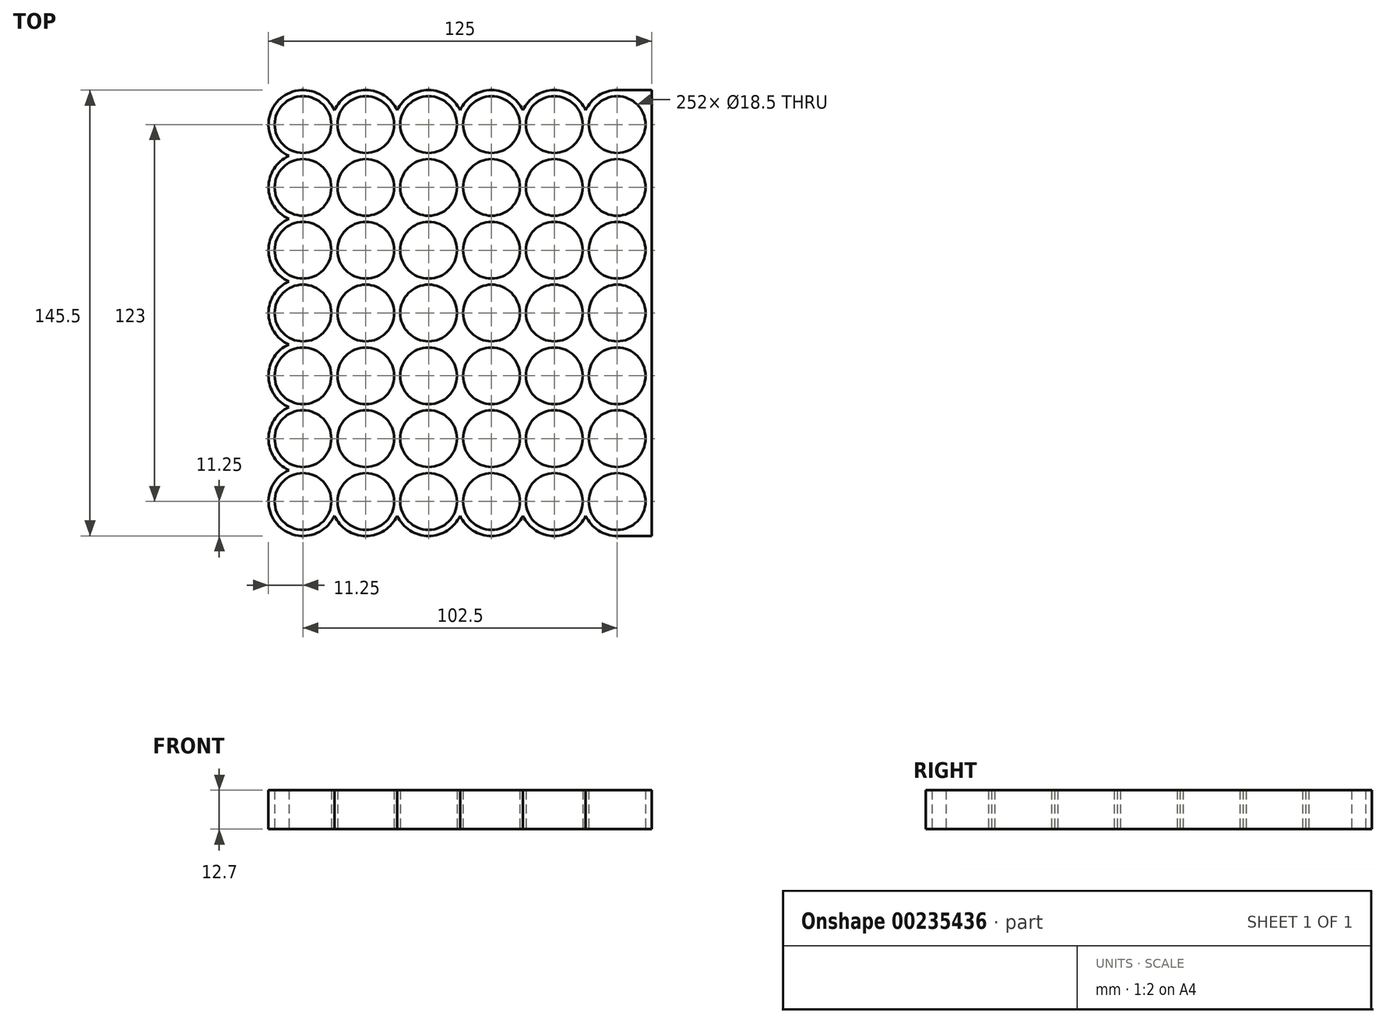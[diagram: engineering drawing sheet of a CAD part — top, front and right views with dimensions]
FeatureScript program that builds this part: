
annotation { "Feature Type Name" : "Feature", "Feature Type Description" : "" }
export const myFeature = defineFeature(function(context is Context, id is Id, definition is map)
    precondition{}
    {
        {
            var Q0;
            Q0=qCreatedBy(makeId("Top.planeOp"),FACE);
            var sketch = newSketch(context, id + "F0", { "sketchPlane" : qUnion([Q0])});
            skCircle(sketch, "E0", {"center": v(0, 0) * mm, "radius": 9.25 * mm});
            skCircle(sketch, "E1.0", {"center": v(0, 0) * mm, "radius": 11.25 * mm});
            skCircle(sketch, "E2.0.1.0", {"center": v(0, 20.5) * mm, "radius": 11.25 * mm});
            skCircle(sketch, "E2.0.1.1", {"center": v(0, 20.5) * mm, "radius": 9.25 * mm});
            skCircle(sketch, "E2.0.2.0", {"center": v(0, 41) * mm, "radius": 11.25 * mm});
            skCircle(sketch, "E2.0.2.1", {"center": v(0, 41) * mm, "radius": 9.25 * mm});
            skCircle(sketch, "E2.0.3.0", {"center": v(0, 61.5) * mm, "radius": 11.25 * mm});
            skCircle(sketch, "E2.0.3.1", {"center": v(0, 61.5) * mm, "radius": 9.25 * mm});
            skCircle(sketch, "E2.0.4.0", {"center": v(0, 82) * mm, "radius": 11.25 * mm});
            skCircle(sketch, "E2.0.4.1", {"center": v(0, 82) * mm, "radius": 9.25 * mm});
            skCircle(sketch, "E2.0.5.0", {"center": v(0, 102.5) * mm, "radius": 11.25 * mm});
            skCircle(sketch, "E2.0.5.1", {"center": v(0, 102.5) * mm, "radius": 9.25 * mm});
            skCircle(sketch, "E2.0.6.0", {"center": v(0, 123) * mm, "radius": 11.25 * mm});
            skCircle(sketch, "E2.0.6.1", {"center": v(0, 123) * mm, "radius": 9.25 * mm});
            skCircle(sketch, "E2.1.0.0", {"center": v(20.5, 0) * mm, "radius": 11.25 * mm});
            skCircle(sketch, "E2.1.0.1", {"center": v(20.5, 0) * mm, "radius": 9.25 * mm});
            skCircle(sketch, "E2.1.1.0", {"center": v(20.5, 20.5) * mm, "radius": 11.25 * mm});
            skCircle(sketch, "E2.1.1.1", {"center": v(20.5, 20.5) * mm, "radius": 9.25 * mm});
            skCircle(sketch, "E2.1.2.0", {"center": v(20.5, 41) * mm, "radius": 11.25 * mm});
            skCircle(sketch, "E2.1.2.1", {"center": v(20.5, 41) * mm, "radius": 9.25 * mm});
            skCircle(sketch, "E2.1.3.0", {"center": v(20.5, 61.5) * mm, "radius": 11.25 * mm});
            skCircle(sketch, "E2.1.3.1", {"center": v(20.5, 61.5) * mm, "radius": 9.25 * mm});
            skCircle(sketch, "E2.1.4.0", {"center": v(20.5, 82) * mm, "radius": 11.25 * mm});
            skCircle(sketch, "E2.1.4.1", {"center": v(20.5, 82) * mm, "radius": 9.25 * mm});
            skCircle(sketch, "E2.1.5.0", {"center": v(20.5, 102.5) * mm, "radius": 11.25 * mm});
            skCircle(sketch, "E2.1.5.1", {"center": v(20.5, 102.5) * mm, "radius": 9.25 * mm});
            skCircle(sketch, "E2.1.6.0", {"center": v(20.5, 123) * mm, "radius": 11.25 * mm});
            skCircle(sketch, "E2.1.6.1", {"center": v(20.5, 123) * mm, "radius": 9.25 * mm});
            skCircle(sketch, "E2.2.0.0", {"center": v(41, 0) * mm, "radius": 11.25 * mm});
            skCircle(sketch, "E2.2.0.1", {"center": v(41, 0) * mm, "radius": 9.25 * mm});
            skCircle(sketch, "E2.2.1.0", {"center": v(41, 20.5) * mm, "radius": 11.25 * mm});
            skCircle(sketch, "E2.2.1.1", {"center": v(41, 20.5) * mm, "radius": 9.25 * mm});
            skCircle(sketch, "E2.2.2.0", {"center": v(41, 41) * mm, "radius": 11.25 * mm});
            skCircle(sketch, "E2.2.2.1", {"center": v(41, 41) * mm, "radius": 9.25 * mm});
            skCircle(sketch, "E2.2.3.0", {"center": v(41, 61.5) * mm, "radius": 11.25 * mm});
            skCircle(sketch, "E2.2.3.1", {"center": v(41, 61.5) * mm, "radius": 9.25 * mm});
            skCircle(sketch, "E2.2.4.0", {"center": v(41, 82) * mm, "radius": 11.25 * mm});
            skCircle(sketch, "E2.2.4.1", {"center": v(41, 82) * mm, "radius": 9.25 * mm});
            skCircle(sketch, "E2.2.5.0", {"center": v(41, 102.5) * mm, "radius": 11.25 * mm});
            skCircle(sketch, "E2.2.5.1", {"center": v(41, 102.5) * mm, "radius": 9.25 * mm});
            skCircle(sketch, "E2.2.6.0", {"center": v(41, 123) * mm, "radius": 11.25 * mm});
            skCircle(sketch, "E2.2.6.1", {"center": v(41, 123) * mm, "radius": 9.25 * mm});
            skCircle(sketch, "E2.3.0.0", {"center": v(61.5, 0) * mm, "radius": 11.25 * mm});
            skCircle(sketch, "E2.3.0.1", {"center": v(61.5, 0) * mm, "radius": 9.25 * mm});
            skCircle(sketch, "E2.3.1.0", {"center": v(61.5, 20.5) * mm, "radius": 11.25 * mm});
            skCircle(sketch, "E2.3.1.1", {"center": v(61.5, 20.5) * mm, "radius": 9.25 * mm});
            skCircle(sketch, "E2.3.2.0", {"center": v(61.5, 41) * mm, "radius": 11.25 * mm});
            skCircle(sketch, "E2.3.2.1", {"center": v(61.5, 41) * mm, "radius": 9.25 * mm});
            skCircle(sketch, "E2.3.3.0", {"center": v(61.5, 61.5) * mm, "radius": 11.25 * mm});
            skCircle(sketch, "E2.3.3.1", {"center": v(61.5, 61.5) * mm, "radius": 9.25 * mm});
            skCircle(sketch, "E2.3.4.0", {"center": v(61.5, 82) * mm, "radius": 11.25 * mm});
            skCircle(sketch, "E2.3.4.1", {"center": v(61.5, 82) * mm, "radius": 9.25 * mm});
            skCircle(sketch, "E2.3.5.0", {"center": v(61.5, 102.5) * mm, "radius": 11.25 * mm});
            skCircle(sketch, "E2.3.5.1", {"center": v(61.5, 102.5) * mm, "radius": 9.25 * mm});
            skCircle(sketch, "E2.3.6.0", {"center": v(61.5, 123) * mm, "radius": 11.25 * mm});
            skCircle(sketch, "E2.3.6.1", {"center": v(61.5, 123) * mm, "radius": 9.25 * mm});
            skCircle(sketch, "E2.4.0.0", {"center": v(82, 0) * mm, "radius": 11.25 * mm});
            skCircle(sketch, "E2.4.0.1", {"center": v(82, 0) * mm, "radius": 9.25 * mm});
            skCircle(sketch, "E2.4.1.0", {"center": v(82, 20.5) * mm, "radius": 11.25 * mm});
            skCircle(sketch, "E2.4.1.1", {"center": v(82, 20.5) * mm, "radius": 9.25 * mm});
            skCircle(sketch, "E2.4.2.0", {"center": v(82, 41) * mm, "radius": 11.25 * mm});
            skCircle(sketch, "E2.4.2.1", {"center": v(82, 41) * mm, "radius": 9.25 * mm});
            skCircle(sketch, "E2.4.3.0", {"center": v(82, 61.5) * mm, "radius": 11.25 * mm});
            skCircle(sketch, "E2.4.3.1", {"center": v(82, 61.5) * mm, "radius": 9.25 * mm});
            skCircle(sketch, "E2.4.4.0", {"center": v(82, 82) * mm, "radius": 11.25 * mm});
            skCircle(sketch, "E2.4.4.1", {"center": v(82, 82) * mm, "radius": 9.25 * mm});
            skCircle(sketch, "E2.4.5.0", {"center": v(82, 102.5) * mm, "radius": 11.25 * mm});
            skCircle(sketch, "E2.4.5.1", {"center": v(82, 102.5) * mm, "radius": 9.25 * mm});
            skCircle(sketch, "E2.4.6.0", {"center": v(82, 123) * mm, "radius": 11.25 * mm});
            skCircle(sketch, "E2.4.6.1", {"center": v(82, 123) * mm, "radius": 9.25 * mm});
            skCircle(sketch, "E2.5.0.0", {"center": v(102.5, 0) * mm, "radius": 11.25 * mm});
            skCircle(sketch, "E2.5.0.1", {"center": v(102.5, 0) * mm, "radius": 9.25 * mm});
            skCircle(sketch, "E2.5.1.0", {"center": v(102.5, 20.5) * mm, "radius": 11.25 * mm});
            skCircle(sketch, "E2.5.1.1", {"center": v(102.5, 20.5) * mm, "radius": 9.25 * mm});
            skCircle(sketch, "E2.5.2.0", {"center": v(102.5, 41) * mm, "radius": 11.25 * mm});
            skCircle(sketch, "E2.5.2.1", {"center": v(102.5, 41) * mm, "radius": 9.25 * mm});
            skCircle(sketch, "E2.5.3.0", {"center": v(102.5, 61.5) * mm, "radius": 11.25 * mm});
            skCircle(sketch, "E2.5.3.1", {"center": v(102.5, 61.5) * mm, "radius": 9.25 * mm});
            skCircle(sketch, "E2.5.4.0", {"center": v(102.5, 82) * mm, "radius": 11.25 * mm});
            skCircle(sketch, "E2.5.4.1", {"center": v(102.5, 82) * mm, "radius": 9.25 * mm});
            skCircle(sketch, "E2.5.5.0", {"center": v(102.5, 102.5) * mm, "radius": 11.25 * mm});
            skCircle(sketch, "E2.5.5.1", {"center": v(102.5, 102.5) * mm, "radius": 9.25 * mm});
            skCircle(sketch, "E2.5.6.0", {"center": v(102.5, 123) * mm, "radius": 11.25 * mm});
            skCircle(sketch, "E2.5.6.1", {"center": v(102.5, 123) * mm, "radius": 9.25 * mm});
            skLineSegment(sketch, "E2.direction1", {"start": v(0, 0) * mm, "end": v(20.5, 0) * mm, "construction": true});
            skLineSegment(sketch, "E2.direction2", {"start": v(0, 0) * mm, "end": v(0, 20.5) * mm, "construction": true});
            skLineSegment(sketch, "E3", {"start": v(102.5, 0) * mm, "end": v(102.5, -11.25) * mm, "construction": true});
            skLineSegment(sketch, "E4", {"start": v(102.5, -11.25) * mm, "end": v(113.75, -11.25) * mm});
            skLineSegment(sketch, "E5", {"start": v(102.5, 123) * mm, "end": v(102.5, 134.25) * mm, "construction": true});
            skLineSegment(sketch, "E6", {"start": v(102.5, 134.25) * mm, "end": v(113.75, 134.25) * mm});
            skLineSegment(sketch, "E7", {"start": v(113.75, 134.25) * mm, "end": v(113.75, -11.25) * mm});
            skSolve(sketch);
        }
        {
            var Q0;
            {var subQ0=sQuery(id+"F0.wireOp",EDGE,"E2.10.4.0");var subQ1=sQuery(id+"F0.wireOp",EDGE,"E2.10.3.0");var subQ2=makeQuery(id+"F0.imprint","INTERSECT",VERTEX,{"disambiguationData":[OD(0.0)],"derivedFrom":[subQ1,subQ0]});Q0=makeQuery(id+"F0.imprint","IMPRINT",FACE,{"disambiguationData":[TD([[makeQuery(id+"F0.imprint","IMPRINT",EDGE,{"disambiguationData":[TD([[subQ2,-1.0]])],"derivedFrom":subQ1}),1.0]])]});}
            var Q1;
            {var subQ0=sQuery(id+"F0.wireOp",EDGE,"E2.1.5.0");var subQ1=sQuery(id+"F0.wireOp",EDGE,"E2.0.5.0");var subQ2=makeQuery(id+"F0.imprint","INTERSECT",VERTEX,{"disambiguationData":[OD(0.0)],"derivedFrom":[subQ1,subQ0]});Q1=makeQuery(id+"F0.imprint","IMPRINT",FACE,{"disambiguationData":[TD([[makeQuery(id+"F0.imprint","IMPRINT",EDGE,{"disambiguationData":[TD([[subQ2,-1.0]])],"derivedFrom":subQ1}),-1.0]])]});}
            var Q2;
            {var subQ0=sQuery(id+"F0.wireOp",EDGE,"E2.0.1.0");var subQ1=sQuery(id+"F0.wireOp",EDGE,"E1.0");var subQ2=makeQuery(id+"F0.imprint","INTERSECT",VERTEX,{"disambiguationData":[OD(1.0)],"derivedFrom":[subQ1,subQ0]});Q2=makeQuery(id+"F0.imprint","IMPRINT",FACE,{"disambiguationData":[TD([[makeQuery(id+"F0.imprint","IMPRINT",EDGE,{"disambiguationData":[TD([[subQ2,-1.0]])],"derivedFrom":subQ1}),-1.0]])]});}
            var Q3;
            {var subQ0=sQuery(id+"F0.wireOp",EDGE,"E2.2.3.0");var subQ1=sQuery(id+"F0.wireOp",EDGE,"E2.1.3.0");var subQ2=makeQuery(id+"F0.imprint","INTERSECT",VERTEX,{"disambiguationData":[OD(0.0)],"derivedFrom":[subQ1,subQ0]});Q3=makeQuery(id+"F0.imprint","IMPRINT",FACE,{"disambiguationData":[TD([[makeQuery(id+"F0.imprint","IMPRINT",EDGE,{"disambiguationData":[TD([[subQ2,-1.0]])],"derivedFrom":subQ1}),-1.0]])]});}
            var Q4;
            {var subQ0=sQuery(id+"F0.wireOp",EDGE,"E2.2.5.0");var subQ1=sQuery(id+"F0.wireOp",EDGE,"E2.1.5.0");var subQ2=makeQuery(id+"F0.imprint","INTERSECT",VERTEX,{"disambiguationData":[OD(0.0)],"derivedFrom":[subQ1,subQ0]});Q4=makeQuery(id+"F0.imprint","IMPRINT",FACE,{"disambiguationData":[TD([[makeQuery(id+"F0.imprint","IMPRINT",EDGE,{"disambiguationData":[TD([[subQ2,-1.0]])],"derivedFrom":subQ1}),-1.0]])]});}
            var Q5;
            {var subQ0=sQuery(id+"F0.wireOp",EDGE,"E2.3.1.0");var subQ1=sQuery(id+"F0.wireOp",EDGE,"E2.2.1.0");var subQ2=makeQuery(id+"F0.imprint","INTERSECT",VERTEX,{"disambiguationData":[OD(0.0)],"derivedFrom":[subQ1,subQ0]});Q5=makeQuery(id+"F0.imprint","IMPRINT",FACE,{"disambiguationData":[TD([[makeQuery(id+"F0.imprint","IMPRINT",EDGE,{"disambiguationData":[TD([[subQ2,-1.0]])],"derivedFrom":subQ1}),-1.0]])]});}
            var Q6;
            {var subQ0=sQuery(id+"F0.wireOp",EDGE,"E2.3.3.0");var subQ1=sQuery(id+"F0.wireOp",EDGE,"E2.2.3.0");var subQ2=makeQuery(id+"F0.imprint","INTERSECT",VERTEX,{"disambiguationData":[OD(0.0)],"derivedFrom":[subQ1,subQ0]});Q6=makeQuery(id+"F0.imprint","IMPRINT",FACE,{"disambiguationData":[TD([[makeQuery(id+"F0.imprint","IMPRINT",EDGE,{"disambiguationData":[TD([[subQ2,-1.0]])],"derivedFrom":subQ1}),-1.0]])]});}
            var Q7;
            {var subQ0=sQuery(id+"F0.wireOp",EDGE,"E2.1.3.0");var subQ1=sQuery(id+"F0.wireOp",EDGE,"E2.0.3.0");var subQ2=makeQuery(id+"F0.imprint","INTERSECT",VERTEX,{"disambiguationData":[OD(0.0)],"derivedFrom":[subQ1,subQ0]});Q7=makeQuery(id+"F0.imprint","IMPRINT",FACE,{"disambiguationData":[TD([[makeQuery(id+"F0.imprint","IMPRINT",EDGE,{"disambiguationData":[TD([[subQ2,1.0]])],"derivedFrom":subQ1}),1.0]])]});}
            var Q8;
            {var subQ0=sQuery(id+"F0.wireOp",EDGE,"E2.2.1.0");var subQ1=sQuery(id+"F0.wireOp",EDGE,"E2.1.1.0");var subQ2=makeQuery(id+"F0.imprint","INTERSECT",VERTEX,{"disambiguationData":[OD(0.0)],"derivedFrom":[subQ1,subQ0]});Q8=makeQuery(id+"F0.imprint","IMPRINT",FACE,{"disambiguationData":[TD([[makeQuery(id+"F0.imprint","IMPRINT",EDGE,{"disambiguationData":[TD([[subQ2,-1.0]])],"derivedFrom":subQ1}),-1.0]])]});}
            var Q9;
            {var subQ0=sQuery(id+"F0.wireOp",EDGE,"E2.7.6.0");var subQ1=sQuery(id+"F0.wireOp",EDGE,"E2.6.6.0");var subQ2=makeQuery(id+"F0.imprint","INTERSECT",VERTEX,{"disambiguationData":[OD(0.0)],"derivedFrom":[subQ1,subQ0]});Q9=makeQuery(id+"F0.imprint","IMPRINT",FACE,{"disambiguationData":[TD([[makeQuery(id+"F0.imprint","IMPRINT",EDGE,{"disambiguationData":[TD([[subQ2,1.0]])],"derivedFrom":subQ1}),-1.0]])]});}
            var Q10;
            {var subQ0=sQuery(id+"F0.wireOp",EDGE,"E2.11.6.0");var subQ1=sQuery(id+"F0.wireOp",EDGE,"E2.10.6.0");var subQ2=makeQuery(id+"F0.imprint","INTERSECT",VERTEX,{"disambiguationData":[OD(0.0)],"derivedFrom":[subQ1,subQ0]});Q10=makeQuery(id+"F0.imprint","IMPRINT",FACE,{"disambiguationData":[TD([[makeQuery(id+"F0.imprint","IMPRINT",EDGE,{"disambiguationData":[TD([[subQ2,1.0]])],"derivedFrom":subQ1}),-1.0]])]});}
            var Q11;
            {var subQ0=sQuery(id+"F0.wireOp",EDGE,"E2.11.3.0");var subQ1=sQuery(id+"F0.wireOp",EDGE,"E2.10.3.0");var subQ2=makeQuery(id+"F0.imprint","INTERSECT",VERTEX,{"disambiguationData":[OD(0.0)],"derivedFrom":[subQ1,subQ0]});Q11=makeQuery(id+"F0.imprint","IMPRINT",FACE,{"disambiguationData":[TD([[makeQuery(id+"F0.imprint","IMPRINT",EDGE,{"disambiguationData":[TD([[subQ2,-1.0]])],"derivedFrom":subQ1}),-1.0]])]});}
            var Q12;
            {var subQ0=sQuery(id+"F0.wireOp",EDGE,"E2.11.5.0");var subQ1=sQuery(id+"F0.wireOp",EDGE,"E2.10.5.0");var subQ2=makeQuery(id+"F0.imprint","INTERSECT",VERTEX,{"disambiguationData":[OD(0.0)],"derivedFrom":[subQ1,subQ0]});Q12=makeQuery(id+"F0.imprint","IMPRINT",FACE,{"disambiguationData":[TD([[makeQuery(id+"F0.imprint","IMPRINT",EDGE,{"disambiguationData":[TD([[subQ2,-1.0]])],"derivedFrom":subQ1}),-1.0]])]});}
            var Q13;
            {var subQ0=sQuery(id+"F0.wireOp",EDGE,"E2.9.5.0");var subQ1=sQuery(id+"F0.wireOp",EDGE,"E2.8.5.0");var subQ2=makeQuery(id+"F0.imprint","INTERSECT",VERTEX,{"disambiguationData":[OD(0.0)],"derivedFrom":[subQ1,subQ0]});Q13=makeQuery(id+"F0.imprint","IMPRINT",FACE,{"disambiguationData":[TD([[makeQuery(id+"F0.imprint","IMPRINT",EDGE,{"disambiguationData":[TD([[subQ2,-1.0]])],"derivedFrom":subQ1}),-1.0]])]});}
            var Q14;
            {var subQ0=sQuery(id+"F0.wireOp",EDGE,"E2.10.1.0");var subQ1=sQuery(id+"F0.wireOp",EDGE,"E2.9.1.0");var subQ2=makeQuery(id+"F0.imprint","INTERSECT",VERTEX,{"disambiguationData":[OD(0.0)],"derivedFrom":[subQ1,subQ0]});Q14=makeQuery(id+"F0.imprint","IMPRINT",FACE,{"disambiguationData":[TD([[makeQuery(id+"F0.imprint","IMPRINT",EDGE,{"disambiguationData":[TD([[subQ2,-1.0]])],"derivedFrom":subQ1}),-1.0]])]});}
            var Q15;
            {var subQ0=sQuery(id+"F0.wireOp",EDGE,"E2.10.3.0");var subQ1=sQuery(id+"F0.wireOp",EDGE,"E2.9.3.0");var subQ2=makeQuery(id+"F0.imprint","INTERSECT",VERTEX,{"disambiguationData":[OD(0.0)],"derivedFrom":[subQ1,subQ0]});Q15=makeQuery(id+"F0.imprint","IMPRINT",FACE,{"disambiguationData":[TD([[makeQuery(id+"F0.imprint","IMPRINT",EDGE,{"disambiguationData":[TD([[subQ2,-1.0]])],"derivedFrom":subQ1}),-1.0]])]});}
            var Q16;
            {var subQ0=sQuery(id+"F0.wireOp",EDGE,"E2.10.5.0");var subQ1=sQuery(id+"F0.wireOp",EDGE,"E2.9.5.0");var subQ2=makeQuery(id+"F0.imprint","INTERSECT",VERTEX,{"disambiguationData":[OD(0.0)],"derivedFrom":[subQ1,subQ0]});Q16=makeQuery(id+"F0.imprint","IMPRINT",FACE,{"disambiguationData":[TD([[makeQuery(id+"F0.imprint","IMPRINT",EDGE,{"disambiguationData":[TD([[subQ2,-1.0]])],"derivedFrom":subQ1}),-1.0]])]});}
            var Q17;
            {var subQ0=sQuery(id+"F0.wireOp",EDGE,"E2.8.3.0");var subQ1=sQuery(id+"F0.wireOp",EDGE,"E2.7.3.0");var subQ2=makeQuery(id+"F0.imprint","INTERSECT",VERTEX,{"disambiguationData":[OD(0.0)],"derivedFrom":[subQ1,subQ0]});Q17=makeQuery(id+"F0.imprint","IMPRINT",FACE,{"disambiguationData":[TD([[makeQuery(id+"F0.imprint","IMPRINT",EDGE,{"disambiguationData":[TD([[subQ2,-1.0]])],"derivedFrom":subQ1}),-1.0]])]});}
            var Q18;
            {var subQ0=sQuery(id+"F0.wireOp",EDGE,"E2.8.5.0");var subQ1=sQuery(id+"F0.wireOp",EDGE,"E2.7.5.0");var subQ2=makeQuery(id+"F0.imprint","INTERSECT",VERTEX,{"disambiguationData":[OD(0.0)],"derivedFrom":[subQ1,subQ0]});Q18=makeQuery(id+"F0.imprint","IMPRINT",FACE,{"disambiguationData":[TD([[makeQuery(id+"F0.imprint","IMPRINT",EDGE,{"disambiguationData":[TD([[subQ2,-1.0]])],"derivedFrom":subQ1}),-1.0]])]});}
            var Q19;
            {var subQ0=sQuery(id+"F0.wireOp",EDGE,"E2.9.1.0");var subQ1=sQuery(id+"F0.wireOp",EDGE,"E2.8.1.0");var subQ2=makeQuery(id+"F0.imprint","INTERSECT",VERTEX,{"disambiguationData":[OD(0.0)],"derivedFrom":[subQ1,subQ0]});Q19=makeQuery(id+"F0.imprint","IMPRINT",FACE,{"disambiguationData":[TD([[makeQuery(id+"F0.imprint","IMPRINT",EDGE,{"disambiguationData":[TD([[subQ2,-1.0]])],"derivedFrom":subQ1}),-1.0]])]});}
            var Q20;
            {var subQ0=sQuery(id+"F0.wireOp",EDGE,"E2.9.3.0");var subQ1=sQuery(id+"F0.wireOp",EDGE,"E2.8.3.0");var subQ2=makeQuery(id+"F0.imprint","INTERSECT",VERTEX,{"disambiguationData":[OD(0.0)],"derivedFrom":[subQ1,subQ0]});Q20=makeQuery(id+"F0.imprint","IMPRINT",FACE,{"disambiguationData":[TD([[makeQuery(id+"F0.imprint","IMPRINT",EDGE,{"disambiguationData":[TD([[subQ2,-1.0]])],"derivedFrom":subQ1}),-1.0]])]});}
            var Q21;
            {var subQ0=sQuery(id+"F0.wireOp",EDGE,"E2.7.5.0");var subQ1=sQuery(id+"F0.wireOp",EDGE,"E2.6.5.0");var subQ2=makeQuery(id+"F0.imprint","INTERSECT",VERTEX,{"disambiguationData":[OD(0.0)],"derivedFrom":[subQ1,subQ0]});Q21=makeQuery(id+"F0.imprint","IMPRINT",FACE,{"disambiguationData":[TD([[makeQuery(id+"F0.imprint","IMPRINT",EDGE,{"disambiguationData":[TD([[subQ2,-1.0]])],"derivedFrom":subQ1}),-1.0]])]});}
            var Q22;
            {var subQ0=sQuery(id+"F0.wireOp",EDGE,"E2.8.1.0");var subQ1=sQuery(id+"F0.wireOp",EDGE,"E2.7.1.0");var subQ2=makeQuery(id+"F0.imprint","INTERSECT",VERTEX,{"disambiguationData":[OD(0.0)],"derivedFrom":[subQ1,subQ0]});Q22=makeQuery(id+"F0.imprint","IMPRINT",FACE,{"disambiguationData":[TD([[makeQuery(id+"F0.imprint","IMPRINT",EDGE,{"disambiguationData":[TD([[subQ2,-1.0]])],"derivedFrom":subQ1}),-1.0]])]});}
            var Q23;
            {var subQ0=sQuery(id+"F0.wireOp",EDGE,"E2.6.3.0");var subQ1=sQuery(id+"F0.wireOp",EDGE,"E2.5.3.0");var subQ2=makeQuery(id+"F0.imprint","INTERSECT",VERTEX,{"disambiguationData":[OD(0.0)],"derivedFrom":[subQ1,subQ0]});Q23=makeQuery(id+"F0.imprint","IMPRINT",FACE,{"disambiguationData":[TD([[makeQuery(id+"F0.imprint","IMPRINT",EDGE,{"disambiguationData":[TD([[subQ2,-1.0]])],"derivedFrom":subQ1}),-1.0]])]});}
            var Q24;
            {var subQ0=sQuery(id+"F0.wireOp",EDGE,"E2.6.5.0");var subQ1=sQuery(id+"F0.wireOp",EDGE,"E2.5.5.0");var subQ2=makeQuery(id+"F0.imprint","INTERSECT",VERTEX,{"disambiguationData":[OD(0.0)],"derivedFrom":[subQ1,subQ0]});Q24=makeQuery(id+"F0.imprint","IMPRINT",FACE,{"disambiguationData":[TD([[makeQuery(id+"F0.imprint","IMPRINT",EDGE,{"disambiguationData":[TD([[subQ2,-1.0]])],"derivedFrom":subQ1}),-1.0]])]});}
            var Q25;
            {var subQ0=sQuery(id+"F0.wireOp",EDGE,"E2.7.1.0");var subQ1=sQuery(id+"F0.wireOp",EDGE,"E2.6.1.0");var subQ2=makeQuery(id+"F0.imprint","INTERSECT",VERTEX,{"disambiguationData":[OD(0.0)],"derivedFrom":[subQ1,subQ0]});Q25=makeQuery(id+"F0.imprint","IMPRINT",FACE,{"disambiguationData":[TD([[makeQuery(id+"F0.imprint","IMPRINT",EDGE,{"disambiguationData":[TD([[subQ2,-1.0]])],"derivedFrom":subQ1}),-1.0]])]});}
            var Q26;
            {var subQ0=sQuery(id+"F0.wireOp",EDGE,"E2.7.3.0");var subQ1=sQuery(id+"F0.wireOp",EDGE,"E2.6.3.0");var subQ2=makeQuery(id+"F0.imprint","INTERSECT",VERTEX,{"disambiguationData":[OD(0.0)],"derivedFrom":[subQ1,subQ0]});Q26=makeQuery(id+"F0.imprint","IMPRINT",FACE,{"disambiguationData":[TD([[makeQuery(id+"F0.imprint","IMPRINT",EDGE,{"disambiguationData":[TD([[subQ2,-1.0]])],"derivedFrom":subQ1}),-1.0]])]});}
            var Q27;
            {var subQ0=sQuery(id+"F0.wireOp",EDGE,"E2.5.1.0");var subQ1=sQuery(id+"F0.wireOp",EDGE,"E2.4.1.0");var subQ2=makeQuery(id+"F0.imprint","INTERSECT",VERTEX,{"disambiguationData":[OD(0.0)],"derivedFrom":[subQ1,subQ0]});Q27=makeQuery(id+"F0.imprint","IMPRINT",FACE,{"disambiguationData":[TD([[makeQuery(id+"F0.imprint","IMPRINT",EDGE,{"disambiguationData":[TD([[subQ2,-1.0]])],"derivedFrom":subQ1}),-1.0]])]});}
            var Q28;
            {var subQ0=sQuery(id+"F0.wireOp",EDGE,"E2.5.3.0");var subQ1=sQuery(id+"F0.wireOp",EDGE,"E2.4.3.0");var subQ2=makeQuery(id+"F0.imprint","INTERSECT",VERTEX,{"disambiguationData":[OD(0.0)],"derivedFrom":[subQ1,subQ0]});Q28=makeQuery(id+"F0.imprint","IMPRINT",FACE,{"disambiguationData":[TD([[makeQuery(id+"F0.imprint","IMPRINT",EDGE,{"disambiguationData":[TD([[subQ2,-1.0]])],"derivedFrom":subQ1}),-1.0]])]});}
            var Q29;
            {var subQ0=sQuery(id+"F0.wireOp",EDGE,"E2.5.5.0");var subQ1=sQuery(id+"F0.wireOp",EDGE,"E2.4.5.0");var subQ2=makeQuery(id+"F0.imprint","INTERSECT",VERTEX,{"disambiguationData":[OD(0.0)],"derivedFrom":[subQ1,subQ0]});Q29=makeQuery(id+"F0.imprint","IMPRINT",FACE,{"disambiguationData":[TD([[makeQuery(id+"F0.imprint","IMPRINT",EDGE,{"disambiguationData":[TD([[subQ2,-1.0]])],"derivedFrom":subQ1}),-1.0]])]});}
            var Q30;
            {var subQ0=sQuery(id+"F0.wireOp",EDGE,"E2.6.1.0");var subQ1=sQuery(id+"F0.wireOp",EDGE,"E2.5.1.0");var subQ2=makeQuery(id+"F0.imprint","INTERSECT",VERTEX,{"disambiguationData":[OD(0.0)],"derivedFrom":[subQ1,subQ0]});Q30=makeQuery(id+"F0.imprint","IMPRINT",FACE,{"disambiguationData":[TD([[makeQuery(id+"F0.imprint","IMPRINT",EDGE,{"disambiguationData":[TD([[subQ2,-1.0]])],"derivedFrom":subQ1}),-1.0]])]});}
            var Q31;
            {var subQ0=sQuery(id+"F0.wireOp",EDGE,"E2.3.5.0");var subQ1=sQuery(id+"F0.wireOp",EDGE,"E2.2.5.0");var subQ2=makeQuery(id+"F0.imprint","INTERSECT",VERTEX,{"disambiguationData":[OD(0.0)],"derivedFrom":[subQ1,subQ0]});Q31=makeQuery(id+"F0.imprint","IMPRINT",FACE,{"disambiguationData":[TD([[makeQuery(id+"F0.imprint","IMPRINT",EDGE,{"disambiguationData":[TD([[subQ2,-1.0]])],"derivedFrom":subQ1}),-1.0]])]});}
            var Q32;
            {var subQ0=sQuery(id+"F0.wireOp",EDGE,"E2.4.1.0");var subQ1=sQuery(id+"F0.wireOp",EDGE,"E2.3.1.0");var subQ2=makeQuery(id+"F0.imprint","INTERSECT",VERTEX,{"disambiguationData":[OD(0.0)],"derivedFrom":[subQ1,subQ0]});Q32=makeQuery(id+"F0.imprint","IMPRINT",FACE,{"disambiguationData":[TD([[makeQuery(id+"F0.imprint","IMPRINT",EDGE,{"disambiguationData":[TD([[subQ2,-1.0]])],"derivedFrom":subQ1}),-1.0]])]});}
            var Q33;
            {var subQ0=sQuery(id+"F0.wireOp",EDGE,"E2.4.3.0");var subQ1=sQuery(id+"F0.wireOp",EDGE,"E2.3.3.0");var subQ2=makeQuery(id+"F0.imprint","INTERSECT",VERTEX,{"disambiguationData":[OD(0.0)],"derivedFrom":[subQ1,subQ0]});Q33=makeQuery(id+"F0.imprint","IMPRINT",FACE,{"disambiguationData":[TD([[makeQuery(id+"F0.imprint","IMPRINT",EDGE,{"disambiguationData":[TD([[subQ2,-1.0]])],"derivedFrom":subQ1}),-1.0]])]});}
            var Q34;
            {var subQ0=sQuery(id+"F0.wireOp",EDGE,"E2.4.5.0");var subQ1=sQuery(id+"F0.wireOp",EDGE,"E2.3.5.0");var subQ2=makeQuery(id+"F0.imprint","INTERSECT",VERTEX,{"disambiguationData":[OD(0.0)],"derivedFrom":[subQ1,subQ0]});Q34=makeQuery(id+"F0.imprint","IMPRINT",FACE,{"disambiguationData":[TD([[makeQuery(id+"F0.imprint","IMPRINT",EDGE,{"disambiguationData":[TD([[subQ2,-1.0]])],"derivedFrom":subQ1}),-1.0]])]});}
            var Q35;
            {var subQ0=sQuery(id+"F0.wireOp",EDGE,"E2.11.1.0");var subQ1=sQuery(id+"F0.wireOp",EDGE,"E2.10.1.0");var subQ2=makeQuery(id+"F0.imprint","INTERSECT",VERTEX,{"disambiguationData":[OD(0.0)],"derivedFrom":[subQ1,subQ0]});Q35=makeQuery(id+"F0.imprint","IMPRINT",FACE,{"disambiguationData":[TD([[makeQuery(id+"F0.imprint","IMPRINT",EDGE,{"disambiguationData":[TD([[subQ2,-1.0]])],"derivedFrom":subQ1}),1.0]])]});}
            var Q36;
            {var subQ0=sQuery(id+"F0.wireOp",EDGE,"E2.1.0.0");var subQ1=sQuery(id+"F0.wireOp",EDGE,"E1.0");var subQ2=makeQuery(id+"F0.imprint","INTERSECT",VERTEX,{"disambiguationData":[OD(1.0)],"derivedFrom":[subQ1,subQ0]});Q36=makeQuery(id+"F0.imprint","IMPRINT",FACE,{"disambiguationData":[TD([[makeQuery(id+"F0.imprint","IMPRINT",EDGE,{"disambiguationData":[TD([[subQ2,-1.0]])],"derivedFrom":subQ1}),-1.0]])]});}
            var Q37;
            {var subQ0=sQuery(id+"F0.wireOp",EDGE,"E2.10.3.0");var subQ1=sQuery(id+"F0.wireOp",EDGE,"E2.9.3.0");var subQ2=makeQuery(id+"F0.imprint","INTERSECT",VERTEX,{"disambiguationData":[OD(0.0)],"derivedFrom":[subQ1,subQ0]});Q37=makeQuery(id+"F0.imprint","IMPRINT",FACE,{"disambiguationData":[TD([[makeQuery(id+"F0.imprint","IMPRINT",EDGE,{"disambiguationData":[TD([[subQ2,-1.0]])],"derivedFrom":subQ1}),1.0]])]});}
            var Q38;
            {var subQ0=sQuery(id+"F0.wireOp",EDGE,"E2.8.5.0");var subQ1=sQuery(id+"F0.wireOp",EDGE,"E2.7.5.0");var subQ2=makeQuery(id+"F0.imprint","INTERSECT",VERTEX,{"disambiguationData":[OD(0.0)],"derivedFrom":[subQ1,subQ0]});Q38=makeQuery(id+"F0.imprint","IMPRINT",FACE,{"disambiguationData":[TD([[makeQuery(id+"F0.imprint","IMPRINT",EDGE,{"disambiguationData":[TD([[subQ2,-1.0]])],"derivedFrom":subQ1}),1.0]])]});}
            var Q39;
            {var subQ0=sQuery(id+"F0.wireOp",EDGE,"E2.9.3.0");var subQ1=sQuery(id+"F0.wireOp",EDGE,"E2.8.3.0");var subQ2=makeQuery(id+"F0.imprint","INTERSECT",VERTEX,{"disambiguationData":[OD(0.0)],"derivedFrom":[subQ1,subQ0]});Q39=makeQuery(id+"F0.imprint","IMPRINT",FACE,{"disambiguationData":[TD([[makeQuery(id+"F0.imprint","IMPRINT",EDGE,{"disambiguationData":[TD([[subQ2,-1.0]])],"derivedFrom":subQ1}),1.0]])]});}
            var Q40;
            {var subQ0=sQuery(id+"F0.wireOp",EDGE,"E2.5.3.0");var subQ1=sQuery(id+"F0.wireOp",EDGE,"E2.4.3.0");var subQ2=makeQuery(id+"F0.imprint","INTERSECT",VERTEX,{"disambiguationData":[OD(0.0)],"derivedFrom":[subQ1,subQ0]});Q40=makeQuery(id+"F0.imprint","IMPRINT",FACE,{"disambiguationData":[TD([[makeQuery(id+"F0.imprint","IMPRINT",EDGE,{"disambiguationData":[TD([[subQ2,-1.0]])],"derivedFrom":subQ1}),1.0]])]});}
            var Q41;
            {var subQ0=sQuery(id+"F0.wireOp",EDGE,"E2.0.2.0");var subQ1=sQuery(id+"F0.wireOp",EDGE,"E2.0.1.0");var subQ2=makeQuery(id+"F0.imprint","INTERSECT",VERTEX,{"disambiguationData":[OD(0.0)],"derivedFrom":[subQ1,subQ0]});Q41=makeQuery(id+"F0.imprint","IMPRINT",FACE,{"disambiguationData":[TD([[makeQuery(id+"F0.imprint","IMPRINT",EDGE,{"disambiguationData":[TD([[subQ2,1.0]])],"derivedFrom":subQ1}),-1.0]])]});}
            var Q42;
            {var subQ0=sQuery(id+"F0.wireOp",EDGE,"E2.6.1.0");var subQ1=sQuery(id+"F0.wireOp",EDGE,"E2.5.1.0");var subQ2=makeQuery(id+"F0.imprint","INTERSECT",VERTEX,{"disambiguationData":[OD(0.0)],"derivedFrom":[subQ1,subQ0]});Q42=makeQuery(id+"F0.imprint","IMPRINT",FACE,{"disambiguationData":[TD([[makeQuery(id+"F0.imprint","IMPRINT",EDGE,{"disambiguationData":[TD([[subQ2,-1.0]])],"derivedFrom":subQ1}),1.0]])]});}
            var Q43;
            {var subQ0=sQuery(id+"F0.wireOp",EDGE,"E2.3.5.0");var subQ1=sQuery(id+"F0.wireOp",EDGE,"E2.2.5.0");var subQ2=makeQuery(id+"F0.imprint","INTERSECT",VERTEX,{"disambiguationData":[OD(0.0)],"derivedFrom":[subQ1,subQ0]});Q43=makeQuery(id+"F0.imprint","IMPRINT",FACE,{"disambiguationData":[TD([[makeQuery(id+"F0.imprint","IMPRINT",EDGE,{"disambiguationData":[TD([[subQ2,-1.0]])],"derivedFrom":subQ1}),1.0]])]});}
            var Q44;
            {var subQ0=sQuery(id+"F0.wireOp",EDGE,"E2.1.0.0");var subQ1=sQuery(id+"F0.wireOp",EDGE,"E1.0");var subQ2=makeQuery(id+"F0.imprint","INTERSECT",VERTEX,{"disambiguationData":[OD(0.0)],"derivedFrom":[subQ1,subQ0]});Q44=makeQuery(id+"F0.imprint","IMPRINT",FACE,{"disambiguationData":[TD([[makeQuery(id+"F0.imprint","IMPRINT",EDGE,{"disambiguationData":[TD([[subQ2,-1.0]])],"derivedFrom":subQ1}),-1.0]])]});}
            var Q45;
            {var subQ0=sQuery(id+"F0.wireOp",EDGE,"E2.4.3.0");var subQ1=sQuery(id+"F0.wireOp",EDGE,"E2.3.3.0");var subQ2=makeQuery(id+"F0.imprint","INTERSECT",VERTEX,{"disambiguationData":[OD(0.0)],"derivedFrom":[subQ1,subQ0]});Q45=makeQuery(id+"F0.imprint","IMPRINT",FACE,{"disambiguationData":[TD([[makeQuery(id+"F0.imprint","IMPRINT",EDGE,{"disambiguationData":[TD([[subQ2,-1.0]])],"derivedFrom":subQ1}),1.0]])]});}
            var Q46;
            {var subQ0=sQuery(id+"F0.wireOp",EDGE,"E2.0.1.0");var subQ1=sQuery(id+"F0.wireOp",EDGE,"E1.0");var subQ2=makeQuery(id+"F0.imprint","INTERSECT",VERTEX,{"disambiguationData":[OD(0.0)],"derivedFrom":[subQ1,subQ0]});Q46=makeQuery(id+"F0.imprint","IMPRINT",FACE,{"disambiguationData":[TD([[makeQuery(id+"F0.imprint","IMPRINT",EDGE,{"disambiguationData":[TD([[subQ2,1.0]])],"derivedFrom":subQ1}),-1.0]])]});}
            var Q47;
            {var subQ0=sQuery(id+"F0.wireOp",EDGE,"E2.0.1.0");var subQ1=sQuery(id+"F0.wireOp",EDGE,"E0");var subQ2=makeQuery(id+"F0.imprint","INTERSECT",VERTEX,{"derivedFrom":[subQ1,subQ0]});Q47=makeQuery(id+"F0.imprint","IMPRINT",FACE,{"disambiguationData":[TD([[makeQuery(id+"F0.imprint","IMPRINT",EDGE,{"disambiguationData":[TD([[subQ2,-1.0]])],"derivedFrom":subQ1}),-1.0]])]});}
            var Q48;
            {var subQ0=sQuery(id+"F0.wireOp",EDGE,"E2.11.1.0");var subQ1=sQuery(id+"F0.wireOp",EDGE,"E2.10.1.0");var subQ2=makeQuery(id+"F0.imprint","INTERSECT",VERTEX,{"disambiguationData":[OD(0.0)],"derivedFrom":[subQ1,subQ0]});Q48=makeQuery(id+"F0.imprint","IMPRINT",FACE,{"disambiguationData":[TD([[makeQuery(id+"F0.imprint","IMPRINT",EDGE,{"disambiguationData":[TD([[subQ2,1.0]])],"derivedFrom":subQ1}),-1.0]])]});}
            var Q49;
            {var subQ0=sQuery(id+"F0.wireOp",EDGE,"E2.9.5.0");var subQ1=sQuery(id+"F0.wireOp",EDGE,"E2.8.5.0");var subQ2=makeQuery(id+"F0.imprint","INTERSECT",VERTEX,{"disambiguationData":[OD(0.0)],"derivedFrom":[subQ1,subQ0]});Q49=makeQuery(id+"F0.imprint","IMPRINT",FACE,{"disambiguationData":[TD([[makeQuery(id+"F0.imprint","IMPRINT",EDGE,{"disambiguationData":[TD([[subQ2,1.0]])],"derivedFrom":subQ1}),-1.0]])]});}
            var Q50;
            {var subQ0=sQuery(id+"F0.wireOp",EDGE,"E2.0.5.0");var subQ1=sQuery(id+"F0.wireOp",EDGE,"E2.0.4.0");var subQ2=makeQuery(id+"F0.imprint","INTERSECT",VERTEX,{"disambiguationData":[OD(0.0)],"derivedFrom":[subQ1,subQ0]});Q50=makeQuery(id+"F0.imprint","IMPRINT",FACE,{"disambiguationData":[TD([[makeQuery(id+"F0.imprint","IMPRINT",EDGE,{"disambiguationData":[TD([[subQ2,1.0]])],"derivedFrom":subQ1}),-1.0]])]});}
            var Q51;
            {var subQ0=sQuery(id+"F0.wireOp",EDGE,"E2.0.6.0");var subQ1=sQuery(id+"F0.wireOp",EDGE,"E2.0.5.0");var subQ2=makeQuery(id+"F0.imprint","INTERSECT",VERTEX,{"disambiguationData":[OD(0.0)],"derivedFrom":[subQ1,subQ0]});Q51=makeQuery(id+"F0.imprint","IMPRINT",FACE,{"disambiguationData":[TD([[makeQuery(id+"F0.imprint","IMPRINT",EDGE,{"disambiguationData":[TD([[subQ2,1.0]])],"derivedFrom":subQ1}),-1.0]])]});}
            var Q52;
            {var subQ0=sQuery(id+"F0.wireOp",EDGE,"E2.11.0.0");var subQ1=sQuery(id+"F0.wireOp",EDGE,"E2.10.0.0");var subQ2=makeQuery(id+"F0.imprint","INTERSECT",VERTEX,{"disambiguationData":[OD(0.0)],"derivedFrom":[subQ1,subQ0]});Q52=makeQuery(id+"F0.imprint","IMPRINT",FACE,{"disambiguationData":[TD([[makeQuery(id+"F0.imprint","IMPRINT",EDGE,{"disambiguationData":[TD([[subQ2,-1.0]])],"derivedFrom":subQ1}),-1.0]])]});}
            var Q53;
            {var subQ0=sQuery(id+"F0.wireOp",EDGE,"E2.8.3.0");var subQ1=sQuery(id+"F0.wireOp",EDGE,"E2.7.3.0");var subQ2=makeQuery(id+"F0.imprint","INTERSECT",VERTEX,{"disambiguationData":[OD(0.0)],"derivedFrom":[subQ1,subQ0]});Q53=makeQuery(id+"F0.imprint","IMPRINT",FACE,{"disambiguationData":[TD([[makeQuery(id+"F0.imprint","IMPRINT",EDGE,{"disambiguationData":[TD([[subQ2,1.0]])],"derivedFrom":subQ1}),-1.0]])]});}
            var Q54;
            {var subQ0=sQuery(id+"F0.wireOp",EDGE,"E2.8.5.0");var subQ1=sQuery(id+"F0.wireOp",EDGE,"E2.7.5.0");var subQ2=makeQuery(id+"F0.imprint","INTERSECT",VERTEX,{"disambiguationData":[OD(0.0)],"derivedFrom":[subQ1,subQ0]});Q54=makeQuery(id+"F0.imprint","IMPRINT",FACE,{"disambiguationData":[TD([[makeQuery(id+"F0.imprint","IMPRINT",EDGE,{"disambiguationData":[TD([[subQ2,1.0]])],"derivedFrom":subQ1}),-1.0]])]});}
            var Q55;
            {var subQ0=sQuery(id+"F0.wireOp",EDGE,"E2.7.3.0");var subQ1=sQuery(id+"F0.wireOp",EDGE,"E2.6.3.0");var subQ2=makeQuery(id+"F0.imprint","INTERSECT",VERTEX,{"disambiguationData":[OD(0.0)],"derivedFrom":[subQ1,subQ0]});Q55=makeQuery(id+"F0.imprint","IMPRINT",FACE,{"disambiguationData":[TD([[makeQuery(id+"F0.imprint","IMPRINT",EDGE,{"disambiguationData":[TD([[subQ2,1.0]])],"derivedFrom":subQ1}),-1.0]])]});}
            var Q56;
            {var subQ0=sQuery(id+"F0.wireOp",EDGE,"E2.5.5.0");var subQ1=sQuery(id+"F0.wireOp",EDGE,"E2.4.5.0");var subQ2=makeQuery(id+"F0.imprint","INTERSECT",VERTEX,{"disambiguationData":[OD(0.0)],"derivedFrom":[subQ1,subQ0]});Q56=makeQuery(id+"F0.imprint","IMPRINT",FACE,{"disambiguationData":[TD([[makeQuery(id+"F0.imprint","IMPRINT",EDGE,{"disambiguationData":[TD([[subQ2,1.0]])],"derivedFrom":subQ1}),-1.0]])]});}
            var Q57;
            {var subQ0=sQuery(id+"F0.wireOp",EDGE,"E2.6.1.0");var subQ1=sQuery(id+"F0.wireOp",EDGE,"E2.5.1.0");var subQ2=makeQuery(id+"F0.imprint","INTERSECT",VERTEX,{"disambiguationData":[OD(0.0)],"derivedFrom":[subQ1,subQ0]});Q57=makeQuery(id+"F0.imprint","IMPRINT",FACE,{"disambiguationData":[TD([[makeQuery(id+"F0.imprint","IMPRINT",EDGE,{"disambiguationData":[TD([[subQ2,1.0]])],"derivedFrom":subQ1}),-1.0]])]});}
            var Q58;
            {var subQ0=sQuery(id+"F0.wireOp",EDGE,"E2.4.5.0");var subQ1=sQuery(id+"F0.wireOp",EDGE,"E2.3.5.0");var subQ2=makeQuery(id+"F0.imprint","INTERSECT",VERTEX,{"disambiguationData":[OD(0.0)],"derivedFrom":[subQ1,subQ0]});Q58=makeQuery(id+"F0.imprint","IMPRINT",FACE,{"disambiguationData":[TD([[makeQuery(id+"F0.imprint","IMPRINT",EDGE,{"disambiguationData":[TD([[subQ2,1.0]])],"derivedFrom":subQ1}),-1.0]])]});}
            var Q59;
            {var subQ0=sQuery(id+"F0.wireOp",EDGE,"E2.3.3.0");var subQ1=sQuery(id+"F0.wireOp",EDGE,"E2.2.3.0");var subQ2=makeQuery(id+"F0.imprint","INTERSECT",VERTEX,{"disambiguationData":[OD(0.0)],"derivedFrom":[subQ1,subQ0]});Q59=makeQuery(id+"F0.imprint","IMPRINT",FACE,{"disambiguationData":[TD([[makeQuery(id+"F0.imprint","IMPRINT",EDGE,{"disambiguationData":[TD([[subQ2,1.0]])],"derivedFrom":subQ1}),-1.0]])]});}
            var Q60;
            {var subQ0=sQuery(id+"F0.wireOp",EDGE,"E2.1.5.0");var subQ1=sQuery(id+"F0.wireOp",EDGE,"E2.0.5.0");var subQ2=makeQuery(id+"F0.imprint","INTERSECT",VERTEX,{"disambiguationData":[OD(0.0)],"derivedFrom":[subQ1,subQ0]});Q60=makeQuery(id+"F0.imprint","IMPRINT",FACE,{"disambiguationData":[TD([[makeQuery(id+"F0.imprint","IMPRINT",EDGE,{"disambiguationData":[TD([[subQ2,1.0]])],"derivedFrom":subQ1}),1.0]])]});}
            var Q61;
            {var subQ0=sQuery(id+"F0.wireOp",EDGE,"E2.11.5.0");var subQ1=sQuery(id+"F0.wireOp",EDGE,"E2.10.5.0");var subQ2=makeQuery(id+"F0.imprint","INTERSECT",VERTEX,{"disambiguationData":[OD(0.0)],"derivedFrom":[subQ1,subQ0]});Q61=makeQuery(id+"F0.imprint","IMPRINT",FACE,{"disambiguationData":[TD([[makeQuery(id+"F0.imprint","IMPRINT",EDGE,{"disambiguationData":[TD([[subQ2,1.0]])],"derivedFrom":subQ1}),1.0]])]});}
            var Q62;
            {var subQ0=sQuery(id+"F0.wireOp",EDGE,"E2.11.1.0");var subQ1=sQuery(id+"F0.wireOp",EDGE,"E2.10.1.0");var subQ2=makeQuery(id+"F0.imprint","INTERSECT",VERTEX,{"disambiguationData":[OD(0.0)],"derivedFrom":[subQ1,subQ0]});Q62=makeQuery(id+"F0.imprint","IMPRINT",FACE,{"disambiguationData":[TD([[makeQuery(id+"F0.imprint","IMPRINT",EDGE,{"disambiguationData":[TD([[subQ2,1.0]])],"derivedFrom":subQ1}),1.0]])]});}
            var Q63;
            {var subQ0=sQuery(id+"F0.wireOp",EDGE,"E2.11.3.0");var subQ1=sQuery(id+"F0.wireOp",EDGE,"E2.10.3.0");var subQ2=makeQuery(id+"F0.imprint","INTERSECT",VERTEX,{"disambiguationData":[OD(0.0)],"derivedFrom":[subQ1,subQ0]});Q63=makeQuery(id+"F0.imprint","IMPRINT",FACE,{"disambiguationData":[TD([[makeQuery(id+"F0.imprint","IMPRINT",EDGE,{"disambiguationData":[TD([[subQ2,1.0]])],"derivedFrom":subQ1}),1.0]])]});}
            var Q64;
            {var subQ0=sQuery(id+"F0.wireOp",EDGE,"E2.6.1.0");var subQ1=sQuery(id+"F0.wireOp",EDGE,"E2.5.1.0");var subQ2=makeQuery(id+"F0.imprint","INTERSECT",VERTEX,{"disambiguationData":[OD(0.0)],"derivedFrom":[subQ1,subQ0]});Q64=makeQuery(id+"F0.imprint","IMPRINT",FACE,{"disambiguationData":[TD([[makeQuery(id+"F0.imprint","IMPRINT",EDGE,{"disambiguationData":[TD([[subQ2,1.0]])],"derivedFrom":subQ1}),1.0]])]});}
            var Q65;
            {var subQ0=sQuery(id+"F0.wireOp",EDGE,"E2.6.3.0");var subQ1=sQuery(id+"F0.wireOp",EDGE,"E2.5.3.0");var subQ2=makeQuery(id+"F0.imprint","INTERSECT",VERTEX,{"disambiguationData":[OD(0.0)],"derivedFrom":[subQ1,subQ0]});Q65=makeQuery(id+"F0.imprint","IMPRINT",FACE,{"disambiguationData":[TD([[makeQuery(id+"F0.imprint","IMPRINT",EDGE,{"disambiguationData":[TD([[subQ2,1.0]])],"derivedFrom":subQ1}),1.0]])]});}
            var Q66;
            {var subQ0=sQuery(id+"F0.wireOp",EDGE,"E2.6.5.0");var subQ1=sQuery(id+"F0.wireOp",EDGE,"E2.5.5.0");var subQ2=makeQuery(id+"F0.imprint","INTERSECT",VERTEX,{"disambiguationData":[OD(0.0)],"derivedFrom":[subQ1,subQ0]});Q66=makeQuery(id+"F0.imprint","IMPRINT",FACE,{"disambiguationData":[TD([[makeQuery(id+"F0.imprint","IMPRINT",EDGE,{"disambiguationData":[TD([[subQ2,1.0]])],"derivedFrom":subQ1}),1.0]])]});}
            var Q67;
            {var subQ0=sQuery(id+"F0.wireOp",EDGE,"E2.10.1.0");var subQ1=sQuery(id+"F0.wireOp",EDGE,"E2.10.0.0");var subQ2=makeQuery(id+"F0.imprint","INTERSECT",VERTEX,{"disambiguationData":[OD(0.0)],"derivedFrom":[subQ1,subQ0]});Q67=makeQuery(id+"F0.imprint","IMPRINT",FACE,{"disambiguationData":[TD([[makeQuery(id+"F0.imprint","IMPRINT",EDGE,{"disambiguationData":[TD([[subQ2,-1.0]])],"derivedFrom":subQ1}),-1.0]])]});}
            var Q68;
            {var subQ0=sQuery(id+"F0.wireOp",EDGE,"E2.5.1.0");var subQ1=sQuery(id+"F0.wireOp",EDGE,"E2.5.0.0");var subQ2=makeQuery(id+"F0.imprint","INTERSECT",VERTEX,{"disambiguationData":[OD(0.0)],"derivedFrom":[subQ1,subQ0]});Q68=makeQuery(id+"F0.imprint","IMPRINT",FACE,{"disambiguationData":[TD([[makeQuery(id+"F0.imprint","IMPRINT",EDGE,{"disambiguationData":[TD([[subQ2,-1.0]])],"derivedFrom":subQ1}),-1.0]])]});}
            var Q69;
            {var subQ0=sQuery(id+"F0.wireOp",EDGE,"E2.6.6.0");var subQ1=sQuery(id+"F0.wireOp",EDGE,"E2.5.6.0");var subQ2=makeQuery(id+"F0.imprint","INTERSECT",VERTEX,{"disambiguationData":[OD(0.0)],"derivedFrom":[subQ1,subQ0]});Q69=makeQuery(id+"F0.imprint","IMPRINT",FACE,{"disambiguationData":[TD([[makeQuery(id+"F0.imprint","IMPRINT",EDGE,{"disambiguationData":[TD([[subQ2,1.0]])],"derivedFrom":subQ1}),-1.0]])]});}
            var Q70;
            {var subQ0=sQuery(id+"F0.wireOp",EDGE,"E2.10.6.0");var subQ1=sQuery(id+"F0.wireOp",EDGE,"E2.9.6.0");var subQ2=makeQuery(id+"F0.imprint","INTERSECT",VERTEX,{"disambiguationData":[OD(0.0)],"derivedFrom":[subQ1,subQ0]});Q70=makeQuery(id+"F0.imprint","IMPRINT",FACE,{"disambiguationData":[TD([[makeQuery(id+"F0.imprint","IMPRINT",EDGE,{"disambiguationData":[TD([[subQ2,1.0]])],"derivedFrom":subQ1}),-1.0]])]});}
            var Q71;
            {var subQ0=sQuery(id+"F0.wireOp",EDGE,"E2.1.2.0");var subQ1=sQuery(id+"F0.wireOp",EDGE,"E2.0.2.0");var subQ2=makeQuery(id+"F0.imprint","INTERSECT",VERTEX,{"disambiguationData":[OD(0.0)],"derivedFrom":[subQ1,subQ0]});Q71=makeQuery(id+"F0.imprint","IMPRINT",FACE,{"disambiguationData":[TD([[makeQuery(id+"F0.imprint","IMPRINT",EDGE,{"disambiguationData":[TD([[subQ2,-1.0]])],"derivedFrom":subQ1}),-1.0]])]});}
            var Q72;
            {var subQ0=sQuery(id+"F0.wireOp",EDGE,"E2.7.4.1");var subQ1=sQuery(id+"F0.wireOp",EDGE,"E2.6.4.0");var subQ2=makeQuery(id+"F0.imprint","INTERSECT",VERTEX,{"derivedFrom":[subQ1,subQ0]});Q72=makeQuery(id+"F0.imprint","IMPRINT",FACE,{"disambiguationData":[TD([[makeQuery(id+"F0.imprint","IMPRINT",EDGE,{"disambiguationData":[TD([[subQ2,1.0]])],"derivedFrom":subQ1}),-1.0]])]});}
            var Q73;
            {var subQ0=sQuery(id+"F0.wireOp",EDGE,"E2.9.5.0");var subQ1=sQuery(id+"F0.wireOp",EDGE,"E2.9.4.0");var subQ2=makeQuery(id+"F0.imprint","INTERSECT",VERTEX,{"disambiguationData":[OD(0.0)],"derivedFrom":[subQ1,subQ0]});Q73=makeQuery(id+"F0.imprint","IMPRINT",FACE,{"disambiguationData":[TD([[makeQuery(id+"F0.imprint","IMPRINT",EDGE,{"disambiguationData":[TD([[subQ2,-1.0]])],"derivedFrom":subQ1}),-1.0]])]});}
            var Q74;
            {var subQ0=sQuery(id+"F0.wireOp",EDGE,"E2.9.0.0");var subQ1=sQuery(id+"F0.wireOp",EDGE,"E2.8.0.0");var subQ2=makeQuery(id+"F0.imprint","INTERSECT",VERTEX,{"disambiguationData":[OD(1.0)],"derivedFrom":[subQ1,subQ0]});Q74=makeQuery(id+"F0.imprint","IMPRINT",FACE,{"disambiguationData":[TD([[makeQuery(id+"F0.imprint","IMPRINT",EDGE,{"disambiguationData":[TD([[subQ2,-1.0]])],"derivedFrom":subQ1}),-1.0]])]});}
            var Q75;
            {var subQ0=sQuery(id+"F0.wireOp",EDGE,"E2.8.3.0");var subQ1=sQuery(id+"F0.wireOp",EDGE,"E2.8.2.0");var subQ2=makeQuery(id+"F0.imprint","INTERSECT",VERTEX,{"disambiguationData":[OD(0.0)],"derivedFrom":[subQ1,subQ0]});Q75=makeQuery(id+"F0.imprint","IMPRINT",FACE,{"disambiguationData":[TD([[makeQuery(id+"F0.imprint","IMPRINT",EDGE,{"disambiguationData":[TD([[subQ2,-1.0]])],"derivedFrom":subQ1}),-1.0]])]});}
            var Q76;
            {var subQ0=sQuery(id+"F0.wireOp",EDGE,"E2.8.5.0");var subQ1=sQuery(id+"F0.wireOp",EDGE,"E2.8.4.0");var subQ2=makeQuery(id+"F0.imprint","INTERSECT",VERTEX,{"disambiguationData":[OD(0.0)],"derivedFrom":[subQ1,subQ0]});Q76=makeQuery(id+"F0.imprint","IMPRINT",FACE,{"disambiguationData":[TD([[makeQuery(id+"F0.imprint","IMPRINT",EDGE,{"disambiguationData":[TD([[subQ2,-1.0]])],"derivedFrom":subQ1}),-1.0]])]});}
            var Q77;
            {var subQ0=sQuery(id+"F0.wireOp",EDGE,"E2.10.0.0");var subQ1=sQuery(id+"F0.wireOp",EDGE,"E2.9.0.0");var subQ2=makeQuery(id+"F0.imprint","INTERSECT",VERTEX,{"disambiguationData":[OD(1.0)],"derivedFrom":[subQ1,subQ0]});Q77=makeQuery(id+"F0.imprint","IMPRINT",FACE,{"disambiguationData":[TD([[makeQuery(id+"F0.imprint","IMPRINT",EDGE,{"disambiguationData":[TD([[subQ2,-1.0]])],"derivedFrom":subQ1}),-1.0]])]});}
            var Q78;
            {var subQ0=sQuery(id+"F0.wireOp",EDGE,"E2.7.3.0");var subQ1=sQuery(id+"F0.wireOp",EDGE,"E2.7.2.0");var subQ2=makeQuery(id+"F0.imprint","INTERSECT",VERTEX,{"disambiguationData":[OD(0.0)],"derivedFrom":[subQ1,subQ0]});Q78=makeQuery(id+"F0.imprint","IMPRINT",FACE,{"disambiguationData":[TD([[makeQuery(id+"F0.imprint","IMPRINT",EDGE,{"disambiguationData":[TD([[subQ2,-1.0]])],"derivedFrom":subQ1}),-1.0]])]});}
            var Q79;
            {var subQ0=sQuery(id+"F0.wireOp",EDGE,"E2.7.0.0");var subQ1=sQuery(id+"F0.wireOp",EDGE,"E2.6.0.0");var subQ2=makeQuery(id+"F0.imprint","INTERSECT",VERTEX,{"disambiguationData":[OD(1.0)],"derivedFrom":[subQ1,subQ0]});Q79=makeQuery(id+"F0.imprint","IMPRINT",FACE,{"disambiguationData":[TD([[makeQuery(id+"F0.imprint","IMPRINT",EDGE,{"disambiguationData":[TD([[subQ2,-1.0]])],"derivedFrom":subQ1}),-1.0]])]});}
            var Q80;
            {var subQ0=sQuery(id+"F0.wireOp",EDGE,"E2.8.0.0");var subQ1=sQuery(id+"F0.wireOp",EDGE,"E2.7.0.0");var subQ2=makeQuery(id+"F0.imprint","INTERSECT",VERTEX,{"disambiguationData":[OD(1.0)],"derivedFrom":[subQ1,subQ0]});Q80=makeQuery(id+"F0.imprint","IMPRINT",FACE,{"disambiguationData":[TD([[makeQuery(id+"F0.imprint","IMPRINT",EDGE,{"disambiguationData":[TD([[subQ2,-1.0]])],"derivedFrom":subQ1}),-1.0]])]});}
            var Q81;
            {var subQ0=sQuery(id+"F0.wireOp",EDGE,"E2.4.5.0");var subQ1=sQuery(id+"F0.wireOp",EDGE,"E2.4.4.0");var subQ2=makeQuery(id+"F0.imprint","INTERSECT",VERTEX,{"disambiguationData":[OD(0.0)],"derivedFrom":[subQ1,subQ0]});Q81=makeQuery(id+"F0.imprint","IMPRINT",FACE,{"disambiguationData":[TD([[makeQuery(id+"F0.imprint","IMPRINT",EDGE,{"disambiguationData":[TD([[subQ2,-1.0]])],"derivedFrom":subQ1}),-1.0]])]});}
            var Q82;
            {var subQ0=sQuery(id+"F0.wireOp",EDGE,"E2.6.0.0");var subQ1=sQuery(id+"F0.wireOp",EDGE,"E2.5.0.0");var subQ2=makeQuery(id+"F0.imprint","INTERSECT",VERTEX,{"disambiguationData":[OD(1.0)],"derivedFrom":[subQ1,subQ0]});Q82=makeQuery(id+"F0.imprint","IMPRINT",FACE,{"disambiguationData":[TD([[makeQuery(id+"F0.imprint","IMPRINT",EDGE,{"disambiguationData":[TD([[subQ2,-1.0]])],"derivedFrom":subQ1}),-1.0]])]});}
            var Q83;
            {var subQ0=sQuery(id+"F0.wireOp",EDGE,"E2.5.0.0");var subQ1=sQuery(id+"F0.wireOp",EDGE,"E2.4.0.0");var subQ2=makeQuery(id+"F0.imprint","INTERSECT",VERTEX,{"disambiguationData":[OD(1.0)],"derivedFrom":[subQ1,subQ0]});Q83=makeQuery(id+"F0.imprint","IMPRINT",FACE,{"disambiguationData":[TD([[makeQuery(id+"F0.imprint","IMPRINT",EDGE,{"disambiguationData":[TD([[subQ2,-1.0]])],"derivedFrom":subQ1}),-1.0]])]});}
            var Q84;
            {var subQ0=sQuery(id+"F0.wireOp",EDGE,"E2.4.3.0");var subQ1=sQuery(id+"F0.wireOp",EDGE,"E2.4.2.0");var subQ2=makeQuery(id+"F0.imprint","INTERSECT",VERTEX,{"disambiguationData":[OD(0.0)],"derivedFrom":[subQ1,subQ0]});Q84=makeQuery(id+"F0.imprint","IMPRINT",FACE,{"disambiguationData":[TD([[makeQuery(id+"F0.imprint","IMPRINT",EDGE,{"disambiguationData":[TD([[subQ2,-1.0]])],"derivedFrom":subQ1}),-1.0]])]});}
            var Q85;
            {var subQ0=sQuery(id+"F0.wireOp",EDGE,"E2.3.0.0");var subQ1=sQuery(id+"F0.wireOp",EDGE,"E2.2.0.0");var subQ2=makeQuery(id+"F0.imprint","INTERSECT",VERTEX,{"disambiguationData":[OD(1.0)],"derivedFrom":[subQ1,subQ0]});Q85=makeQuery(id+"F0.imprint","IMPRINT",FACE,{"disambiguationData":[TD([[makeQuery(id+"F0.imprint","IMPRINT",EDGE,{"disambiguationData":[TD([[subQ2,-1.0]])],"derivedFrom":subQ1}),-1.0]])]});}
            var Q86;
            {var subQ0=sQuery(id+"F0.wireOp",EDGE,"E2.2.3.0");var subQ1=sQuery(id+"F0.wireOp",EDGE,"E2.2.2.0");var subQ2=makeQuery(id+"F0.imprint","INTERSECT",VERTEX,{"disambiguationData":[OD(0.0)],"derivedFrom":[subQ1,subQ0]});Q86=makeQuery(id+"F0.imprint","IMPRINT",FACE,{"disambiguationData":[TD([[makeQuery(id+"F0.imprint","IMPRINT",EDGE,{"disambiguationData":[TD([[subQ2,-1.0]])],"derivedFrom":subQ1}),-1.0]])]});}
            var Q87;
            {var subQ0=sQuery(id+"F0.wireOp",EDGE,"E2.4.0.0");var subQ1=sQuery(id+"F0.wireOp",EDGE,"E2.3.0.0");var subQ2=makeQuery(id+"F0.imprint","INTERSECT",VERTEX,{"disambiguationData":[OD(1.0)],"derivedFrom":[subQ1,subQ0]});Q87=makeQuery(id+"F0.imprint","IMPRINT",FACE,{"disambiguationData":[TD([[makeQuery(id+"F0.imprint","IMPRINT",EDGE,{"disambiguationData":[TD([[subQ2,-1.0]])],"derivedFrom":subQ1}),-1.0]])]});}
            var Q88;
            {var subQ0=sQuery(id+"F0.wireOp",EDGE,"E2.1.4.0");var subQ1=sQuery(id+"F0.wireOp",EDGE,"E2.0.4.0");var subQ2=makeQuery(id+"F0.imprint","INTERSECT",VERTEX,{"disambiguationData":[OD(0.0)],"derivedFrom":[subQ1,subQ0]});Q88=makeQuery(id+"F0.imprint","IMPRINT",FACE,{"disambiguationData":[TD([[makeQuery(id+"F0.imprint","IMPRINT",EDGE,{"disambiguationData":[TD([[subQ2,-1.0]])],"derivedFrom":subQ1}),-1.0]])]});}
            var Q89;
            {var subQ0=sQuery(id+"F0.wireOp",EDGE,"E2.2.0.0");var subQ1=sQuery(id+"F0.wireOp",EDGE,"E2.1.0.0");var subQ2=makeQuery(id+"F0.imprint","INTERSECT",VERTEX,{"disambiguationData":[OD(1.0)],"derivedFrom":[subQ1,subQ0]});Q89=makeQuery(id+"F0.imprint","IMPRINT",FACE,{"disambiguationData":[TD([[makeQuery(id+"F0.imprint","IMPRINT",EDGE,{"disambiguationData":[TD([[subQ2,-1.0]])],"derivedFrom":subQ1}),-1.0]])]});}
            var Q90;
            {var subQ0=sQuery(id+"F0.wireOp",EDGE,"E2.6.0.0");var subQ1=sQuery(id+"F0.wireOp",EDGE,"E2.5.0.0");var subQ2=makeQuery(id+"F0.imprint","INTERSECT",VERTEX,{"disambiguationData":[OD(0.0)],"derivedFrom":[subQ1,subQ0]});Q90=makeQuery(id+"F0.imprint","IMPRINT",FACE,{"disambiguationData":[TD([[makeQuery(id+"F0.imprint","IMPRINT",EDGE,{"disambiguationData":[TD([[subQ2,-1.0]])],"derivedFrom":subQ1}),-1.0]])]});}
            var Q91;
            {var subQ0=sQuery(id+"F0.wireOp",EDGE,"E2.10.0.0");var subQ1=sQuery(id+"F0.wireOp",EDGE,"E2.9.0.0");var subQ2=makeQuery(id+"F0.imprint","INTERSECT",VERTEX,{"disambiguationData":[OD(0.0)],"derivedFrom":[subQ1,subQ0]});Q91=makeQuery(id+"F0.imprint","IMPRINT",FACE,{"disambiguationData":[TD([[makeQuery(id+"F0.imprint","IMPRINT",EDGE,{"disambiguationData":[TD([[subQ2,-1.0]])],"derivedFrom":subQ1}),-1.0]])]});}
            var Q92;
            {var subQ0=sQuery(id+"F0.wireOp",EDGE,"E2.7.0.0");var subQ1=sQuery(id+"F0.wireOp",EDGE,"E2.6.0.0");var subQ2=makeQuery(id+"F0.imprint","INTERSECT",VERTEX,{"disambiguationData":[OD(1.0)],"derivedFrom":[subQ1,subQ0]});Q92=makeQuery(id+"F0.imprint","IMPRINT",FACE,{"disambiguationData":[TD([[makeQuery(id+"F0.imprint","IMPRINT",EDGE,{"disambiguationData":[TD([[subQ2,-1.0]])],"derivedFrom":subQ1}),1.0]])]});}
            var Q93;
            {var subQ0=sQuery(id+"F0.wireOp",EDGE,"E2.3.0.0");var subQ1=sQuery(id+"F0.wireOp",EDGE,"E2.2.0.0");var subQ2=makeQuery(id+"F0.imprint","INTERSECT",VERTEX,{"disambiguationData":[OD(1.0)],"derivedFrom":[subQ1,subQ0]});Q93=makeQuery(id+"F0.imprint","IMPRINT",FACE,{"disambiguationData":[TD([[makeQuery(id+"F0.imprint","IMPRINT",EDGE,{"disambiguationData":[TD([[subQ2,-1.0]])],"derivedFrom":subQ1}),1.0]])]});}
            var Q94;
            {var subQ0=sQuery(id+"F0.wireOp",EDGE,"E2.11.5.0");var subQ1=sQuery(id+"F0.wireOp",EDGE,"E2.11.4.0");var subQ2=makeQuery(id+"F0.imprint","INTERSECT",VERTEX,{"disambiguationData":[OD(0.0)],"derivedFrom":[subQ1,subQ0]});Q94=makeQuery(id+"F0.imprint","IMPRINT",FACE,{"disambiguationData":[TD([[makeQuery(id+"F0.imprint","IMPRINT",EDGE,{"disambiguationData":[TD([[subQ2,-1.0]])],"derivedFrom":subQ1}),-1.0]])]});}
            var Q95;
            {var subQ0=sQuery(id+"F0.wireOp",EDGE,"E2.1.2.0");var subQ1=sQuery(id+"F0.wireOp",EDGE,"E2.0.2.0");var subQ2=makeQuery(id+"F0.imprint","INTERSECT",VERTEX,{"disambiguationData":[OD(0.0)],"derivedFrom":[subQ1,subQ0]});Q95=makeQuery(id+"F0.imprint","IMPRINT",FACE,{"disambiguationData":[TD([[makeQuery(id+"F0.imprint","IMPRINT",EDGE,{"disambiguationData":[TD([[subQ2,1.0]])],"derivedFrom":subQ1}),1.0]])]});}
            var Q96;
            {var subQ0=sQuery(id+"F0.wireOp",EDGE,"E2.1.6.0");var subQ1=sQuery(id+"F0.wireOp",EDGE,"E2.0.6.0");var subQ2=makeQuery(id+"F0.imprint","INTERSECT",VERTEX,{"disambiguationData":[OD(0.0)],"derivedFrom":[subQ1,subQ0]});Q96=makeQuery(id+"F0.imprint","IMPRINT",FACE,{"disambiguationData":[TD([[makeQuery(id+"F0.imprint","IMPRINT",EDGE,{"disambiguationData":[TD([[subQ2,1.0]])],"derivedFrom":subQ1}),-1.0]])]});}
            var Q97;
            {var subQ0=sQuery(id+"F0.wireOp",EDGE,"E2.9.0.0");var subQ1=sQuery(id+"F0.wireOp",EDGE,"E2.8.0.0");var subQ2=makeQuery(id+"F0.imprint","INTERSECT",VERTEX,{"disambiguationData":[OD(1.0)],"derivedFrom":[subQ1,subQ0]});Q97=makeQuery(id+"F0.imprint","IMPRINT",FACE,{"disambiguationData":[TD([[makeQuery(id+"F0.imprint","IMPRINT",EDGE,{"disambiguationData":[TD([[subQ2,1.0]])],"derivedFrom":subQ1}),-1.0]])]});}
            var Q98;
            {var subQ0=sQuery(id+"F0.wireOp",EDGE,"E2.9.2.0");var subQ1=sQuery(id+"F0.wireOp",EDGE,"E2.8.2.0");var subQ2=makeQuery(id+"F0.imprint","INTERSECT",VERTEX,{"disambiguationData":[OD(0.0)],"derivedFrom":[subQ1,subQ0]});Q98=makeQuery(id+"F0.imprint","IMPRINT",FACE,{"disambiguationData":[TD([[makeQuery(id+"F0.imprint","IMPRINT",EDGE,{"disambiguationData":[TD([[subQ2,-1.0]])],"derivedFrom":subQ1}),-1.0]])]});}
            var Q99;
            {var subQ0=sQuery(id+"F0.wireOp",EDGE,"E2.9.4.0");var subQ1=sQuery(id+"F0.wireOp",EDGE,"E2.8.4.0");var subQ2=makeQuery(id+"F0.imprint","INTERSECT",VERTEX,{"disambiguationData":[OD(0.0)],"derivedFrom":[subQ1,subQ0]});Q99=makeQuery(id+"F0.imprint","IMPRINT",FACE,{"disambiguationData":[TD([[makeQuery(id+"F0.imprint","IMPRINT",EDGE,{"disambiguationData":[TD([[subQ2,-1.0]])],"derivedFrom":subQ1}),-1.0]])]});}
            var Q100;
            {var subQ0=sQuery(id+"F0.wireOp",EDGE,"E2.10.0.0");var subQ1=sQuery(id+"F0.wireOp",EDGE,"E2.9.0.0");var subQ2=makeQuery(id+"F0.imprint","INTERSECT",VERTEX,{"disambiguationData":[OD(1.0)],"derivedFrom":[subQ1,subQ0]});Q100=makeQuery(id+"F0.imprint","IMPRINT",FACE,{"disambiguationData":[TD([[makeQuery(id+"F0.imprint","IMPRINT",EDGE,{"disambiguationData":[TD([[subQ2,1.0]])],"derivedFrom":subQ1}),-1.0]])]});}
            var Q101;
            {var subQ0=sQuery(id+"F0.wireOp",EDGE,"E2.8.2.0");var subQ1=sQuery(id+"F0.wireOp",EDGE,"E2.7.2.0");var subQ2=makeQuery(id+"F0.imprint","INTERSECT",VERTEX,{"disambiguationData":[OD(0.0)],"derivedFrom":[subQ1,subQ0]});Q101=makeQuery(id+"F0.imprint","IMPRINT",FACE,{"disambiguationData":[TD([[makeQuery(id+"F0.imprint","IMPRINT",EDGE,{"disambiguationData":[TD([[subQ2,-1.0]])],"derivedFrom":subQ1}),-1.0]])]});}
            var Q102;
            {var subQ0=sQuery(id+"F0.wireOp",EDGE,"E2.8.4.0");var subQ1=sQuery(id+"F0.wireOp",EDGE,"E2.7.4.0");var subQ2=makeQuery(id+"F0.imprint","INTERSECT",VERTEX,{"disambiguationData":[OD(0.0)],"derivedFrom":[subQ1,subQ0]});Q102=makeQuery(id+"F0.imprint","IMPRINT",FACE,{"disambiguationData":[TD([[makeQuery(id+"F0.imprint","IMPRINT",EDGE,{"disambiguationData":[TD([[subQ2,-1.0]])],"derivedFrom":subQ1}),-1.0]])]});}
            var Q103;
            {var subQ0=sQuery(id+"F0.wireOp",EDGE,"E2.7.2.0");var subQ1=sQuery(id+"F0.wireOp",EDGE,"E2.6.2.0");var subQ2=makeQuery(id+"F0.imprint","INTERSECT",VERTEX,{"disambiguationData":[OD(0.0)],"derivedFrom":[subQ1,subQ0]});Q103=makeQuery(id+"F0.imprint","IMPRINT",FACE,{"disambiguationData":[TD([[makeQuery(id+"F0.imprint","IMPRINT",EDGE,{"disambiguationData":[TD([[subQ2,-1.0]])],"derivedFrom":subQ1}),-1.0]])]});}
            var Q104;
            {var subQ0=sQuery(id+"F0.wireOp",EDGE,"E2.7.4.0");var subQ1=sQuery(id+"F0.wireOp",EDGE,"E2.6.4.0");var subQ2=makeQuery(id+"F0.imprint","INTERSECT",VERTEX,{"disambiguationData":[OD(0.0)],"derivedFrom":[subQ1,subQ0]});Q104=makeQuery(id+"F0.imprint","IMPRINT",FACE,{"disambiguationData":[TD([[makeQuery(id+"F0.imprint","IMPRINT",EDGE,{"disambiguationData":[TD([[subQ2,-1.0]])],"derivedFrom":subQ1}),-1.0]])]});}
            var Q105;
            {var subQ0=sQuery(id+"F0.wireOp",EDGE,"E2.5.4.0");var subQ1=sQuery(id+"F0.wireOp",EDGE,"E2.4.4.0");var subQ2=makeQuery(id+"F0.imprint","INTERSECT",VERTEX,{"disambiguationData":[OD(0.0)],"derivedFrom":[subQ1,subQ0]});Q105=makeQuery(id+"F0.imprint","IMPRINT",FACE,{"disambiguationData":[TD([[makeQuery(id+"F0.imprint","IMPRINT",EDGE,{"disambiguationData":[TD([[subQ2,-1.0]])],"derivedFrom":subQ1}),-1.0]])]});}
            var Q106;
            {var subQ0=sQuery(id+"F0.wireOp",EDGE,"E2.6.2.0");var subQ1=sQuery(id+"F0.wireOp",EDGE,"E2.5.2.0");var subQ2=makeQuery(id+"F0.imprint","INTERSECT",VERTEX,{"disambiguationData":[OD(0.0)],"derivedFrom":[subQ1,subQ0]});Q106=makeQuery(id+"F0.imprint","IMPRINT",FACE,{"disambiguationData":[TD([[makeQuery(id+"F0.imprint","IMPRINT",EDGE,{"disambiguationData":[TD([[subQ2,-1.0]])],"derivedFrom":subQ1}),-1.0]])]});}
            var Q107;
            {var subQ0=sQuery(id+"F0.wireOp",EDGE,"E2.6.4.0");var subQ1=sQuery(id+"F0.wireOp",EDGE,"E2.5.4.0");var subQ2=makeQuery(id+"F0.imprint","INTERSECT",VERTEX,{"disambiguationData":[OD(0.0)],"derivedFrom":[subQ1,subQ0]});Q107=makeQuery(id+"F0.imprint","IMPRINT",FACE,{"disambiguationData":[TD([[makeQuery(id+"F0.imprint","IMPRINT",EDGE,{"disambiguationData":[TD([[subQ2,-1.0]])],"derivedFrom":subQ1}),-1.0]])]});}
            var Q108;
            {var subQ0=sQuery(id+"F0.wireOp",EDGE,"E2.4.2.0");var subQ1=sQuery(id+"F0.wireOp",EDGE,"E2.3.2.0");var subQ2=makeQuery(id+"F0.imprint","INTERSECT",VERTEX,{"disambiguationData":[OD(0.0)],"derivedFrom":[subQ1,subQ0]});Q108=makeQuery(id+"F0.imprint","IMPRINT",FACE,{"disambiguationData":[TD([[makeQuery(id+"F0.imprint","IMPRINT",EDGE,{"disambiguationData":[TD([[subQ2,-1.0]])],"derivedFrom":subQ1}),-1.0]])]});}
            var Q109;
            {var subQ0=sQuery(id+"F0.wireOp",EDGE,"E2.4.4.0");var subQ1=sQuery(id+"F0.wireOp",EDGE,"E2.3.4.0");var subQ2=makeQuery(id+"F0.imprint","INTERSECT",VERTEX,{"disambiguationData":[OD(0.0)],"derivedFrom":[subQ1,subQ0]});Q109=makeQuery(id+"F0.imprint","IMPRINT",FACE,{"disambiguationData":[TD([[makeQuery(id+"F0.imprint","IMPRINT",EDGE,{"disambiguationData":[TD([[subQ2,-1.0]])],"derivedFrom":subQ1}),-1.0]])]});}
            var Q110;
            {var subQ0=sQuery(id+"F0.wireOp",EDGE,"E2.5.0.0");var subQ1=sQuery(id+"F0.wireOp",EDGE,"E2.4.0.0");var subQ2=makeQuery(id+"F0.imprint","INTERSECT",VERTEX,{"disambiguationData":[OD(1.0)],"derivedFrom":[subQ1,subQ0]});Q110=makeQuery(id+"F0.imprint","IMPRINT",FACE,{"disambiguationData":[TD([[makeQuery(id+"F0.imprint","IMPRINT",EDGE,{"disambiguationData":[TD([[subQ2,1.0]])],"derivedFrom":subQ1}),-1.0]])]});}
            var Q111;
            {var subQ0=sQuery(id+"F0.wireOp",EDGE,"E2.5.2.0");var subQ1=sQuery(id+"F0.wireOp",EDGE,"E2.4.2.0");var subQ2=makeQuery(id+"F0.imprint","INTERSECT",VERTEX,{"disambiguationData":[OD(0.0)],"derivedFrom":[subQ1,subQ0]});Q111=makeQuery(id+"F0.imprint","IMPRINT",FACE,{"disambiguationData":[TD([[makeQuery(id+"F0.imprint","IMPRINT",EDGE,{"disambiguationData":[TD([[subQ2,-1.0]])],"derivedFrom":subQ1}),-1.0]])]});}
            var Q112;
            {var subQ0=sQuery(id+"F0.wireOp",EDGE,"E2.3.2.0");var subQ1=sQuery(id+"F0.wireOp",EDGE,"E2.2.2.0");var subQ2=makeQuery(id+"F0.imprint","INTERSECT",VERTEX,{"disambiguationData":[OD(0.0)],"derivedFrom":[subQ1,subQ0]});Q112=makeQuery(id+"F0.imprint","IMPRINT",FACE,{"disambiguationData":[TD([[makeQuery(id+"F0.imprint","IMPRINT",EDGE,{"disambiguationData":[TD([[subQ2,-1.0]])],"derivedFrom":subQ1}),-1.0]])]});}
            var Q113;
            {var subQ0=sQuery(id+"F0.wireOp",EDGE,"E2.3.4.0");var subQ1=sQuery(id+"F0.wireOp",EDGE,"E2.2.4.0");var subQ2=makeQuery(id+"F0.imprint","INTERSECT",VERTEX,{"disambiguationData":[OD(0.0)],"derivedFrom":[subQ1,subQ0]});Q113=makeQuery(id+"F0.imprint","IMPRINT",FACE,{"disambiguationData":[TD([[makeQuery(id+"F0.imprint","IMPRINT",EDGE,{"disambiguationData":[TD([[subQ2,-1.0]])],"derivedFrom":subQ1}),-1.0]])]});}
            var Q114;
            {var subQ0=sQuery(id+"F0.wireOp",EDGE,"E2.2.2.0");var subQ1=sQuery(id+"F0.wireOp",EDGE,"E2.1.2.0");var subQ2=makeQuery(id+"F0.imprint","INTERSECT",VERTEX,{"disambiguationData":[OD(0.0)],"derivedFrom":[subQ1,subQ0]});Q114=makeQuery(id+"F0.imprint","IMPRINT",FACE,{"disambiguationData":[TD([[makeQuery(id+"F0.imprint","IMPRINT",EDGE,{"disambiguationData":[TD([[subQ2,-1.0]])],"derivedFrom":subQ1}),-1.0]])]});}
            var Q115;
            {var subQ0=sQuery(id+"F0.wireOp",EDGE,"E2.2.4.0");var subQ1=sQuery(id+"F0.wireOp",EDGE,"E2.1.4.0");var subQ2=makeQuery(id+"F0.imprint","INTERSECT",VERTEX,{"disambiguationData":[OD(0.0)],"derivedFrom":[subQ1,subQ0]});Q115=makeQuery(id+"F0.imprint","IMPRINT",FACE,{"disambiguationData":[TD([[makeQuery(id+"F0.imprint","IMPRINT",EDGE,{"disambiguationData":[TD([[subQ2,-1.0]])],"derivedFrom":subQ1}),-1.0]])]});}
            var Q116;
            {var subQ0=sQuery(id+"F0.wireOp",EDGE,"E2.11.4.0");var subQ1=sQuery(id+"F0.wireOp",EDGE,"E2.10.4.0");var subQ2=makeQuery(id+"F0.imprint","INTERSECT",VERTEX,{"disambiguationData":[OD(0.0)],"derivedFrom":[subQ1,subQ0]});Q116=makeQuery(id+"F0.imprint","IMPRINT",FACE,{"disambiguationData":[TD([[makeQuery(id+"F0.imprint","IMPRINT",EDGE,{"disambiguationData":[TD([[subQ2,-1.0]])],"derivedFrom":subQ1}),-1.0]])]});}
            var Q117;
            {var subQ0=sQuery(id+"F0.wireOp",EDGE,"E2.10.2.0");var subQ1=sQuery(id+"F0.wireOp",EDGE,"E2.9.2.0");var subQ2=makeQuery(id+"F0.imprint","INTERSECT",VERTEX,{"disambiguationData":[OD(0.0)],"derivedFrom":[subQ1,subQ0]});Q117=makeQuery(id+"F0.imprint","IMPRINT",FACE,{"disambiguationData":[TD([[makeQuery(id+"F0.imprint","IMPRINT",EDGE,{"disambiguationData":[TD([[subQ2,-1.0]])],"derivedFrom":subQ1}),-1.0]])]});}
            var Q118;
            {var subQ0=sQuery(id+"F0.wireOp",EDGE,"E2.10.4.0");var subQ1=sQuery(id+"F0.wireOp",EDGE,"E2.9.4.0");var subQ2=makeQuery(id+"F0.imprint","INTERSECT",VERTEX,{"disambiguationData":[OD(0.0)],"derivedFrom":[subQ1,subQ0]});Q118=makeQuery(id+"F0.imprint","IMPRINT",FACE,{"disambiguationData":[TD([[makeQuery(id+"F0.imprint","IMPRINT",EDGE,{"disambiguationData":[TD([[subQ2,-1.0]])],"derivedFrom":subQ1}),-1.0]])]});}
            var Q119;
            {var subQ0=sQuery(id+"F0.wireOp",EDGE,"E2.11.2.0");var subQ1=sQuery(id+"F0.wireOp",EDGE,"E2.10.2.0");var subQ2=makeQuery(id+"F0.imprint","INTERSECT",VERTEX,{"disambiguationData":[OD(0.0)],"derivedFrom":[subQ1,subQ0]});Q119=makeQuery(id+"F0.imprint","IMPRINT",FACE,{"disambiguationData":[TD([[makeQuery(id+"F0.imprint","IMPRINT",EDGE,{"disambiguationData":[TD([[subQ2,-1.0]])],"derivedFrom":subQ1}),-1.0]])]});}
            var Q120;
            {var subQ0=sQuery(id+"F0.wireOp",EDGE,"E2.5.6.0");var subQ1=sQuery(id+"F0.wireOp",EDGE,"E2.4.6.0");var subQ2=makeQuery(id+"F0.imprint","INTERSECT",VERTEX,{"disambiguationData":[OD(0.0)],"derivedFrom":[subQ1,subQ0]});Q120=makeQuery(id+"F0.imprint","IMPRINT",FACE,{"disambiguationData":[TD([[makeQuery(id+"F0.imprint","IMPRINT",EDGE,{"disambiguationData":[TD([[subQ2,1.0]])],"derivedFrom":subQ1}),-1.0]])]});}
            var Q121;
            {var subQ0=sQuery(id+"F0.wireOp",EDGE,"E2.7.4.0");var subQ1=sQuery(id+"F0.wireOp",EDGE,"E2.6.4.0");var subQ2=makeQuery(id+"F0.imprint","INTERSECT",VERTEX,{"disambiguationData":[OD(0.0)],"derivedFrom":[subQ1,subQ0]});Q121=makeQuery(id+"F0.imprint","IMPRINT",FACE,{"disambiguationData":[TD([[makeQuery(id+"F0.imprint","IMPRINT",EDGE,{"disambiguationData":[TD([[subQ2,1.0]])],"derivedFrom":subQ1}),-1.0]])]});}
            var Q122;
            {var subQ0=sQuery(id+"F0.wireOp",EDGE,"E2.5.0.0");var subQ1=sQuery(id+"F0.wireOp",EDGE,"E2.4.0.0");var subQ2=makeQuery(id+"F0.imprint","INTERSECT",VERTEX,{"disambiguationData":[OD(0.0)],"derivedFrom":[subQ1,subQ0]});Q122=makeQuery(id+"F0.imprint","IMPRINT",FACE,{"disambiguationData":[TD([[makeQuery(id+"F0.imprint","IMPRINT",EDGE,{"disambiguationData":[TD([[subQ2,-1.0]])],"derivedFrom":subQ1}),-1.0]])]});}
            var Q123;
            {var subQ0=sQuery(id+"F0.wireOp",EDGE,"E2.11.4.0");var subQ1=sQuery(id+"F0.wireOp",EDGE,"E2.10.4.0");var subQ2=makeQuery(id+"F0.imprint","INTERSECT",VERTEX,{"disambiguationData":[OD(0.0)],"derivedFrom":[subQ1,subQ0]});Q123=makeQuery(id+"F0.imprint","IMPRINT",FACE,{"disambiguationData":[TD([[makeQuery(id+"F0.imprint","IMPRINT",EDGE,{"disambiguationData":[TD([[subQ2,1.0]])],"derivedFrom":subQ1}),1.0]])]});}
            var Q124;
            {var subQ0=sQuery(id+"F0.wireOp",EDGE,"E2.11.6.0");var subQ1=sQuery(id+"F0.wireOp",EDGE,"E2.10.6.0");var subQ2=makeQuery(id+"F0.imprint","INTERSECT",VERTEX,{"disambiguationData":[OD(0.0)],"derivedFrom":[subQ1,subQ0]});Q124=makeQuery(id+"F0.imprint","IMPRINT",FACE,{"disambiguationData":[TD([[makeQuery(id+"F0.imprint","IMPRINT",EDGE,{"disambiguationData":[TD([[subQ2,1.0]])],"derivedFrom":subQ1}),1.0]])]});}
            var Q125;
            {var subQ0=sQuery(id+"F0.wireOp",EDGE,"E2.11.2.0");var subQ1=sQuery(id+"F0.wireOp",EDGE,"E2.10.2.0");var subQ2=makeQuery(id+"F0.imprint","INTERSECT",VERTEX,{"disambiguationData":[OD(0.0)],"derivedFrom":[subQ1,subQ0]});Q125=makeQuery(id+"F0.imprint","IMPRINT",FACE,{"disambiguationData":[TD([[makeQuery(id+"F0.imprint","IMPRINT",EDGE,{"disambiguationData":[TD([[subQ2,1.0]])],"derivedFrom":subQ1}),1.0]])]});}
            var Q126;
            {var subQ0=sQuery(id+"F0.wireOp",EDGE,"E2.6.6.0");var subQ1=sQuery(id+"F0.wireOp",EDGE,"E2.5.6.0");var subQ2=makeQuery(id+"F0.imprint","INTERSECT",VERTEX,{"disambiguationData":[OD(0.0)],"derivedFrom":[subQ1,subQ0]});Q126=makeQuery(id+"F0.imprint","IMPRINT",FACE,{"disambiguationData":[TD([[makeQuery(id+"F0.imprint","IMPRINT",EDGE,{"disambiguationData":[TD([[subQ2,1.0]])],"derivedFrom":subQ1}),1.0]])]});}
            var Q127;
            {var subQ0=sQuery(id+"F0.wireOp",EDGE,"E2.6.2.0");var subQ1=sQuery(id+"F0.wireOp",EDGE,"E2.5.2.0");var subQ2=makeQuery(id+"F0.imprint","INTERSECT",VERTEX,{"disambiguationData":[OD(0.0)],"derivedFrom":[subQ1,subQ0]});Q127=makeQuery(id+"F0.imprint","IMPRINT",FACE,{"disambiguationData":[TD([[makeQuery(id+"F0.imprint","IMPRINT",EDGE,{"disambiguationData":[TD([[subQ2,1.0]])],"derivedFrom":subQ1}),1.0]])]});}
            var Q128;
            {var subQ0=sQuery(id+"F0.wireOp",EDGE,"E2.6.4.0");var subQ1=sQuery(id+"F0.wireOp",EDGE,"E2.5.4.0");var subQ2=makeQuery(id+"F0.imprint","INTERSECT",VERTEX,{"disambiguationData":[OD(0.0)],"derivedFrom":[subQ1,subQ0]});Q128=makeQuery(id+"F0.imprint","IMPRINT",FACE,{"disambiguationData":[TD([[makeQuery(id+"F0.imprint","IMPRINT",EDGE,{"disambiguationData":[TD([[subQ2,1.0]])],"derivedFrom":subQ1}),1.0]])]});}
            var Q129;
            {var subQ0=sQuery(id+"F0.wireOp",EDGE,"E2.1.6.0");var subQ1=sQuery(id+"F0.wireOp",EDGE,"E2.0.6.0");var subQ2=makeQuery(id+"F0.imprint","INTERSECT",VERTEX,{"disambiguationData":[OD(0.0)],"derivedFrom":[subQ1,subQ0]});Q129=makeQuery(id+"F0.imprint","IMPRINT",FACE,{"disambiguationData":[TD([[makeQuery(id+"F0.imprint","IMPRINT",EDGE,{"disambiguationData":[TD([[subQ2,1.0]])],"derivedFrom":subQ1}),1.0]])]});}
            var Q130;
            {var subQ0=sQuery(id+"F0.wireOp",EDGE,"E2.1.1.0");var subQ1=sQuery(id+"F0.wireOp",EDGE,"E2.0.1.0");var subQ2=makeQuery(id+"F0.imprint","INTERSECT",VERTEX,{"disambiguationData":[OD(0.0)],"derivedFrom":[subQ1,subQ0]});Q130=makeQuery(id+"F0.imprint","IMPRINT",FACE,{"disambiguationData":[TD([[makeQuery(id+"F0.imprint","IMPRINT",EDGE,{"disambiguationData":[TD([[subQ2,-1.0]])],"derivedFrom":subQ1}),-1.0]])]});}
            var Q131;
            {var subQ0=sQuery(id+"F0.wireOp",EDGE,"E2.1.4.0");var subQ1=sQuery(id+"F0.wireOp",EDGE,"E2.0.4.0");var subQ2=makeQuery(id+"F0.imprint","INTERSECT",VERTEX,{"disambiguationData":[OD(0.0)],"derivedFrom":[subQ1,subQ0]});Q131=makeQuery(id+"F0.imprint","IMPRINT",FACE,{"disambiguationData":[TD([[makeQuery(id+"F0.imprint","IMPRINT",EDGE,{"disambiguationData":[TD([[subQ2,1.0]])],"derivedFrom":subQ1}),1.0]])]});}
            var Q132;
            {var subQ0=sQuery(id+"F0.wireOp",EDGE,"E2.10.4.0");var subQ1=sQuery(id+"F0.wireOp",EDGE,"E2.9.4.0");var subQ2=makeQuery(id+"F0.imprint","INTERSECT",VERTEX,{"disambiguationData":[OD(0.0)],"derivedFrom":[subQ1,subQ0]});Q132=makeQuery(id+"F0.imprint","IMPRINT",FACE,{"disambiguationData":[TD([[makeQuery(id+"F0.imprint","IMPRINT",EDGE,{"disambiguationData":[TD([[subQ2,-1.0]])],"derivedFrom":subQ1}),1.0]])]});}
            var Q133;
            {var subQ0=sQuery(id+"F0.wireOp",EDGE,"E2.11.0.0");var subQ1=sQuery(id+"F0.wireOp",EDGE,"E2.10.0.0");var subQ2=makeQuery(id+"F0.imprint","INTERSECT",VERTEX,{"disambiguationData":[OD(1.0)],"derivedFrom":[subQ1,subQ0]});Q133=makeQuery(id+"F0.imprint","IMPRINT",FACE,{"disambiguationData":[TD([[makeQuery(id+"F0.imprint","IMPRINT",EDGE,{"disambiguationData":[TD([[subQ2,1.0]])],"derivedFrom":subQ1}),1.0]])]});}
            var Q134;
            {var subQ0=sQuery(id+"F0.wireOp",EDGE,"E2.6.0.0");var subQ1=sQuery(id+"F0.wireOp",EDGE,"E2.5.0.0");var subQ2=makeQuery(id+"F0.imprint","INTERSECT",VERTEX,{"disambiguationData":[OD(1.0)],"derivedFrom":[subQ1,subQ0]});Q134=makeQuery(id+"F0.imprint","IMPRINT",FACE,{"disambiguationData":[TD([[makeQuery(id+"F0.imprint","IMPRINT",EDGE,{"disambiguationData":[TD([[subQ2,1.0]])],"derivedFrom":subQ1}),1.0]])]});}
            var Q135;
            {var subQ0=sQuery(id+"F0.wireOp",EDGE,"E2.1.4.0");var subQ1=sQuery(id+"F0.wireOp",EDGE,"E2.1.3.0");var subQ2=makeQuery(id+"F0.imprint","INTERSECT",VERTEX,{"disambiguationData":[OD(0.0)],"derivedFrom":[subQ1,subQ0]});Q135=makeQuery(id+"F0.imprint","IMPRINT",FACE,{"disambiguationData":[TD([[makeQuery(id+"F0.imprint","IMPRINT",EDGE,{"disambiguationData":[TD([[subQ2,-1.0]])],"derivedFrom":subQ1}),1.0]])]});}
            var Q136;
            {var subQ0=sQuery(id+"F0.wireOp",EDGE,"E2.1.1.0");var subQ1=sQuery(id+"F0.wireOp",EDGE,"E2.0.1.0");var subQ2=makeQuery(id+"F0.imprint","INTERSECT",VERTEX,{"disambiguationData":[OD(0.0)],"derivedFrom":[subQ1,subQ0]});Q136=makeQuery(id+"F0.imprint","IMPRINT",FACE,{"disambiguationData":[TD([[makeQuery(id+"F0.imprint","IMPRINT",EDGE,{"disambiguationData":[TD([[subQ2,-1.0]])],"derivedFrom":subQ1}),1.0]])]});}
            var Q137;
            {var subQ0=sQuery(id+"F0.wireOp",EDGE,"E2.4.6.0");var subQ1=sQuery(id+"F0.wireOp",EDGE,"E2.3.6.0");var subQ2=makeQuery(id+"F0.imprint","INTERSECT",VERTEX,{"disambiguationData":[OD(0.0)],"derivedFrom":[subQ1,subQ0]});Q137=makeQuery(id+"F0.imprint","IMPRINT",FACE,{"disambiguationData":[TD([[makeQuery(id+"F0.imprint","IMPRINT",EDGE,{"disambiguationData":[TD([[subQ2,1.0]])],"derivedFrom":subQ1}),-1.0]])]});}
            var Q138;
            {var subQ0=sQuery(id+"F0.wireOp",EDGE,"E2.7.3.1");var subQ1=sQuery(id+"F0.wireOp",EDGE,"E2.6.3.0");var subQ2=makeQuery(id+"F0.imprint","INTERSECT",VERTEX,{"derivedFrom":[subQ1,subQ0]});Q138=makeQuery(id+"F0.imprint","IMPRINT",FACE,{"disambiguationData":[TD([[makeQuery(id+"F0.imprint","IMPRINT",EDGE,{"disambiguationData":[TD([[subQ2,1.0]])],"derivedFrom":subQ1}),-1.0]])]});}
            var Q139;
            {var subQ0=sQuery(id+"F0.wireOp",EDGE,"E2.6.1.1");var subQ1=sQuery(id+"F0.wireOp",EDGE,"E2.5.1.0");var subQ2=makeQuery(id+"F0.imprint","INTERSECT",VERTEX,{"derivedFrom":[subQ1,subQ0]});Q139=makeQuery(id+"F0.imprint","IMPRINT",FACE,{"disambiguationData":[TD([[makeQuery(id+"F0.imprint","IMPRINT",EDGE,{"disambiguationData":[TD([[subQ2,1.0]])],"derivedFrom":subQ1}),-1.0]])]});}
            var Q140;
            {var subQ0=sQuery(id+"F0.wireOp",EDGE,"E2.3.5.1");var subQ1=sQuery(id+"F0.wireOp",EDGE,"E2.2.5.0");var subQ2=makeQuery(id+"F0.imprint","INTERSECT",VERTEX,{"derivedFrom":[subQ1,subQ0]});Q140=makeQuery(id+"F0.imprint","IMPRINT",FACE,{"disambiguationData":[TD([[makeQuery(id+"F0.imprint","IMPRINT",EDGE,{"disambiguationData":[TD([[subQ2,1.0]])],"derivedFrom":subQ1}),-1.0]])]});}
            var Q141;
            {var subQ0=sQuery(id+"F0.wireOp",EDGE,"E2.4.3.1");var subQ1=sQuery(id+"F0.wireOp",EDGE,"E2.3.3.0");var subQ2=makeQuery(id+"F0.imprint","INTERSECT",VERTEX,{"derivedFrom":[subQ1,subQ0]});Q141=makeQuery(id+"F0.imprint","IMPRINT",FACE,{"disambiguationData":[TD([[makeQuery(id+"F0.imprint","IMPRINT",EDGE,{"disambiguationData":[TD([[subQ2,1.0]])],"derivedFrom":subQ1}),-1.0]])]});}
            var Q142;
            {var subQ0=sQuery(id+"F0.wireOp",EDGE,"E2.3.3.1");var subQ1=sQuery(id+"F0.wireOp",EDGE,"E2.2.3.0");var subQ2=makeQuery(id+"F0.imprint","INTERSECT",VERTEX,{"derivedFrom":[subQ1,subQ0]});Q142=makeQuery(id+"F0.imprint","IMPRINT",FACE,{"disambiguationData":[TD([[makeQuery(id+"F0.imprint","IMPRINT",EDGE,{"disambiguationData":[TD([[subQ2,1.0]])],"derivedFrom":subQ1}),-1.0]])]});}
            var Q143;
            {var subQ0=sQuery(id+"F0.wireOp",EDGE,"E2.1.3.0");var subQ1=sQuery(id+"F0.wireOp",EDGE,"E2.0.3.0");var subQ2=makeQuery(id+"F0.imprint","INTERSECT",VERTEX,{"disambiguationData":[OD(0.0)],"derivedFrom":[subQ1,subQ0]});Q143=makeQuery(id+"F0.imprint","IMPRINT",FACE,{"disambiguationData":[TD([[makeQuery(id+"F0.imprint","IMPRINT",EDGE,{"disambiguationData":[TD([[subQ2,-1.0]])],"derivedFrom":subQ1}),-1.0]])]});}
            var Q144;
            {var subQ0=sQuery(id+"F0.wireOp",EDGE,"E2.11.2.0");var subQ1=sQuery(id+"F0.wireOp",EDGE,"E2.11.1.0");var subQ2=makeQuery(id+"F0.imprint","INTERSECT",VERTEX,{"disambiguationData":[OD(0.0)],"derivedFrom":[subQ1,subQ0]});Q144=makeQuery(id+"F0.imprint","IMPRINT",FACE,{"disambiguationData":[TD([[makeQuery(id+"F0.imprint","IMPRINT",EDGE,{"disambiguationData":[TD([[subQ2,-1.0]])],"derivedFrom":subQ1}),-1.0]])]});}
            var Q145;
            {var subQ0=sQuery(id+"F0.wireOp",EDGE,"E2.11.1.1");var subQ1=sQuery(id+"F0.wireOp",EDGE,"E2.10.1.0");var subQ2=makeQuery(id+"F0.imprint","INTERSECT",VERTEX,{"derivedFrom":[subQ1,subQ0]});Q145=makeQuery(id+"F0.imprint","IMPRINT",FACE,{"disambiguationData":[TD([[makeQuery(id+"F0.imprint","IMPRINT",EDGE,{"disambiguationData":[TD([[subQ2,1.0]])],"derivedFrom":subQ1}),-1.0]])]});}
            var Q146;
            {var subQ0=sQuery(id+"F0.wireOp",EDGE,"E2.8.5.1");var subQ1=sQuery(id+"F0.wireOp",EDGE,"E2.7.5.0");var subQ2=makeQuery(id+"F0.imprint","INTERSECT",VERTEX,{"derivedFrom":[subQ1,subQ0]});Q146=makeQuery(id+"F0.imprint","IMPRINT",FACE,{"disambiguationData":[TD([[makeQuery(id+"F0.imprint","IMPRINT",EDGE,{"disambiguationData":[TD([[subQ2,1.0]])],"derivedFrom":subQ1}),-1.0]])]});}
            var Q147;
            {var subQ0=sQuery(id+"F0.wireOp",EDGE,"E2.9.3.1");var subQ1=sQuery(id+"F0.wireOp",EDGE,"E2.8.3.0");var subQ2=makeQuery(id+"F0.imprint","INTERSECT",VERTEX,{"derivedFrom":[subQ1,subQ0]});Q147=makeQuery(id+"F0.imprint","IMPRINT",FACE,{"disambiguationData":[TD([[makeQuery(id+"F0.imprint","IMPRINT",EDGE,{"disambiguationData":[TD([[subQ2,1.0]])],"derivedFrom":subQ1}),-1.0]])]});}
            var Q148;
            {var subQ0=sQuery(id+"F0.wireOp",EDGE,"E2.7.5.1");var subQ1=sQuery(id+"F0.wireOp",EDGE,"E2.6.5.0");var subQ2=makeQuery(id+"F0.imprint","INTERSECT",VERTEX,{"derivedFrom":[subQ1,subQ0]});Q148=makeQuery(id+"F0.imprint","IMPRINT",FACE,{"disambiguationData":[TD([[makeQuery(id+"F0.imprint","IMPRINT",EDGE,{"disambiguationData":[TD([[subQ2,1.0]])],"derivedFrom":subQ1}),-1.0]])]});}
            var Q149;
            {var subQ0=sQuery(id+"F0.wireOp",EDGE,"E2.4.4.0");var subQ1=sQuery(id+"F0.wireOp",EDGE,"E2.4.3.0");var subQ2=makeQuery(id+"F0.imprint","INTERSECT",VERTEX,{"disambiguationData":[OD(0.0)],"derivedFrom":[subQ1,subQ0]});Q149=makeQuery(id+"F0.imprint","IMPRINT",FACE,{"disambiguationData":[TD([[makeQuery(id+"F0.imprint","IMPRINT",EDGE,{"disambiguationData":[TD([[subQ2,-1.0]])],"derivedFrom":subQ1}),-1.0]])]});}
            var Q150;
            {var subQ0=sQuery(id+"F0.wireOp",EDGE,"E2.1.1.0");var subQ1=sQuery(id+"F0.wireOp",EDGE,"E2.0.1.0");var subQ2=makeQuery(id+"F0.imprint","INTERSECT",VERTEX,{"disambiguationData":[OD(0.0)],"derivedFrom":[subQ1,subQ0]});Q150=makeQuery(id+"F0.imprint","IMPRINT",FACE,{"disambiguationData":[TD([[makeQuery(id+"F0.imprint","IMPRINT",EDGE,{"disambiguationData":[TD([[subQ2,1.0]])],"derivedFrom":subQ1}),1.0]])]});}
            var Q151;
            {var subQ0=sQuery(id+"F0.wireOp",EDGE,"E2.11.1.0");var subQ1=sQuery(id+"F0.wireOp",EDGE,"E2.11.0.0");var subQ2=makeQuery(id+"F0.imprint","INTERSECT",VERTEX,{"disambiguationData":[OD(0.0)],"derivedFrom":[subQ1,subQ0]});Q151=makeQuery(id+"F0.imprint","IMPRINT",FACE,{"disambiguationData":[TD([[makeQuery(id+"F0.imprint","IMPRINT",EDGE,{"disambiguationData":[TD([[subQ2,-1.0]])],"derivedFrom":subQ1}),-1.0]])]});}
            var Q152;
            {var subQ0=sQuery(id+"F0.wireOp",EDGE,"E2.9.4.0");var subQ1=sQuery(id+"F0.wireOp",EDGE,"E2.9.3.0");var subQ2=makeQuery(id+"F0.imprint","INTERSECT",VERTEX,{"disambiguationData":[OD(0.0)],"derivedFrom":[subQ1,subQ0]});Q152=makeQuery(id+"F0.imprint","IMPRINT",FACE,{"disambiguationData":[TD([[makeQuery(id+"F0.imprint","IMPRINT",EDGE,{"disambiguationData":[TD([[subQ2,-1.0]])],"derivedFrom":subQ1}),-1.0]])]});}
            var Q153;
            {var subQ0=sQuery(id+"F0.wireOp",EDGE,"E2.8.6.0");var subQ1=sQuery(id+"F0.wireOp",EDGE,"E2.8.5.0");var subQ2=makeQuery(id+"F0.imprint","INTERSECT",VERTEX,{"disambiguationData":[OD(0.0)],"derivedFrom":[subQ1,subQ0]});Q153=makeQuery(id+"F0.imprint","IMPRINT",FACE,{"disambiguationData":[TD([[makeQuery(id+"F0.imprint","IMPRINT",EDGE,{"disambiguationData":[TD([[subQ2,-1.0]])],"derivedFrom":subQ1}),1.0]])]});}
            var Q154;
            {var subQ0=sQuery(id+"F0.wireOp",EDGE,"E2.10.2.0");var subQ1=sQuery(id+"F0.wireOp",EDGE,"E2.10.1.0");var subQ2=makeQuery(id+"F0.imprint","INTERSECT",VERTEX,{"disambiguationData":[OD(0.0)],"derivedFrom":[subQ1,subQ0]});Q154=makeQuery(id+"F0.imprint","IMPRINT",FACE,{"disambiguationData":[TD([[makeQuery(id+"F0.imprint","IMPRINT",EDGE,{"disambiguationData":[TD([[subQ2,-1.0]])],"derivedFrom":subQ1}),1.0]])]});}
            var Q155;
            {var subQ0=sQuery(id+"F0.wireOp",EDGE,"E2.2.4.0");var subQ1=sQuery(id+"F0.wireOp",EDGE,"E2.2.3.0");var subQ2=makeQuery(id+"F0.imprint","INTERSECT",VERTEX,{"disambiguationData":[OD(0.0)],"derivedFrom":[subQ1,subQ0]});Q155=makeQuery(id+"F0.imprint","IMPRINT",FACE,{"disambiguationData":[TD([[makeQuery(id+"F0.imprint","IMPRINT",EDGE,{"disambiguationData":[TD([[subQ2,-1.0]])],"derivedFrom":subQ1}),1.0]])]});}
            var Q156;
            {var subQ0=sQuery(id+"F0.wireOp",EDGE,"E2.1.3.0");var subQ1=sQuery(id+"F0.wireOp",EDGE,"E2.0.3.0");var subQ2=makeQuery(id+"F0.imprint","INTERSECT",VERTEX,{"disambiguationData":[OD(0.0)],"derivedFrom":[subQ1,subQ0]});Q156=makeQuery(id+"F0.imprint","IMPRINT",FACE,{"disambiguationData":[TD([[makeQuery(id+"F0.imprint","IMPRINT",EDGE,{"disambiguationData":[TD([[subQ2,1.0]])],"derivedFrom":subQ1}),-1.0]])]});}
            var Q157;
            {var subQ0=sQuery(id+"F0.wireOp",EDGE,"E2.9.4.0");var subQ1=sQuery(id+"F0.wireOp",EDGE,"E2.9.3.0");var subQ2=makeQuery(id+"F0.imprint","INTERSECT",VERTEX,{"disambiguationData":[OD(0.0)],"derivedFrom":[subQ1,subQ0]});Q157=makeQuery(id+"F0.imprint","IMPRINT",FACE,{"disambiguationData":[TD([[makeQuery(id+"F0.imprint","IMPRINT",EDGE,{"disambiguationData":[TD([[subQ2,-1.0]])],"derivedFrom":subQ1}),1.0]])]});}
            var Q158;
            {var subQ0=sQuery(id+"F0.wireOp",EDGE,"E2.9.6.0");var subQ1=sQuery(id+"F0.wireOp",EDGE,"E2.9.5.0");var subQ2=makeQuery(id+"F0.imprint","INTERSECT",VERTEX,{"disambiguationData":[OD(0.0)],"derivedFrom":[subQ1,subQ0]});Q158=makeQuery(id+"F0.imprint","IMPRINT",FACE,{"disambiguationData":[TD([[makeQuery(id+"F0.imprint","IMPRINT",EDGE,{"disambiguationData":[TD([[subQ2,-1.0]])],"derivedFrom":subQ1}),1.0]])]});}
            var Q159;
            {var subQ0=sQuery(id+"F0.wireOp",EDGE,"E2.7.4.0");var subQ1=sQuery(id+"F0.wireOp",EDGE,"E2.7.3.0");var subQ2=makeQuery(id+"F0.imprint","INTERSECT",VERTEX,{"disambiguationData":[OD(0.0)],"derivedFrom":[subQ1,subQ0]});Q159=makeQuery(id+"F0.imprint","IMPRINT",FACE,{"disambiguationData":[TD([[makeQuery(id+"F0.imprint","IMPRINT",EDGE,{"disambiguationData":[TD([[subQ2,-1.0]])],"derivedFrom":subQ1}),1.0]])]});}
            var Q160;
            {var subQ0=sQuery(id+"F0.wireOp",EDGE,"E2.7.6.0");var subQ1=sQuery(id+"F0.wireOp",EDGE,"E2.7.5.0");var subQ2=makeQuery(id+"F0.imprint","INTERSECT",VERTEX,{"disambiguationData":[OD(0.0)],"derivedFrom":[subQ1,subQ0]});Q160=makeQuery(id+"F0.imprint","IMPRINT",FACE,{"disambiguationData":[TD([[makeQuery(id+"F0.imprint","IMPRINT",EDGE,{"disambiguationData":[TD([[subQ2,-1.0]])],"derivedFrom":subQ1}),1.0]])]});}
            var Q161;
            {var subQ0=sQuery(id+"F0.wireOp",EDGE,"E2.8.4.0");var subQ1=sQuery(id+"F0.wireOp",EDGE,"E2.8.3.0");var subQ2=makeQuery(id+"F0.imprint","INTERSECT",VERTEX,{"disambiguationData":[OD(0.0)],"derivedFrom":[subQ1,subQ0]});Q161=makeQuery(id+"F0.imprint","IMPRINT",FACE,{"disambiguationData":[TD([[makeQuery(id+"F0.imprint","IMPRINT",EDGE,{"disambiguationData":[TD([[subQ2,-1.0]])],"derivedFrom":subQ1}),1.0]])]});}
            var Q162;
            {var subQ0=sQuery(id+"F0.wireOp",EDGE,"E2.5.4.0");var subQ1=sQuery(id+"F0.wireOp",EDGE,"E2.5.3.0");var subQ2=makeQuery(id+"F0.imprint","INTERSECT",VERTEX,{"disambiguationData":[OD(0.0)],"derivedFrom":[subQ1,subQ0]});Q162=makeQuery(id+"F0.imprint","IMPRINT",FACE,{"disambiguationData":[TD([[makeQuery(id+"F0.imprint","IMPRINT",EDGE,{"disambiguationData":[TD([[subQ2,-1.0]])],"derivedFrom":subQ1}),1.0]])]});}
            var Q163;
            {var subQ0=sQuery(id+"F0.wireOp",EDGE,"E2.5.6.0");var subQ1=sQuery(id+"F0.wireOp",EDGE,"E2.5.5.0");var subQ2=makeQuery(id+"F0.imprint","INTERSECT",VERTEX,{"disambiguationData":[OD(0.0)],"derivedFrom":[subQ1,subQ0]});Q163=makeQuery(id+"F0.imprint","IMPRINT",FACE,{"disambiguationData":[TD([[makeQuery(id+"F0.imprint","IMPRINT",EDGE,{"disambiguationData":[TD([[subQ2,-1.0]])],"derivedFrom":subQ1}),1.0]])]});}
            var Q164;
            {var subQ0=sQuery(id+"F0.wireOp",EDGE,"E2.6.2.0");var subQ1=sQuery(id+"F0.wireOp",EDGE,"E2.6.1.0");var subQ2=makeQuery(id+"F0.imprint","INTERSECT",VERTEX,{"disambiguationData":[OD(0.0)],"derivedFrom":[subQ1,subQ0]});Q164=makeQuery(id+"F0.imprint","IMPRINT",FACE,{"disambiguationData":[TD([[makeQuery(id+"F0.imprint","IMPRINT",EDGE,{"disambiguationData":[TD([[subQ2,-1.0]])],"derivedFrom":subQ1}),1.0]])]});}
            var Q165;
            {var subQ0=sQuery(id+"F0.wireOp",EDGE,"E2.6.4.0");var subQ1=sQuery(id+"F0.wireOp",EDGE,"E2.6.3.0");var subQ2=makeQuery(id+"F0.imprint","INTERSECT",VERTEX,{"disambiguationData":[OD(0.0)],"derivedFrom":[subQ1,subQ0]});Q165=makeQuery(id+"F0.imprint","IMPRINT",FACE,{"disambiguationData":[TD([[makeQuery(id+"F0.imprint","IMPRINT",EDGE,{"disambiguationData":[TD([[subQ2,-1.0]])],"derivedFrom":subQ1}),1.0]])]});}
            var Q166;
            {var subQ0=sQuery(id+"F0.wireOp",EDGE,"E2.4.4.0");var subQ1=sQuery(id+"F0.wireOp",EDGE,"E2.4.3.0");var subQ2=makeQuery(id+"F0.imprint","INTERSECT",VERTEX,{"disambiguationData":[OD(0.0)],"derivedFrom":[subQ1,subQ0]});Q166=makeQuery(id+"F0.imprint","IMPRINT",FACE,{"disambiguationData":[TD([[makeQuery(id+"F0.imprint","IMPRINT",EDGE,{"disambiguationData":[TD([[subQ2,-1.0]])],"derivedFrom":subQ1}),1.0]])]});}
            var Q167;
            {var subQ0=sQuery(id+"F0.wireOp",EDGE,"E2.4.6.0");var subQ1=sQuery(id+"F0.wireOp",EDGE,"E2.4.5.0");var subQ2=makeQuery(id+"F0.imprint","INTERSECT",VERTEX,{"disambiguationData":[OD(0.0)],"derivedFrom":[subQ1,subQ0]});Q167=makeQuery(id+"F0.imprint","IMPRINT",FACE,{"disambiguationData":[TD([[makeQuery(id+"F0.imprint","IMPRINT",EDGE,{"disambiguationData":[TD([[subQ2,-1.0]])],"derivedFrom":subQ1}),1.0]])]});}
            var Q168;
            {var subQ0=sQuery(id+"F0.wireOp",EDGE,"E2.5.2.0");var subQ1=sQuery(id+"F0.wireOp",EDGE,"E2.5.1.0");var subQ2=makeQuery(id+"F0.imprint","INTERSECT",VERTEX,{"disambiguationData":[OD(0.0)],"derivedFrom":[subQ1,subQ0]});Q168=makeQuery(id+"F0.imprint","IMPRINT",FACE,{"disambiguationData":[TD([[makeQuery(id+"F0.imprint","IMPRINT",EDGE,{"disambiguationData":[TD([[subQ2,-1.0]])],"derivedFrom":subQ1}),1.0]])]});}
            var Q169;
            {var subQ0=sQuery(id+"F0.wireOp",EDGE,"E2.0.1.0");var subQ1=sQuery(id+"F0.wireOp",EDGE,"E1.0");var subQ2=makeQuery(id+"F0.imprint","INTERSECT",VERTEX,{"disambiguationData":[OD(1.0)],"derivedFrom":[subQ1,subQ0]});Q169=makeQuery(id+"F0.imprint","IMPRINT",FACE,{"disambiguationData":[TD([[makeQuery(id+"F0.imprint","IMPRINT",EDGE,{"disambiguationData":[TD([[subQ2,-1.0]])],"derivedFrom":subQ1}),1.0]])]});}
            var Q170;
            {var subQ0=sQuery(id+"F0.wireOp",EDGE,"E2.1.5.0");var subQ1=sQuery(id+"F0.wireOp",EDGE,"E2.0.5.0");var subQ2=makeQuery(id+"F0.imprint","INTERSECT",VERTEX,{"disambiguationData":[OD(0.0)],"derivedFrom":[subQ1,subQ0]});Q170=makeQuery(id+"F0.imprint","IMPRINT",FACE,{"disambiguationData":[TD([[makeQuery(id+"F0.imprint","IMPRINT",EDGE,{"disambiguationData":[TD([[subQ2,-1.0]])],"derivedFrom":subQ1}),1.0]])]});}
            var Q171;
            {var subQ0=sQuery(id+"F0.wireOp",EDGE,"E2.3.6.0");var subQ1=sQuery(id+"F0.wireOp",EDGE,"E2.2.6.0");var subQ2=makeQuery(id+"F0.imprint","INTERSECT",VERTEX,{"disambiguationData":[OD(0.0)],"derivedFrom":[subQ1,subQ0]});Q171=makeQuery(id+"F0.imprint","IMPRINT",FACE,{"disambiguationData":[TD([[makeQuery(id+"F0.imprint","IMPRINT",EDGE,{"disambiguationData":[TD([[subQ2,1.0]])],"derivedFrom":subQ1}),-1.0]])]});}
            var Q172;
            {var subQ0=sQuery(id+"F0.wireOp",EDGE,"E2.11.3.0");var subQ1=sQuery(id+"F0.wireOp",EDGE,"E2.10.3.0");var subQ2=makeQuery(id+"F0.imprint","INTERSECT",VERTEX,{"disambiguationData":[OD(0.0)],"derivedFrom":[subQ1,subQ0]});Q172=makeQuery(id+"F0.imprint","IMPRINT",FACE,{"disambiguationData":[TD([[makeQuery(id+"F0.imprint","IMPRINT",EDGE,{"disambiguationData":[TD([[subQ2,-1.0]])],"derivedFrom":subQ1}),1.0]])]});}
            var Q173;
            {var subQ0=sQuery(id+"F0.wireOp",EDGE,"E2.11.5.0");var subQ1=sQuery(id+"F0.wireOp",EDGE,"E2.10.5.0");var subQ2=makeQuery(id+"F0.imprint","INTERSECT",VERTEX,{"disambiguationData":[OD(0.0)],"derivedFrom":[subQ1,subQ0]});Q173=makeQuery(id+"F0.imprint","IMPRINT",FACE,{"disambiguationData":[TD([[makeQuery(id+"F0.imprint","IMPRINT",EDGE,{"disambiguationData":[TD([[subQ2,-1.0]])],"derivedFrom":subQ1}),1.0]])]});}
            var Q174;
            {var subQ0=sQuery(id+"F0.wireOp",EDGE,"E2.1.2.1");var subQ1=sQuery(id+"F0.wireOp",EDGE,"E2.0.2.0");var subQ2=makeQuery(id+"F0.imprint","INTERSECT",VERTEX,{"derivedFrom":[subQ1,subQ0]});Q174=makeQuery(id+"F0.imprint","IMPRINT",FACE,{"disambiguationData":[TD([[makeQuery(id+"F0.imprint","IMPRINT",EDGE,{"disambiguationData":[TD([[subQ2,1.0]])],"derivedFrom":subQ1}),-1.0]])]});}
            var Q175;
            {var subQ0=sQuery(id+"F0.wireOp",EDGE,"E2.1.5.0");var subQ1=sQuery(id+"F0.wireOp",EDGE,"E2.0.5.0");var subQ2=makeQuery(id+"F0.imprint","INTERSECT",VERTEX,{"disambiguationData":[OD(0.0)],"derivedFrom":[subQ1,subQ0]});Q175=makeQuery(id+"F0.imprint","IMPRINT",FACE,{"disambiguationData":[TD([[makeQuery(id+"F0.imprint","IMPRINT",EDGE,{"disambiguationData":[TD([[subQ2,1.0]])],"derivedFrom":subQ1}),-1.0]])]});}
            var Q176;
            {var subQ0=sQuery(id+"F0.wireOp",EDGE,"E2.2.1.0");var subQ1=sQuery(id+"F0.wireOp",EDGE,"E2.1.1.0");var subQ2=makeQuery(id+"F0.imprint","INTERSECT",VERTEX,{"disambiguationData":[OD(0.0)],"derivedFrom":[subQ1,subQ0]});Q176=makeQuery(id+"F0.imprint","IMPRINT",FACE,{"disambiguationData":[TD([[makeQuery(id+"F0.imprint","IMPRINT",EDGE,{"disambiguationData":[TD([[subQ2,-1.0]])],"derivedFrom":subQ1}),1.0]])]});}
            var Q177;
            {var subQ0=sQuery(id+"F0.wireOp",EDGE,"E2.9.5.0");var subQ1=sQuery(id+"F0.wireOp",EDGE,"E2.8.5.0");var subQ2=makeQuery(id+"F0.imprint","INTERSECT",VERTEX,{"disambiguationData":[OD(0.0)],"derivedFrom":[subQ1,subQ0]});Q177=makeQuery(id+"F0.imprint","IMPRINT",FACE,{"disambiguationData":[TD([[makeQuery(id+"F0.imprint","IMPRINT",EDGE,{"disambiguationData":[TD([[subQ2,-1.0]])],"derivedFrom":subQ1}),1.0]])]});}
            var Q178;
            {var subQ0=sQuery(id+"F0.wireOp",EDGE,"E2.10.1.0");var subQ1=sQuery(id+"F0.wireOp",EDGE,"E2.9.1.0");var subQ2=makeQuery(id+"F0.imprint","INTERSECT",VERTEX,{"disambiguationData":[OD(0.0)],"derivedFrom":[subQ1,subQ0]});Q178=makeQuery(id+"F0.imprint","IMPRINT",FACE,{"disambiguationData":[TD([[makeQuery(id+"F0.imprint","IMPRINT",EDGE,{"disambiguationData":[TD([[subQ2,-1.0]])],"derivedFrom":subQ1}),1.0]])]});}
            var Q179;
            {var subQ0=sQuery(id+"F0.wireOp",EDGE,"E2.10.5.0");var subQ1=sQuery(id+"F0.wireOp",EDGE,"E2.9.5.0");var subQ2=makeQuery(id+"F0.imprint","INTERSECT",VERTEX,{"disambiguationData":[OD(0.0)],"derivedFrom":[subQ1,subQ0]});Q179=makeQuery(id+"F0.imprint","IMPRINT",FACE,{"disambiguationData":[TD([[makeQuery(id+"F0.imprint","IMPRINT",EDGE,{"disambiguationData":[TD([[subQ2,-1.0]])],"derivedFrom":subQ1}),1.0]])]});}
            var Q180;
            {var subQ0=sQuery(id+"F0.wireOp",EDGE,"E2.8.3.0");var subQ1=sQuery(id+"F0.wireOp",EDGE,"E2.7.3.0");var subQ2=makeQuery(id+"F0.imprint","INTERSECT",VERTEX,{"disambiguationData":[OD(0.0)],"derivedFrom":[subQ1,subQ0]});Q180=makeQuery(id+"F0.imprint","IMPRINT",FACE,{"disambiguationData":[TD([[makeQuery(id+"F0.imprint","IMPRINT",EDGE,{"disambiguationData":[TD([[subQ2,-1.0]])],"derivedFrom":subQ1}),1.0]])]});}
            var Q181;
            {var subQ0=sQuery(id+"F0.wireOp",EDGE,"E2.9.1.0");var subQ1=sQuery(id+"F0.wireOp",EDGE,"E2.8.1.0");var subQ2=makeQuery(id+"F0.imprint","INTERSECT",VERTEX,{"disambiguationData":[OD(0.0)],"derivedFrom":[subQ1,subQ0]});Q181=makeQuery(id+"F0.imprint","IMPRINT",FACE,{"disambiguationData":[TD([[makeQuery(id+"F0.imprint","IMPRINT",EDGE,{"disambiguationData":[TD([[subQ2,-1.0]])],"derivedFrom":subQ1}),1.0]])]});}
            var Q182;
            {var subQ0=sQuery(id+"F0.wireOp",EDGE,"E2.0.4.0");var subQ1=sQuery(id+"F0.wireOp",EDGE,"E2.0.3.0");var subQ2=makeQuery(id+"F0.imprint","INTERSECT",VERTEX,{"disambiguationData":[OD(0.0)],"derivedFrom":[subQ1,subQ0]});Q182=makeQuery(id+"F0.imprint","IMPRINT",FACE,{"disambiguationData":[TD([[makeQuery(id+"F0.imprint","IMPRINT",EDGE,{"disambiguationData":[TD([[subQ2,1.0]])],"derivedFrom":subQ1}),-1.0]])]});}
            var Q183;
            {var subQ0=sQuery(id+"F0.wireOp",EDGE,"E2.7.5.0");var subQ1=sQuery(id+"F0.wireOp",EDGE,"E2.6.5.0");var subQ2=makeQuery(id+"F0.imprint","INTERSECT",VERTEX,{"disambiguationData":[OD(0.0)],"derivedFrom":[subQ1,subQ0]});Q183=makeQuery(id+"F0.imprint","IMPRINT",FACE,{"disambiguationData":[TD([[makeQuery(id+"F0.imprint","IMPRINT",EDGE,{"disambiguationData":[TD([[subQ2,-1.0]])],"derivedFrom":subQ1}),1.0]])]});}
            var Q184;
            {var subQ0=sQuery(id+"F0.wireOp",EDGE,"E2.8.1.0");var subQ1=sQuery(id+"F0.wireOp",EDGE,"E2.7.1.0");var subQ2=makeQuery(id+"F0.imprint","INTERSECT",VERTEX,{"disambiguationData":[OD(0.0)],"derivedFrom":[subQ1,subQ0]});Q184=makeQuery(id+"F0.imprint","IMPRINT",FACE,{"disambiguationData":[TD([[makeQuery(id+"F0.imprint","IMPRINT",EDGE,{"disambiguationData":[TD([[subQ2,-1.0]])],"derivedFrom":subQ1}),1.0]])]});}
            var Q185;
            {var subQ0=sQuery(id+"F0.wireOp",EDGE,"E2.0.3.0");var subQ1=sQuery(id+"F0.wireOp",EDGE,"E2.0.2.0");var subQ2=makeQuery(id+"F0.imprint","INTERSECT",VERTEX,{"disambiguationData":[OD(0.0)],"derivedFrom":[subQ1,subQ0]});Q185=makeQuery(id+"F0.imprint","IMPRINT",FACE,{"disambiguationData":[TD([[makeQuery(id+"F0.imprint","IMPRINT",EDGE,{"disambiguationData":[TD([[subQ2,1.0]])],"derivedFrom":subQ1}),-1.0]])]});}
            var Q186;
            {var subQ0=sQuery(id+"F0.wireOp",EDGE,"E2.6.3.0");var subQ1=sQuery(id+"F0.wireOp",EDGE,"E2.5.3.0");var subQ2=makeQuery(id+"F0.imprint","INTERSECT",VERTEX,{"disambiguationData":[OD(0.0)],"derivedFrom":[subQ1,subQ0]});Q186=makeQuery(id+"F0.imprint","IMPRINT",FACE,{"disambiguationData":[TD([[makeQuery(id+"F0.imprint","IMPRINT",EDGE,{"disambiguationData":[TD([[subQ2,-1.0]])],"derivedFrom":subQ1}),1.0]])]});}
            var Q187;
            {var subQ0=sQuery(id+"F0.wireOp",EDGE,"E2.6.5.0");var subQ1=sQuery(id+"F0.wireOp",EDGE,"E2.5.5.0");var subQ2=makeQuery(id+"F0.imprint","INTERSECT",VERTEX,{"disambiguationData":[OD(0.0)],"derivedFrom":[subQ1,subQ0]});Q187=makeQuery(id+"F0.imprint","IMPRINT",FACE,{"disambiguationData":[TD([[makeQuery(id+"F0.imprint","IMPRINT",EDGE,{"disambiguationData":[TD([[subQ2,-1.0]])],"derivedFrom":subQ1}),1.0]])]});}
            var Q188;
            {var subQ0=sQuery(id+"F0.wireOp",EDGE,"E2.7.1.0");var subQ1=sQuery(id+"F0.wireOp",EDGE,"E2.6.1.0");var subQ2=makeQuery(id+"F0.imprint","INTERSECT",VERTEX,{"disambiguationData":[OD(0.0)],"derivedFrom":[subQ1,subQ0]});Q188=makeQuery(id+"F0.imprint","IMPRINT",FACE,{"disambiguationData":[TD([[makeQuery(id+"F0.imprint","IMPRINT",EDGE,{"disambiguationData":[TD([[subQ2,-1.0]])],"derivedFrom":subQ1}),1.0]])]});}
            var Q189;
            {var subQ0=sQuery(id+"F0.wireOp",EDGE,"E2.7.3.0");var subQ1=sQuery(id+"F0.wireOp",EDGE,"E2.6.3.0");var subQ2=makeQuery(id+"F0.imprint","INTERSECT",VERTEX,{"disambiguationData":[OD(0.0)],"derivedFrom":[subQ1,subQ0]});Q189=makeQuery(id+"F0.imprint","IMPRINT",FACE,{"disambiguationData":[TD([[makeQuery(id+"F0.imprint","IMPRINT",EDGE,{"disambiguationData":[TD([[subQ2,-1.0]])],"derivedFrom":subQ1}),1.0]])]});}
            var Q190;
            {var subQ0=sQuery(id+"F0.wireOp",EDGE,"E2.5.1.0");var subQ1=sQuery(id+"F0.wireOp",EDGE,"E2.4.1.0");var subQ2=makeQuery(id+"F0.imprint","INTERSECT",VERTEX,{"disambiguationData":[OD(0.0)],"derivedFrom":[subQ1,subQ0]});Q190=makeQuery(id+"F0.imprint","IMPRINT",FACE,{"disambiguationData":[TD([[makeQuery(id+"F0.imprint","IMPRINT",EDGE,{"disambiguationData":[TD([[subQ2,-1.0]])],"derivedFrom":subQ1}),1.0]])]});}
            var Q191;
            {var subQ0=sQuery(id+"F0.wireOp",EDGE,"E2.5.5.0");var subQ1=sQuery(id+"F0.wireOp",EDGE,"E2.4.5.0");var subQ2=makeQuery(id+"F0.imprint","INTERSECT",VERTEX,{"disambiguationData":[OD(0.0)],"derivedFrom":[subQ1,subQ0]});Q191=makeQuery(id+"F0.imprint","IMPRINT",FACE,{"disambiguationData":[TD([[makeQuery(id+"F0.imprint","IMPRINT",EDGE,{"disambiguationData":[TD([[subQ2,-1.0]])],"derivedFrom":subQ1}),1.0]])]});}
            var Q192;
            {var subQ0=sQuery(id+"F0.wireOp",EDGE,"E2.4.1.0");var subQ1=sQuery(id+"F0.wireOp",EDGE,"E2.3.1.0");var subQ2=makeQuery(id+"F0.imprint","INTERSECT",VERTEX,{"disambiguationData":[OD(0.0)],"derivedFrom":[subQ1,subQ0]});Q192=makeQuery(id+"F0.imprint","IMPRINT",FACE,{"disambiguationData":[TD([[makeQuery(id+"F0.imprint","IMPRINT",EDGE,{"disambiguationData":[TD([[subQ2,-1.0]])],"derivedFrom":subQ1}),1.0]])]});}
            var Q193;
            {var subQ0=sQuery(id+"F0.wireOp",EDGE,"E2.4.5.0");var subQ1=sQuery(id+"F0.wireOp",EDGE,"E2.3.5.0");var subQ2=makeQuery(id+"F0.imprint","INTERSECT",VERTEX,{"disambiguationData":[OD(0.0)],"derivedFrom":[subQ1,subQ0]});Q193=makeQuery(id+"F0.imprint","IMPRINT",FACE,{"disambiguationData":[TD([[makeQuery(id+"F0.imprint","IMPRINT",EDGE,{"disambiguationData":[TD([[subQ2,-1.0]])],"derivedFrom":subQ1}),1.0]])]});}
            var Q194;
            {var subQ0=sQuery(id+"F0.wireOp",EDGE,"E2.2.3.0");var subQ1=sQuery(id+"F0.wireOp",EDGE,"E2.1.3.0");var subQ2=makeQuery(id+"F0.imprint","INTERSECT",VERTEX,{"disambiguationData":[OD(0.0)],"derivedFrom":[subQ1,subQ0]});Q194=makeQuery(id+"F0.imprint","IMPRINT",FACE,{"disambiguationData":[TD([[makeQuery(id+"F0.imprint","IMPRINT",EDGE,{"disambiguationData":[TD([[subQ2,-1.0]])],"derivedFrom":subQ1}),1.0]])]});}
            var Q195;
            {var subQ0=sQuery(id+"F0.wireOp",EDGE,"E2.2.5.0");var subQ1=sQuery(id+"F0.wireOp",EDGE,"E2.1.5.0");var subQ2=makeQuery(id+"F0.imprint","INTERSECT",VERTEX,{"disambiguationData":[OD(0.0)],"derivedFrom":[subQ1,subQ0]});Q195=makeQuery(id+"F0.imprint","IMPRINT",FACE,{"disambiguationData":[TD([[makeQuery(id+"F0.imprint","IMPRINT",EDGE,{"disambiguationData":[TD([[subQ2,-1.0]])],"derivedFrom":subQ1}),1.0]])]});}
            var Q196;
            {var subQ0=sQuery(id+"F0.wireOp",EDGE,"E2.3.1.0");var subQ1=sQuery(id+"F0.wireOp",EDGE,"E2.2.1.0");var subQ2=makeQuery(id+"F0.imprint","INTERSECT",VERTEX,{"disambiguationData":[OD(0.0)],"derivedFrom":[subQ1,subQ0]});Q196=makeQuery(id+"F0.imprint","IMPRINT",FACE,{"disambiguationData":[TD([[makeQuery(id+"F0.imprint","IMPRINT",EDGE,{"disambiguationData":[TD([[subQ2,-1.0]])],"derivedFrom":subQ1}),1.0]])]});}
            var Q197;
            {var subQ0=sQuery(id+"F0.wireOp",EDGE,"E2.3.3.0");var subQ1=sQuery(id+"F0.wireOp",EDGE,"E2.2.3.0");var subQ2=makeQuery(id+"F0.imprint","INTERSECT",VERTEX,{"disambiguationData":[OD(0.0)],"derivedFrom":[subQ1,subQ0]});Q197=makeQuery(id+"F0.imprint","IMPRINT",FACE,{"disambiguationData":[TD([[makeQuery(id+"F0.imprint","IMPRINT",EDGE,{"disambiguationData":[TD([[subQ2,-1.0]])],"derivedFrom":subQ1}),1.0]])]});}
            var Q198;
            {var subQ0=sQuery(id+"F0.wireOp",EDGE,"E2.11.3.0");var subQ1=sQuery(id+"F0.wireOp",EDGE,"E2.10.3.0");var subQ2=makeQuery(id+"F0.imprint","INTERSECT",VERTEX,{"disambiguationData":[OD(0.0)],"derivedFrom":[subQ1,subQ0]});Q198=makeQuery(id+"F0.imprint","IMPRINT",FACE,{"disambiguationData":[TD([[makeQuery(id+"F0.imprint","IMPRINT",EDGE,{"disambiguationData":[TD([[subQ2,1.0]])],"derivedFrom":subQ1}),-1.0]])]});}
            var Q199;
            {var subQ0=sQuery(id+"F0.wireOp",EDGE,"E2.11.5.0");var subQ1=sQuery(id+"F0.wireOp",EDGE,"E2.10.5.0");var subQ2=makeQuery(id+"F0.imprint","INTERSECT",VERTEX,{"disambiguationData":[OD(0.0)],"derivedFrom":[subQ1,subQ0]});Q199=makeQuery(id+"F0.imprint","IMPRINT",FACE,{"disambiguationData":[TD([[makeQuery(id+"F0.imprint","IMPRINT",EDGE,{"disambiguationData":[TD([[subQ2,1.0]])],"derivedFrom":subQ1}),-1.0]])]});}
            var Q200;
            {var subQ0=sQuery(id+"F0.wireOp",EDGE,"E2.10.1.0");var subQ1=sQuery(id+"F0.wireOp",EDGE,"E2.9.1.0");var subQ2=makeQuery(id+"F0.imprint","INTERSECT",VERTEX,{"disambiguationData":[OD(0.0)],"derivedFrom":[subQ1,subQ0]});Q200=makeQuery(id+"F0.imprint","IMPRINT",FACE,{"disambiguationData":[TD([[makeQuery(id+"F0.imprint","IMPRINT",EDGE,{"disambiguationData":[TD([[subQ2,1.0]])],"derivedFrom":subQ1}),-1.0]])]});}
            var Q201;
            {var subQ0=sQuery(id+"F0.wireOp",EDGE,"E2.10.3.0");var subQ1=sQuery(id+"F0.wireOp",EDGE,"E2.9.3.0");var subQ2=makeQuery(id+"F0.imprint","INTERSECT",VERTEX,{"disambiguationData":[OD(0.0)],"derivedFrom":[subQ1,subQ0]});Q201=makeQuery(id+"F0.imprint","IMPRINT",FACE,{"disambiguationData":[TD([[makeQuery(id+"F0.imprint","IMPRINT",EDGE,{"disambiguationData":[TD([[subQ2,1.0]])],"derivedFrom":subQ1}),-1.0]])]});}
            var Q202;
            {var subQ0=sQuery(id+"F0.wireOp",EDGE,"E2.10.5.0");var subQ1=sQuery(id+"F0.wireOp",EDGE,"E2.9.5.0");var subQ2=makeQuery(id+"F0.imprint","INTERSECT",VERTEX,{"disambiguationData":[OD(0.0)],"derivedFrom":[subQ1,subQ0]});Q202=makeQuery(id+"F0.imprint","IMPRINT",FACE,{"disambiguationData":[TD([[makeQuery(id+"F0.imprint","IMPRINT",EDGE,{"disambiguationData":[TD([[subQ2,1.0]])],"derivedFrom":subQ1}),-1.0]])]});}
            var Q203;
            {var subQ0=sQuery(id+"F0.wireOp",EDGE,"E2.3.0.0");var subQ1=sQuery(id+"F0.wireOp",EDGE,"E2.2.0.0");var subQ2=makeQuery(id+"F0.imprint","INTERSECT",VERTEX,{"disambiguationData":[OD(0.0)],"derivedFrom":[subQ1,subQ0]});Q203=makeQuery(id+"F0.imprint","IMPRINT",FACE,{"disambiguationData":[TD([[makeQuery(id+"F0.imprint","IMPRINT",EDGE,{"disambiguationData":[TD([[subQ2,-1.0]])],"derivedFrom":subQ1}),-1.0]])]});}
            var Q204;
            {var subQ0=sQuery(id+"F0.wireOp",EDGE,"E2.7.0.0");var subQ1=sQuery(id+"F0.wireOp",EDGE,"E2.6.0.0");var subQ2=makeQuery(id+"F0.imprint","INTERSECT",VERTEX,{"disambiguationData":[OD(0.0)],"derivedFrom":[subQ1,subQ0]});Q204=makeQuery(id+"F0.imprint","IMPRINT",FACE,{"disambiguationData":[TD([[makeQuery(id+"F0.imprint","IMPRINT",EDGE,{"disambiguationData":[TD([[subQ2,-1.0]])],"derivedFrom":subQ1}),-1.0]])]});}
            var Q205;
            {var subQ0=sQuery(id+"F0.wireOp",EDGE,"E2.9.1.0");var subQ1=sQuery(id+"F0.wireOp",EDGE,"E2.8.1.0");var subQ2=makeQuery(id+"F0.imprint","INTERSECT",VERTEX,{"disambiguationData":[OD(0.0)],"derivedFrom":[subQ1,subQ0]});Q205=makeQuery(id+"F0.imprint","IMPRINT",FACE,{"disambiguationData":[TD([[makeQuery(id+"F0.imprint","IMPRINT",EDGE,{"disambiguationData":[TD([[subQ2,1.0]])],"derivedFrom":subQ1}),-1.0]])]});}
            var Q206;
            {var subQ0=sQuery(id+"F0.wireOp",EDGE,"E2.9.3.0");var subQ1=sQuery(id+"F0.wireOp",EDGE,"E2.8.3.0");var subQ2=makeQuery(id+"F0.imprint","INTERSECT",VERTEX,{"disambiguationData":[OD(0.0)],"derivedFrom":[subQ1,subQ0]});Q206=makeQuery(id+"F0.imprint","IMPRINT",FACE,{"disambiguationData":[TD([[makeQuery(id+"F0.imprint","IMPRINT",EDGE,{"disambiguationData":[TD([[subQ2,1.0]])],"derivedFrom":subQ1}),-1.0]])]});}
            var Q207;
            {var subQ0=sQuery(id+"F0.wireOp",EDGE,"E2.7.5.0");var subQ1=sQuery(id+"F0.wireOp",EDGE,"E2.6.5.0");var subQ2=makeQuery(id+"F0.imprint","INTERSECT",VERTEX,{"disambiguationData":[OD(0.0)],"derivedFrom":[subQ1,subQ0]});Q207=makeQuery(id+"F0.imprint","IMPRINT",FACE,{"disambiguationData":[TD([[makeQuery(id+"F0.imprint","IMPRINT",EDGE,{"disambiguationData":[TD([[subQ2,1.0]])],"derivedFrom":subQ1}),-1.0]])]});}
            var Q208;
            {var subQ0=sQuery(id+"F0.wireOp",EDGE,"E2.8.1.0");var subQ1=sQuery(id+"F0.wireOp",EDGE,"E2.7.1.0");var subQ2=makeQuery(id+"F0.imprint","INTERSECT",VERTEX,{"disambiguationData":[OD(0.0)],"derivedFrom":[subQ1,subQ0]});Q208=makeQuery(id+"F0.imprint","IMPRINT",FACE,{"disambiguationData":[TD([[makeQuery(id+"F0.imprint","IMPRINT",EDGE,{"disambiguationData":[TD([[subQ2,1.0]])],"derivedFrom":subQ1}),-1.0]])]});}
            var Q209;
            {var subQ0=sQuery(id+"F0.wireOp",EDGE,"E2.6.3.0");var subQ1=sQuery(id+"F0.wireOp",EDGE,"E2.5.3.0");var subQ2=makeQuery(id+"F0.imprint","INTERSECT",VERTEX,{"disambiguationData":[OD(0.0)],"derivedFrom":[subQ1,subQ0]});Q209=makeQuery(id+"F0.imprint","IMPRINT",FACE,{"disambiguationData":[TD([[makeQuery(id+"F0.imprint","IMPRINT",EDGE,{"disambiguationData":[TD([[subQ2,1.0]])],"derivedFrom":subQ1}),-1.0]])]});}
            var Q210;
            {var subQ0=sQuery(id+"F0.wireOp",EDGE,"E2.6.5.0");var subQ1=sQuery(id+"F0.wireOp",EDGE,"E2.5.5.0");var subQ2=makeQuery(id+"F0.imprint","INTERSECT",VERTEX,{"disambiguationData":[OD(0.0)],"derivedFrom":[subQ1,subQ0]});Q210=makeQuery(id+"F0.imprint","IMPRINT",FACE,{"disambiguationData":[TD([[makeQuery(id+"F0.imprint","IMPRINT",EDGE,{"disambiguationData":[TD([[subQ2,1.0]])],"derivedFrom":subQ1}),-1.0]])]});}
            var Q211;
            {var subQ0=sQuery(id+"F0.wireOp",EDGE,"E2.7.1.0");var subQ1=sQuery(id+"F0.wireOp",EDGE,"E2.6.1.0");var subQ2=makeQuery(id+"F0.imprint","INTERSECT",VERTEX,{"disambiguationData":[OD(0.0)],"derivedFrom":[subQ1,subQ0]});Q211=makeQuery(id+"F0.imprint","IMPRINT",FACE,{"disambiguationData":[TD([[makeQuery(id+"F0.imprint","IMPRINT",EDGE,{"disambiguationData":[TD([[subQ2,1.0]])],"derivedFrom":subQ1}),-1.0]])]});}
            var Q212;
            {var subQ0=sQuery(id+"F0.wireOp",EDGE,"E2.5.1.0");var subQ1=sQuery(id+"F0.wireOp",EDGE,"E2.4.1.0");var subQ2=makeQuery(id+"F0.imprint","INTERSECT",VERTEX,{"disambiguationData":[OD(0.0)],"derivedFrom":[subQ1,subQ0]});Q212=makeQuery(id+"F0.imprint","IMPRINT",FACE,{"disambiguationData":[TD([[makeQuery(id+"F0.imprint","IMPRINT",EDGE,{"disambiguationData":[TD([[subQ2,1.0]])],"derivedFrom":subQ1}),-1.0]])]});}
            var Q213;
            {var subQ0=sQuery(id+"F0.wireOp",EDGE,"E2.5.3.0");var subQ1=sQuery(id+"F0.wireOp",EDGE,"E2.4.3.0");var subQ2=makeQuery(id+"F0.imprint","INTERSECT",VERTEX,{"disambiguationData":[OD(0.0)],"derivedFrom":[subQ1,subQ0]});Q213=makeQuery(id+"F0.imprint","IMPRINT",FACE,{"disambiguationData":[TD([[makeQuery(id+"F0.imprint","IMPRINT",EDGE,{"disambiguationData":[TD([[subQ2,1.0]])],"derivedFrom":subQ1}),-1.0]])]});}
            var Q214;
            {var subQ0=sQuery(id+"F0.wireOp",EDGE,"E2.3.5.0");var subQ1=sQuery(id+"F0.wireOp",EDGE,"E2.2.5.0");var subQ2=makeQuery(id+"F0.imprint","INTERSECT",VERTEX,{"disambiguationData":[OD(0.0)],"derivedFrom":[subQ1,subQ0]});Q214=makeQuery(id+"F0.imprint","IMPRINT",FACE,{"disambiguationData":[TD([[makeQuery(id+"F0.imprint","IMPRINT",EDGE,{"disambiguationData":[TD([[subQ2,1.0]])],"derivedFrom":subQ1}),-1.0]])]});}
            var Q215;
            {var subQ0=sQuery(id+"F0.wireOp",EDGE,"E2.4.1.0");var subQ1=sQuery(id+"F0.wireOp",EDGE,"E2.3.1.0");var subQ2=makeQuery(id+"F0.imprint","INTERSECT",VERTEX,{"disambiguationData":[OD(0.0)],"derivedFrom":[subQ1,subQ0]});Q215=makeQuery(id+"F0.imprint","IMPRINT",FACE,{"disambiguationData":[TD([[makeQuery(id+"F0.imprint","IMPRINT",EDGE,{"disambiguationData":[TD([[subQ2,1.0]])],"derivedFrom":subQ1}),-1.0]])]});}
            var Q216;
            {var subQ0=sQuery(id+"F0.wireOp",EDGE,"E2.4.3.0");var subQ1=sQuery(id+"F0.wireOp",EDGE,"E2.3.3.0");var subQ2=makeQuery(id+"F0.imprint","INTERSECT",VERTEX,{"disambiguationData":[OD(0.0)],"derivedFrom":[subQ1,subQ0]});Q216=makeQuery(id+"F0.imprint","IMPRINT",FACE,{"disambiguationData":[TD([[makeQuery(id+"F0.imprint","IMPRINT",EDGE,{"disambiguationData":[TD([[subQ2,1.0]])],"derivedFrom":subQ1}),-1.0]])]});}
            var Q217;
            {var subQ0=sQuery(id+"F0.wireOp",EDGE,"E2.2.3.0");var subQ1=sQuery(id+"F0.wireOp",EDGE,"E2.1.3.0");var subQ2=makeQuery(id+"F0.imprint","INTERSECT",VERTEX,{"disambiguationData":[OD(0.0)],"derivedFrom":[subQ1,subQ0]});Q217=makeQuery(id+"F0.imprint","IMPRINT",FACE,{"disambiguationData":[TD([[makeQuery(id+"F0.imprint","IMPRINT",EDGE,{"disambiguationData":[TD([[subQ2,1.0]])],"derivedFrom":subQ1}),-1.0]])]});}
            var Q218;
            {var subQ0=sQuery(id+"F0.wireOp",EDGE,"E2.2.5.0");var subQ1=sQuery(id+"F0.wireOp",EDGE,"E2.1.5.0");var subQ2=makeQuery(id+"F0.imprint","INTERSECT",VERTEX,{"disambiguationData":[OD(0.0)],"derivedFrom":[subQ1,subQ0]});Q218=makeQuery(id+"F0.imprint","IMPRINT",FACE,{"disambiguationData":[TD([[makeQuery(id+"F0.imprint","IMPRINT",EDGE,{"disambiguationData":[TD([[subQ2,1.0]])],"derivedFrom":subQ1}),-1.0]])]});}
            var Q219;
            {var subQ0=sQuery(id+"F0.wireOp",EDGE,"E2.3.1.0");var subQ1=sQuery(id+"F0.wireOp",EDGE,"E2.2.1.0");var subQ2=makeQuery(id+"F0.imprint","INTERSECT",VERTEX,{"disambiguationData":[OD(0.0)],"derivedFrom":[subQ1,subQ0]});Q219=makeQuery(id+"F0.imprint","IMPRINT",FACE,{"disambiguationData":[TD([[makeQuery(id+"F0.imprint","IMPRINT",EDGE,{"disambiguationData":[TD([[subQ2,1.0]])],"derivedFrom":subQ1}),-1.0]])]});}
            var Q220;
            {var subQ0=sQuery(id+"F0.wireOp",EDGE,"E2.1.0.0");var subQ1=sQuery(id+"F0.wireOp",EDGE,"E1.0");var subQ2=makeQuery(id+"F0.imprint","INTERSECT",VERTEX,{"disambiguationData":[OD(1.0)],"derivedFrom":[subQ1,subQ0]});Q220=makeQuery(id+"F0.imprint","IMPRINT",FACE,{"disambiguationData":[TD([[makeQuery(id+"F0.imprint","IMPRINT",EDGE,{"disambiguationData":[TD([[subQ2,1.0]])],"derivedFrom":subQ1}),-1.0]])]});}
            var Q221;
            {var subQ0=sQuery(id+"F0.wireOp",EDGE,"E2.0.3.0");var subQ1=sQuery(id+"F0.wireOp",EDGE,"E2.0.2.0");var subQ2=makeQuery(id+"F0.imprint","INTERSECT",VERTEX,{"disambiguationData":[OD(1.0)],"derivedFrom":[subQ1,subQ0]});Q221=makeQuery(id+"F0.imprint","IMPRINT",FACE,{"disambiguationData":[TD([[makeQuery(id+"F0.imprint","IMPRINT",EDGE,{"disambiguationData":[TD([[subQ2,-1.0]])],"derivedFrom":subQ1}),-1.0]])]});}
            var Q222;
            {var subQ0=sQuery(id+"F0.wireOp",EDGE,"E2.2.1.0");var subQ1=sQuery(id+"F0.wireOp",EDGE,"E2.1.1.0");var subQ2=makeQuery(id+"F0.imprint","INTERSECT",VERTEX,{"disambiguationData":[OD(0.0)],"derivedFrom":[subQ1,subQ0]});Q222=makeQuery(id+"F0.imprint","IMPRINT",FACE,{"disambiguationData":[TD([[makeQuery(id+"F0.imprint","IMPRINT",EDGE,{"disambiguationData":[TD([[subQ2,1.0]])],"derivedFrom":subQ1}),-1.0]])]});}
            var Q223;
            {var subQ0=sQuery(id+"F0.wireOp",EDGE,"E2.10.3.0");var subQ1=sQuery(id+"F0.wireOp",EDGE,"E2.9.3.0");var subQ2=makeQuery(id+"F0.imprint","INTERSECT",VERTEX,{"disambiguationData":[OD(0.0)],"derivedFrom":[subQ1,subQ0]});Q223=makeQuery(id+"F0.imprint","IMPRINT",FACE,{"disambiguationData":[TD([[makeQuery(id+"F0.imprint","IMPRINT",EDGE,{"disambiguationData":[TD([[subQ2,1.0]])],"derivedFrom":subQ1}),1.0]])]});}
            var Q224;
            {var subQ0=sQuery(id+"F0.wireOp",EDGE,"E2.10.5.0");var subQ1=sQuery(id+"F0.wireOp",EDGE,"E2.9.5.0");var subQ2=makeQuery(id+"F0.imprint","INTERSECT",VERTEX,{"disambiguationData":[OD(0.0)],"derivedFrom":[subQ1,subQ0]});Q224=makeQuery(id+"F0.imprint","IMPRINT",FACE,{"disambiguationData":[TD([[makeQuery(id+"F0.imprint","IMPRINT",EDGE,{"disambiguationData":[TD([[subQ2,1.0]])],"derivedFrom":subQ1}),1.0]])]});}
            var Q225;
            {var subQ0=sQuery(id+"F0.wireOp",EDGE,"E2.9.1.0");var subQ1=sQuery(id+"F0.wireOp",EDGE,"E2.8.1.0");var subQ2=makeQuery(id+"F0.imprint","INTERSECT",VERTEX,{"disambiguationData":[OD(0.0)],"derivedFrom":[subQ1,subQ0]});Q225=makeQuery(id+"F0.imprint","IMPRINT",FACE,{"disambiguationData":[TD([[makeQuery(id+"F0.imprint","IMPRINT",EDGE,{"disambiguationData":[TD([[subQ2,1.0]])],"derivedFrom":subQ1}),1.0]])]});}
            var Q226;
            {var subQ0=sQuery(id+"F0.wireOp",EDGE,"E2.9.3.0");var subQ1=sQuery(id+"F0.wireOp",EDGE,"E2.8.3.0");var subQ2=makeQuery(id+"F0.imprint","INTERSECT",VERTEX,{"disambiguationData":[OD(0.0)],"derivedFrom":[subQ1,subQ0]});Q226=makeQuery(id+"F0.imprint","IMPRINT",FACE,{"disambiguationData":[TD([[makeQuery(id+"F0.imprint","IMPRINT",EDGE,{"disambiguationData":[TD([[subQ2,1.0]])],"derivedFrom":subQ1}),1.0]])]});}
            var Q227;
            {var subQ0=sQuery(id+"F0.wireOp",EDGE,"E2.9.5.0");var subQ1=sQuery(id+"F0.wireOp",EDGE,"E2.8.5.0");var subQ2=makeQuery(id+"F0.imprint","INTERSECT",VERTEX,{"disambiguationData":[OD(0.0)],"derivedFrom":[subQ1,subQ0]});Q227=makeQuery(id+"F0.imprint","IMPRINT",FACE,{"disambiguationData":[TD([[makeQuery(id+"F0.imprint","IMPRINT",EDGE,{"disambiguationData":[TD([[subQ2,1.0]])],"derivedFrom":subQ1}),1.0]])]});}
            var Q228;
            {var subQ0=sQuery(id+"F0.wireOp",EDGE,"E2.10.1.0");var subQ1=sQuery(id+"F0.wireOp",EDGE,"E2.9.1.0");var subQ2=makeQuery(id+"F0.imprint","INTERSECT",VERTEX,{"disambiguationData":[OD(0.0)],"derivedFrom":[subQ1,subQ0]});Q228=makeQuery(id+"F0.imprint","IMPRINT",FACE,{"disambiguationData":[TD([[makeQuery(id+"F0.imprint","IMPRINT",EDGE,{"disambiguationData":[TD([[subQ2,1.0]])],"derivedFrom":subQ1}),1.0]])]});}
            var Q229;
            {var subQ0=sQuery(id+"F0.wireOp",EDGE,"E2.8.3.0");var subQ1=sQuery(id+"F0.wireOp",EDGE,"E2.7.3.0");var subQ2=makeQuery(id+"F0.imprint","INTERSECT",VERTEX,{"disambiguationData":[OD(0.0)],"derivedFrom":[subQ1,subQ0]});Q229=makeQuery(id+"F0.imprint","IMPRINT",FACE,{"disambiguationData":[TD([[makeQuery(id+"F0.imprint","IMPRINT",EDGE,{"disambiguationData":[TD([[subQ2,1.0]])],"derivedFrom":subQ1}),1.0]])]});}
            var Q230;
            {var subQ0=sQuery(id+"F0.wireOp",EDGE,"E2.8.5.0");var subQ1=sQuery(id+"F0.wireOp",EDGE,"E2.7.5.0");var subQ2=makeQuery(id+"F0.imprint","INTERSECT",VERTEX,{"disambiguationData":[OD(0.0)],"derivedFrom":[subQ1,subQ0]});Q230=makeQuery(id+"F0.imprint","IMPRINT",FACE,{"disambiguationData":[TD([[makeQuery(id+"F0.imprint","IMPRINT",EDGE,{"disambiguationData":[TD([[subQ2,1.0]])],"derivedFrom":subQ1}),1.0]])]});}
            var Q231;
            {var subQ0=sQuery(id+"F0.wireOp",EDGE,"E2.7.1.0");var subQ1=sQuery(id+"F0.wireOp",EDGE,"E2.6.1.0");var subQ2=makeQuery(id+"F0.imprint","INTERSECT",VERTEX,{"disambiguationData":[OD(0.0)],"derivedFrom":[subQ1,subQ0]});Q231=makeQuery(id+"F0.imprint","IMPRINT",FACE,{"disambiguationData":[TD([[makeQuery(id+"F0.imprint","IMPRINT",EDGE,{"disambiguationData":[TD([[subQ2,1.0]])],"derivedFrom":subQ1}),1.0]])]});}
            var Q232;
            {var subQ0=sQuery(id+"F0.wireOp",EDGE,"E2.7.3.0");var subQ1=sQuery(id+"F0.wireOp",EDGE,"E2.6.3.0");var subQ2=makeQuery(id+"F0.imprint","INTERSECT",VERTEX,{"disambiguationData":[OD(0.0)],"derivedFrom":[subQ1,subQ0]});Q232=makeQuery(id+"F0.imprint","IMPRINT",FACE,{"disambiguationData":[TD([[makeQuery(id+"F0.imprint","IMPRINT",EDGE,{"disambiguationData":[TD([[subQ2,1.0]])],"derivedFrom":subQ1}),1.0]])]});}
            var Q233;
            {var subQ0=sQuery(id+"F0.wireOp",EDGE,"E2.7.5.0");var subQ1=sQuery(id+"F0.wireOp",EDGE,"E2.6.5.0");var subQ2=makeQuery(id+"F0.imprint","INTERSECT",VERTEX,{"disambiguationData":[OD(0.0)],"derivedFrom":[subQ1,subQ0]});Q233=makeQuery(id+"F0.imprint","IMPRINT",FACE,{"disambiguationData":[TD([[makeQuery(id+"F0.imprint","IMPRINT",EDGE,{"disambiguationData":[TD([[subQ2,1.0]])],"derivedFrom":subQ1}),1.0]])]});}
            var Q234;
            {var subQ0=sQuery(id+"F0.wireOp",EDGE,"E2.8.1.0");var subQ1=sQuery(id+"F0.wireOp",EDGE,"E2.7.1.0");var subQ2=makeQuery(id+"F0.imprint","INTERSECT",VERTEX,{"disambiguationData":[OD(0.0)],"derivedFrom":[subQ1,subQ0]});Q234=makeQuery(id+"F0.imprint","IMPRINT",FACE,{"disambiguationData":[TD([[makeQuery(id+"F0.imprint","IMPRINT",EDGE,{"disambiguationData":[TD([[subQ2,1.0]])],"derivedFrom":subQ1}),1.0]])]});}
            var Q235;
            {var subQ0=sQuery(id+"F0.wireOp",EDGE,"E2.5.5.0");var subQ1=sQuery(id+"F0.wireOp",EDGE,"E2.4.5.0");var subQ2=makeQuery(id+"F0.imprint","INTERSECT",VERTEX,{"disambiguationData":[OD(0.0)],"derivedFrom":[subQ1,subQ0]});Q235=makeQuery(id+"F0.imprint","IMPRINT",FACE,{"disambiguationData":[TD([[makeQuery(id+"F0.imprint","IMPRINT",EDGE,{"disambiguationData":[TD([[subQ2,1.0]])],"derivedFrom":subQ1}),1.0]])]});}
            var Q236;
            {var subQ0=sQuery(id+"F0.wireOp",EDGE,"E2.4.3.0");var subQ1=sQuery(id+"F0.wireOp",EDGE,"E2.3.3.0");var subQ2=makeQuery(id+"F0.imprint","INTERSECT",VERTEX,{"disambiguationData":[OD(0.0)],"derivedFrom":[subQ1,subQ0]});Q236=makeQuery(id+"F0.imprint","IMPRINT",FACE,{"disambiguationData":[TD([[makeQuery(id+"F0.imprint","IMPRINT",EDGE,{"disambiguationData":[TD([[subQ2,1.0]])],"derivedFrom":subQ1}),1.0]])]});}
            var Q237;
            {var subQ0=sQuery(id+"F0.wireOp",EDGE,"E2.4.5.0");var subQ1=sQuery(id+"F0.wireOp",EDGE,"E2.3.5.0");var subQ2=makeQuery(id+"F0.imprint","INTERSECT",VERTEX,{"disambiguationData":[OD(0.0)],"derivedFrom":[subQ1,subQ0]});Q237=makeQuery(id+"F0.imprint","IMPRINT",FACE,{"disambiguationData":[TD([[makeQuery(id+"F0.imprint","IMPRINT",EDGE,{"disambiguationData":[TD([[subQ2,1.0]])],"derivedFrom":subQ1}),1.0]])]});}
            var Q238;
            {var subQ0=sQuery(id+"F0.wireOp",EDGE,"E2.5.1.0");var subQ1=sQuery(id+"F0.wireOp",EDGE,"E2.4.1.0");var subQ2=makeQuery(id+"F0.imprint","INTERSECT",VERTEX,{"disambiguationData":[OD(0.0)],"derivedFrom":[subQ1,subQ0]});Q238=makeQuery(id+"F0.imprint","IMPRINT",FACE,{"disambiguationData":[TD([[makeQuery(id+"F0.imprint","IMPRINT",EDGE,{"disambiguationData":[TD([[subQ2,1.0]])],"derivedFrom":subQ1}),1.0]])]});}
            var Q239;
            {var subQ0=sQuery(id+"F0.wireOp",EDGE,"E2.5.3.0");var subQ1=sQuery(id+"F0.wireOp",EDGE,"E2.4.3.0");var subQ2=makeQuery(id+"F0.imprint","INTERSECT",VERTEX,{"disambiguationData":[OD(0.0)],"derivedFrom":[subQ1,subQ0]});Q239=makeQuery(id+"F0.imprint","IMPRINT",FACE,{"disambiguationData":[TD([[makeQuery(id+"F0.imprint","IMPRINT",EDGE,{"disambiguationData":[TD([[subQ2,1.0]])],"derivedFrom":subQ1}),1.0]])]});}
            var Q240;
            {var subQ0=sQuery(id+"F0.wireOp",EDGE,"E2.3.1.0");var subQ1=sQuery(id+"F0.wireOp",EDGE,"E2.2.1.0");var subQ2=makeQuery(id+"F0.imprint","INTERSECT",VERTEX,{"disambiguationData":[OD(0.0)],"derivedFrom":[subQ1,subQ0]});Q240=makeQuery(id+"F0.imprint","IMPRINT",FACE,{"disambiguationData":[TD([[makeQuery(id+"F0.imprint","IMPRINT",EDGE,{"disambiguationData":[TD([[subQ2,1.0]])],"derivedFrom":subQ1}),1.0]])]});}
            var Q241;
            {var subQ0=sQuery(id+"F0.wireOp",EDGE,"E2.3.3.0");var subQ1=sQuery(id+"F0.wireOp",EDGE,"E2.2.3.0");var subQ2=makeQuery(id+"F0.imprint","INTERSECT",VERTEX,{"disambiguationData":[OD(0.0)],"derivedFrom":[subQ1,subQ0]});Q241=makeQuery(id+"F0.imprint","IMPRINT",FACE,{"disambiguationData":[TD([[makeQuery(id+"F0.imprint","IMPRINT",EDGE,{"disambiguationData":[TD([[subQ2,1.0]])],"derivedFrom":subQ1}),1.0]])]});}
            var Q242;
            {var subQ0=sQuery(id+"F0.wireOp",EDGE,"E2.3.5.0");var subQ1=sQuery(id+"F0.wireOp",EDGE,"E2.2.5.0");var subQ2=makeQuery(id+"F0.imprint","INTERSECT",VERTEX,{"disambiguationData":[OD(0.0)],"derivedFrom":[subQ1,subQ0]});Q242=makeQuery(id+"F0.imprint","IMPRINT",FACE,{"disambiguationData":[TD([[makeQuery(id+"F0.imprint","IMPRINT",EDGE,{"disambiguationData":[TD([[subQ2,1.0]])],"derivedFrom":subQ1}),1.0]])]});}
            var Q243;
            {var subQ0=sQuery(id+"F0.wireOp",EDGE,"E2.4.1.0");var subQ1=sQuery(id+"F0.wireOp",EDGE,"E2.3.1.0");var subQ2=makeQuery(id+"F0.imprint","INTERSECT",VERTEX,{"disambiguationData":[OD(0.0)],"derivedFrom":[subQ1,subQ0]});Q243=makeQuery(id+"F0.imprint","IMPRINT",FACE,{"disambiguationData":[TD([[makeQuery(id+"F0.imprint","IMPRINT",EDGE,{"disambiguationData":[TD([[subQ2,1.0]])],"derivedFrom":subQ1}),1.0]])]});}
            var Q244;
            {var subQ0=sQuery(id+"F0.wireOp",EDGE,"E2.1.4.1");var subQ1=sQuery(id+"F0.wireOp",EDGE,"E2.0.4.0");var subQ2=makeQuery(id+"F0.imprint","INTERSECT",VERTEX,{"derivedFrom":[subQ1,subQ0]});Q244=makeQuery(id+"F0.imprint","IMPRINT",FACE,{"disambiguationData":[TD([[makeQuery(id+"F0.imprint","IMPRINT",EDGE,{"disambiguationData":[TD([[subQ2,1.0]])],"derivedFrom":subQ1}),-1.0]])]});}
            var Q245;
            {var subQ0=sQuery(id+"F0.wireOp",EDGE,"E2.2.1.0");var subQ1=sQuery(id+"F0.wireOp",EDGE,"E2.1.1.0");var subQ2=makeQuery(id+"F0.imprint","INTERSECT",VERTEX,{"disambiguationData":[OD(0.0)],"derivedFrom":[subQ1,subQ0]});Q245=makeQuery(id+"F0.imprint","IMPRINT",FACE,{"disambiguationData":[TD([[makeQuery(id+"F0.imprint","IMPRINT",EDGE,{"disambiguationData":[TD([[subQ2,1.0]])],"derivedFrom":subQ1}),1.0]])]});}
            var Q246;
            {var subQ0=sQuery(id+"F0.wireOp",EDGE,"E2.2.3.0");var subQ1=sQuery(id+"F0.wireOp",EDGE,"E2.1.3.0");var subQ2=makeQuery(id+"F0.imprint","INTERSECT",VERTEX,{"disambiguationData":[OD(0.0)],"derivedFrom":[subQ1,subQ0]});Q246=makeQuery(id+"F0.imprint","IMPRINT",FACE,{"disambiguationData":[TD([[makeQuery(id+"F0.imprint","IMPRINT",EDGE,{"disambiguationData":[TD([[subQ2,1.0]])],"derivedFrom":subQ1}),1.0]])]});}
            var Q247;
            {var subQ0=sQuery(id+"F0.wireOp",EDGE,"E2.2.5.0");var subQ1=sQuery(id+"F0.wireOp",EDGE,"E2.1.5.0");var subQ2=makeQuery(id+"F0.imprint","INTERSECT",VERTEX,{"disambiguationData":[OD(0.0)],"derivedFrom":[subQ1,subQ0]});Q247=makeQuery(id+"F0.imprint","IMPRINT",FACE,{"disambiguationData":[TD([[makeQuery(id+"F0.imprint","IMPRINT",EDGE,{"disambiguationData":[TD([[subQ2,1.0]])],"derivedFrom":subQ1}),1.0]])]});}
            var Q248;
            {var subQ0=sQuery(id+"F0.wireOp",EDGE,"E2.1.0.0");var subQ1=sQuery(id+"F0.wireOp",EDGE,"E1.0");var subQ2=makeQuery(id+"F0.imprint","INTERSECT",VERTEX,{"disambiguationData":[OD(1.0)],"derivedFrom":[subQ1,subQ0]});Q248=makeQuery(id+"F0.imprint","IMPRINT",FACE,{"disambiguationData":[TD([[makeQuery(id+"F0.imprint","IMPRINT",EDGE,{"disambiguationData":[TD([[subQ2,1.0]])],"derivedFrom":subQ1}),1.0]])]});}
            var Q249;
            {var subQ0=sQuery(id+"F0.wireOp",EDGE,"E2.0.3.0");var subQ1=sQuery(id+"F0.wireOp",EDGE,"E2.0.2.0");var subQ2=makeQuery(id+"F0.imprint","INTERSECT",VERTEX,{"disambiguationData":[OD(1.0)],"derivedFrom":[subQ1,subQ0]});Q249=makeQuery(id+"F0.imprint","IMPRINT",FACE,{"disambiguationData":[TD([[makeQuery(id+"F0.imprint","IMPRINT",EDGE,{"disambiguationData":[TD([[subQ2,-1.0]])],"derivedFrom":subQ1}),1.0]])]});}
            var Q250;
            {var subQ0=sQuery(id+"F0.wireOp",EDGE,"E2.11.6.0");var subQ1=sQuery(id+"F0.wireOp",EDGE,"E2.11.5.0");var subQ2=makeQuery(id+"F0.imprint","INTERSECT",VERTEX,{"disambiguationData":[OD(0.0)],"derivedFrom":[subQ1,subQ0]});Q250=makeQuery(id+"F0.imprint","IMPRINT",FACE,{"disambiguationData":[TD([[makeQuery(id+"F0.imprint","IMPRINT",EDGE,{"disambiguationData":[TD([[subQ2,-1.0]])],"derivedFrom":subQ1}),1.0]])]});}
            var Q251;
            {var subQ0=sQuery(id+"F0.wireOp",EDGE,"E2.8.1.0");var subQ1=sQuery(id+"F0.wireOp",EDGE,"E2.8.0.0");var subQ2=makeQuery(id+"F0.imprint","INTERSECT",VERTEX,{"disambiguationData":[OD(0.0)],"derivedFrom":[subQ1,subQ0]});Q251=makeQuery(id+"F0.imprint","IMPRINT",FACE,{"disambiguationData":[TD([[makeQuery(id+"F0.imprint","IMPRINT",EDGE,{"disambiguationData":[TD([[subQ2,-1.0]])],"derivedFrom":subQ1}),-1.0]])]});}
            var Q252;
            {var subQ0=sQuery(id+"F0.wireOp",EDGE,"E2.9.1.0");var subQ1=sQuery(id+"F0.wireOp",EDGE,"E2.9.0.0");var subQ2=makeQuery(id+"F0.imprint","INTERSECT",VERTEX,{"disambiguationData":[OD(0.0)],"derivedFrom":[subQ1,subQ0]});Q252=makeQuery(id+"F0.imprint","IMPRINT",FACE,{"disambiguationData":[TD([[makeQuery(id+"F0.imprint","IMPRINT",EDGE,{"disambiguationData":[TD([[subQ2,-1.0]])],"derivedFrom":subQ1}),-1.0]])]});}
            var Q253;
            {var subQ0=sQuery(id+"F0.wireOp",EDGE,"E2.6.1.0");var subQ1=sQuery(id+"F0.wireOp",EDGE,"E2.6.0.0");var subQ2=makeQuery(id+"F0.imprint","INTERSECT",VERTEX,{"disambiguationData":[OD(0.0)],"derivedFrom":[subQ1,subQ0]});Q253=makeQuery(id+"F0.imprint","IMPRINT",FACE,{"disambiguationData":[TD([[makeQuery(id+"F0.imprint","IMPRINT",EDGE,{"disambiguationData":[TD([[subQ2,-1.0]])],"derivedFrom":subQ1}),-1.0]])]});}
            var Q254;
            {var subQ0=sQuery(id+"F0.wireOp",EDGE,"E2.7.1.0");var subQ1=sQuery(id+"F0.wireOp",EDGE,"E2.7.0.0");var subQ2=makeQuery(id+"F0.imprint","INTERSECT",VERTEX,{"disambiguationData":[OD(0.0)],"derivedFrom":[subQ1,subQ0]});Q254=makeQuery(id+"F0.imprint","IMPRINT",FACE,{"disambiguationData":[TD([[makeQuery(id+"F0.imprint","IMPRINT",EDGE,{"disambiguationData":[TD([[subQ2,-1.0]])],"derivedFrom":subQ1}),-1.0]])]});}
            var Q255;
            {var subQ0=sQuery(id+"F0.wireOp",EDGE,"E2.4.1.0");var subQ1=sQuery(id+"F0.wireOp",EDGE,"E2.4.0.0");var subQ2=makeQuery(id+"F0.imprint","INTERSECT",VERTEX,{"disambiguationData":[OD(0.0)],"derivedFrom":[subQ1,subQ0]});Q255=makeQuery(id+"F0.imprint","IMPRINT",FACE,{"disambiguationData":[TD([[makeQuery(id+"F0.imprint","IMPRINT",EDGE,{"disambiguationData":[TD([[subQ2,-1.0]])],"derivedFrom":subQ1}),-1.0]])]});}
            var Q256;
            {var subQ0=sQuery(id+"F0.wireOp",EDGE,"E2.2.1.0");var subQ1=sQuery(id+"F0.wireOp",EDGE,"E2.2.0.0");var subQ2=makeQuery(id+"F0.imprint","INTERSECT",VERTEX,{"disambiguationData":[OD(0.0)],"derivedFrom":[subQ1,subQ0]});Q256=makeQuery(id+"F0.imprint","IMPRINT",FACE,{"disambiguationData":[TD([[makeQuery(id+"F0.imprint","IMPRINT",EDGE,{"disambiguationData":[TD([[subQ2,-1.0]])],"derivedFrom":subQ1}),-1.0]])]});}
            var Q257;
            {var subQ0=sQuery(id+"F0.wireOp",EDGE,"E2.3.1.0");var subQ1=sQuery(id+"F0.wireOp",EDGE,"E2.3.0.0");var subQ2=makeQuery(id+"F0.imprint","INTERSECT",VERTEX,{"disambiguationData":[OD(0.0)],"derivedFrom":[subQ1,subQ0]});Q257=makeQuery(id+"F0.imprint","IMPRINT",FACE,{"disambiguationData":[TD([[makeQuery(id+"F0.imprint","IMPRINT",EDGE,{"disambiguationData":[TD([[subQ2,-1.0]])],"derivedFrom":subQ1}),-1.0]])]});}
            var Q258;
            {var subQ0=sQuery(id+"F0.wireOp",EDGE,"E2.0.5.0");var subQ1=sQuery(id+"F0.wireOp",EDGE,"E2.0.4.0");var subQ2=makeQuery(id+"F0.imprint","INTERSECT",VERTEX,{"disambiguationData":[OD(1.0)],"derivedFrom":[subQ1,subQ0]});Q258=makeQuery(id+"F0.imprint","IMPRINT",FACE,{"disambiguationData":[TD([[makeQuery(id+"F0.imprint","IMPRINT",EDGE,{"disambiguationData":[TD([[subQ2,-1.0]])],"derivedFrom":subQ1}),-1.0]])]});}
            var Q259;
            {var subQ0=sQuery(id+"F0.wireOp",EDGE,"E2.1.1.0");var subQ1=sQuery(id+"F0.wireOp",EDGE,"E2.1.0.0");var subQ2=makeQuery(id+"F0.imprint","INTERSECT",VERTEX,{"disambiguationData":[OD(0.0)],"derivedFrom":[subQ1,subQ0]});Q259=makeQuery(id+"F0.imprint","IMPRINT",FACE,{"disambiguationData":[TD([[makeQuery(id+"F0.imprint","IMPRINT",EDGE,{"disambiguationData":[TD([[subQ2,-1.0]])],"derivedFrom":subQ1}),-1.0]])]});}
            var Q260;
            {var subQ0=sQuery(id+"F0.wireOp",EDGE,"E2.0.1.0");var subQ1=sQuery(id+"F0.wireOp",EDGE,"E0");var subQ2=makeQuery(id+"F0.imprint","INTERSECT",VERTEX,{"derivedFrom":[subQ1,subQ0]});Q260=makeQuery(id+"F0.imprint","IMPRINT",FACE,{"disambiguationData":[TD([[makeQuery(id+"F0.imprint","IMPRINT",EDGE,{"disambiguationData":[TD([[subQ2,1.0]])],"derivedFrom":subQ1}),-1.0]])]});}
            var Q261;
            {var subQ0=sQuery(id+"F0.wireOp",EDGE,"E2.2.6.0");var subQ1=sQuery(id+"F0.wireOp",EDGE,"E2.1.6.0");var subQ2=makeQuery(id+"F0.imprint","INTERSECT",VERTEX,{"disambiguationData":[OD(0.0)],"derivedFrom":[subQ1,subQ0]});Q261=makeQuery(id+"F0.imprint","IMPRINT",FACE,{"disambiguationData":[TD([[makeQuery(id+"F0.imprint","IMPRINT",EDGE,{"disambiguationData":[TD([[subQ2,1.0]])],"derivedFrom":subQ1}),-1.0]])]});}
            var Q262;
            {var subQ0=sQuery(id+"F0.wireOp",EDGE,"E2.11.4.1");var subQ1=sQuery(id+"F0.wireOp",EDGE,"E2.10.4.0");var subQ2=makeQuery(id+"F0.imprint","INTERSECT",VERTEX,{"derivedFrom":[subQ1,subQ0]});Q262=makeQuery(id+"F0.imprint","IMPRINT",FACE,{"disambiguationData":[TD([[makeQuery(id+"F0.imprint","IMPRINT",EDGE,{"disambiguationData":[TD([[subQ2,1.0]])],"derivedFrom":subQ1}),-1.0]])]});}
            var Q263;
            {var subQ0=sQuery(id+"F0.wireOp",EDGE,"E2.11.5.0");var subQ1=sQuery(id+"F0.wireOp",EDGE,"E2.11.4.0");var subQ2=makeQuery(id+"F0.imprint","INTERSECT",VERTEX,{"disambiguationData":[OD(0.0)],"derivedFrom":[subQ1,subQ0]});Q263=makeQuery(id+"F0.imprint","IMPRINT",FACE,{"disambiguationData":[TD([[makeQuery(id+"F0.imprint","IMPRINT",EDGE,{"disambiguationData":[TD([[subQ2,-1.0]])],"derivedFrom":subQ1}),1.0]])]});}
            var Q264;
            {var subQ0=sQuery(id+"F0.wireOp",EDGE,"E2.10.2.1");var subQ1=sQuery(id+"F0.wireOp",EDGE,"E2.9.2.0");var subQ2=makeQuery(id+"F0.imprint","INTERSECT",VERTEX,{"derivedFrom":[subQ1,subQ0]});Q264=makeQuery(id+"F0.imprint","IMPRINT",FACE,{"disambiguationData":[TD([[makeQuery(id+"F0.imprint","IMPRINT",EDGE,{"disambiguationData":[TD([[subQ2,1.0]])],"derivedFrom":subQ1}),-1.0]])]});}
            var Q265;
            {var subQ0=sQuery(id+"F0.wireOp",EDGE,"E2.10.4.1");var subQ1=sQuery(id+"F0.wireOp",EDGE,"E2.9.4.0");var subQ2=makeQuery(id+"F0.imprint","INTERSECT",VERTEX,{"derivedFrom":[subQ1,subQ0]});Q265=makeQuery(id+"F0.imprint","IMPRINT",FACE,{"disambiguationData":[TD([[makeQuery(id+"F0.imprint","IMPRINT",EDGE,{"disambiguationData":[TD([[subQ2,1.0]])],"derivedFrom":subQ1}),-1.0]])]});}
            var Q266;
            {var subQ0=sQuery(id+"F0.wireOp",EDGE,"E2.10.1.0");var subQ1=sQuery(id+"F0.wireOp",EDGE,"E2.10.0.0");var subQ2=makeQuery(id+"F0.imprint","INTERSECT",VERTEX,{"disambiguationData":[OD(0.0)],"derivedFrom":[subQ1,subQ0]});Q266=makeQuery(id+"F0.imprint","IMPRINT",FACE,{"disambiguationData":[TD([[makeQuery(id+"F0.imprint","IMPRINT",EDGE,{"disambiguationData":[TD([[subQ2,-1.0]])],"derivedFrom":subQ1}),1.0]])]});}
            var Q267;
            {var subQ0=sQuery(id+"F0.wireOp",EDGE,"E2.11.2.1");var subQ1=sQuery(id+"F0.wireOp",EDGE,"E2.10.2.0");var subQ2=makeQuery(id+"F0.imprint","INTERSECT",VERTEX,{"derivedFrom":[subQ1,subQ0]});Q267=makeQuery(id+"F0.imprint","IMPRINT",FACE,{"disambiguationData":[TD([[makeQuery(id+"F0.imprint","IMPRINT",EDGE,{"disambiguationData":[TD([[subQ2,1.0]])],"derivedFrom":subQ1}),-1.0]])]});}
            var Q268;
            {var subQ0=sQuery(id+"F0.wireOp",EDGE,"E2.8.1.0");var subQ1=sQuery(id+"F0.wireOp",EDGE,"E2.8.0.0");var subQ2=makeQuery(id+"F0.imprint","INTERSECT",VERTEX,{"disambiguationData":[OD(0.0)],"derivedFrom":[subQ1,subQ0]});Q268=makeQuery(id+"F0.imprint","IMPRINT",FACE,{"disambiguationData":[TD([[makeQuery(id+"F0.imprint","IMPRINT",EDGE,{"disambiguationData":[TD([[subQ2,-1.0]])],"derivedFrom":subQ1}),1.0]])]});}
            var Q269;
            {var subQ0=sQuery(id+"F0.wireOp",EDGE,"E2.9.2.1");var subQ1=sQuery(id+"F0.wireOp",EDGE,"E2.8.2.0");var subQ2=makeQuery(id+"F0.imprint","INTERSECT",VERTEX,{"derivedFrom":[subQ1,subQ0]});Q269=makeQuery(id+"F0.imprint","IMPRINT",FACE,{"disambiguationData":[TD([[makeQuery(id+"F0.imprint","IMPRINT",EDGE,{"disambiguationData":[TD([[subQ2,1.0]])],"derivedFrom":subQ1}),-1.0]])]});}
            var Q270;
            {var subQ0=sQuery(id+"F0.wireOp",EDGE,"E2.9.4.1");var subQ1=sQuery(id+"F0.wireOp",EDGE,"E2.8.4.0");var subQ2=makeQuery(id+"F0.imprint","INTERSECT",VERTEX,{"derivedFrom":[subQ1,subQ0]});Q270=makeQuery(id+"F0.imprint","IMPRINT",FACE,{"disambiguationData":[TD([[makeQuery(id+"F0.imprint","IMPRINT",EDGE,{"disambiguationData":[TD([[subQ2,1.0]])],"derivedFrom":subQ1}),-1.0]])]});}
            var Q271;
            {var subQ0=sQuery(id+"F0.wireOp",EDGE,"E2.9.1.0");var subQ1=sQuery(id+"F0.wireOp",EDGE,"E2.9.0.0");var subQ2=makeQuery(id+"F0.imprint","INTERSECT",VERTEX,{"disambiguationData":[OD(0.0)],"derivedFrom":[subQ1,subQ0]});Q271=makeQuery(id+"F0.imprint","IMPRINT",FACE,{"disambiguationData":[TD([[makeQuery(id+"F0.imprint","IMPRINT",EDGE,{"disambiguationData":[TD([[subQ2,-1.0]])],"derivedFrom":subQ1}),1.0]])]});}
            var Q272;
            {var subQ0=sQuery(id+"F0.wireOp",EDGE,"E2.8.2.1");var subQ1=sQuery(id+"F0.wireOp",EDGE,"E2.7.2.0");var subQ2=makeQuery(id+"F0.imprint","INTERSECT",VERTEX,{"derivedFrom":[subQ1,subQ0]});Q272=makeQuery(id+"F0.imprint","IMPRINT",FACE,{"disambiguationData":[TD([[makeQuery(id+"F0.imprint","IMPRINT",EDGE,{"disambiguationData":[TD([[subQ2,1.0]])],"derivedFrom":subQ1}),-1.0]])]});}
            var Q273;
            {var subQ0=sQuery(id+"F0.wireOp",EDGE,"E2.8.4.1");var subQ1=sQuery(id+"F0.wireOp",EDGE,"E2.7.4.0");var subQ2=makeQuery(id+"F0.imprint","INTERSECT",VERTEX,{"derivedFrom":[subQ1,subQ0]});Q273=makeQuery(id+"F0.imprint","IMPRINT",FACE,{"disambiguationData":[TD([[makeQuery(id+"F0.imprint","IMPRINT",EDGE,{"disambiguationData":[TD([[subQ2,1.0]])],"derivedFrom":subQ1}),-1.0]])]});}
            var Q274;
            {var subQ0=sQuery(id+"F0.wireOp",EDGE,"E2.6.1.0");var subQ1=sQuery(id+"F0.wireOp",EDGE,"E2.6.0.0");var subQ2=makeQuery(id+"F0.imprint","INTERSECT",VERTEX,{"disambiguationData":[OD(0.0)],"derivedFrom":[subQ1,subQ0]});Q274=makeQuery(id+"F0.imprint","IMPRINT",FACE,{"disambiguationData":[TD([[makeQuery(id+"F0.imprint","IMPRINT",EDGE,{"disambiguationData":[TD([[subQ2,-1.0]])],"derivedFrom":subQ1}),1.0]])]});}
            var Q275;
            {var subQ0=sQuery(id+"F0.wireOp",EDGE,"E2.7.2.1");var subQ1=sQuery(id+"F0.wireOp",EDGE,"E2.6.2.0");var subQ2=makeQuery(id+"F0.imprint","INTERSECT",VERTEX,{"derivedFrom":[subQ1,subQ0]});Q275=makeQuery(id+"F0.imprint","IMPRINT",FACE,{"disambiguationData":[TD([[makeQuery(id+"F0.imprint","IMPRINT",EDGE,{"disambiguationData":[TD([[subQ2,1.0]])],"derivedFrom":subQ1}),-1.0]])]});}
            var Q276;
            {var subQ0=sQuery(id+"F0.wireOp",EDGE,"E2.7.1.0");var subQ1=sQuery(id+"F0.wireOp",EDGE,"E2.7.0.0");var subQ2=makeQuery(id+"F0.imprint","INTERSECT",VERTEX,{"disambiguationData":[OD(0.0)],"derivedFrom":[subQ1,subQ0]});Q276=makeQuery(id+"F0.imprint","IMPRINT",FACE,{"disambiguationData":[TD([[makeQuery(id+"F0.imprint","IMPRINT",EDGE,{"disambiguationData":[TD([[subQ2,-1.0]])],"derivedFrom":subQ1}),1.0]])]});}
            var Q277;
            {var subQ0=sQuery(id+"F0.wireOp",EDGE,"E2.5.4.1");var subQ1=sQuery(id+"F0.wireOp",EDGE,"E2.4.4.0");var subQ2=makeQuery(id+"F0.imprint","INTERSECT",VERTEX,{"derivedFrom":[subQ1,subQ0]});Q277=makeQuery(id+"F0.imprint","IMPRINT",FACE,{"disambiguationData":[TD([[makeQuery(id+"F0.imprint","IMPRINT",EDGE,{"disambiguationData":[TD([[subQ2,1.0]])],"derivedFrom":subQ1}),-1.0]])]});}
            var Q278;
            {var subQ0=sQuery(id+"F0.wireOp",EDGE,"E2.5.1.0");var subQ1=sQuery(id+"F0.wireOp",EDGE,"E2.5.0.0");var subQ2=makeQuery(id+"F0.imprint","INTERSECT",VERTEX,{"disambiguationData":[OD(0.0)],"derivedFrom":[subQ1,subQ0]});Q278=makeQuery(id+"F0.imprint","IMPRINT",FACE,{"disambiguationData":[TD([[makeQuery(id+"F0.imprint","IMPRINT",EDGE,{"disambiguationData":[TD([[subQ2,-1.0]])],"derivedFrom":subQ1}),1.0]])]});}
            var Q279;
            {var subQ0=sQuery(id+"F0.wireOp",EDGE,"E2.6.2.1");var subQ1=sQuery(id+"F0.wireOp",EDGE,"E2.5.2.0");var subQ2=makeQuery(id+"F0.imprint","INTERSECT",VERTEX,{"derivedFrom":[subQ1,subQ0]});Q279=makeQuery(id+"F0.imprint","IMPRINT",FACE,{"disambiguationData":[TD([[makeQuery(id+"F0.imprint","IMPRINT",EDGE,{"disambiguationData":[TD([[subQ2,1.0]])],"derivedFrom":subQ1}),-1.0]])]});}
            var Q280;
            {var subQ0=sQuery(id+"F0.wireOp",EDGE,"E2.6.4.1");var subQ1=sQuery(id+"F0.wireOp",EDGE,"E2.5.4.0");var subQ2=makeQuery(id+"F0.imprint","INTERSECT",VERTEX,{"derivedFrom":[subQ1,subQ0]});Q280=makeQuery(id+"F0.imprint","IMPRINT",FACE,{"disambiguationData":[TD([[makeQuery(id+"F0.imprint","IMPRINT",EDGE,{"disambiguationData":[TD([[subQ2,1.0]])],"derivedFrom":subQ1}),-1.0]])]});}
            var Q281;
            {var subQ0=sQuery(id+"F0.wireOp",EDGE,"E2.4.2.1");var subQ1=sQuery(id+"F0.wireOp",EDGE,"E2.3.2.0");var subQ2=makeQuery(id+"F0.imprint","INTERSECT",VERTEX,{"derivedFrom":[subQ1,subQ0]});Q281=makeQuery(id+"F0.imprint","IMPRINT",FACE,{"disambiguationData":[TD([[makeQuery(id+"F0.imprint","IMPRINT",EDGE,{"disambiguationData":[TD([[subQ2,1.0]])],"derivedFrom":subQ1}),-1.0]])]});}
            var Q282;
            {var subQ0=sQuery(id+"F0.wireOp",EDGE,"E2.4.4.1");var subQ1=sQuery(id+"F0.wireOp",EDGE,"E2.3.4.0");var subQ2=makeQuery(id+"F0.imprint","INTERSECT",VERTEX,{"derivedFrom":[subQ1,subQ0]});Q282=makeQuery(id+"F0.imprint","IMPRINT",FACE,{"disambiguationData":[TD([[makeQuery(id+"F0.imprint","IMPRINT",EDGE,{"disambiguationData":[TD([[subQ2,1.0]])],"derivedFrom":subQ1}),-1.0]])]});}
            var Q283;
            {var subQ0=sQuery(id+"F0.wireOp",EDGE,"E2.4.1.0");var subQ1=sQuery(id+"F0.wireOp",EDGE,"E2.4.0.0");var subQ2=makeQuery(id+"F0.imprint","INTERSECT",VERTEX,{"disambiguationData":[OD(0.0)],"derivedFrom":[subQ1,subQ0]});Q283=makeQuery(id+"F0.imprint","IMPRINT",FACE,{"disambiguationData":[TD([[makeQuery(id+"F0.imprint","IMPRINT",EDGE,{"disambiguationData":[TD([[subQ2,-1.0]])],"derivedFrom":subQ1}),1.0]])]});}
            var Q284;
            {var subQ0=sQuery(id+"F0.wireOp",EDGE,"E2.5.2.1");var subQ1=sQuery(id+"F0.wireOp",EDGE,"E2.4.2.0");var subQ2=makeQuery(id+"F0.imprint","INTERSECT",VERTEX,{"derivedFrom":[subQ1,subQ0]});Q284=makeQuery(id+"F0.imprint","IMPRINT",FACE,{"disambiguationData":[TD([[makeQuery(id+"F0.imprint","IMPRINT",EDGE,{"disambiguationData":[TD([[subQ2,1.0]])],"derivedFrom":subQ1}),-1.0]])]});}
            var Q285;
            {var subQ0=sQuery(id+"F0.wireOp",EDGE,"E2.2.1.0");var subQ1=sQuery(id+"F0.wireOp",EDGE,"E2.2.0.0");var subQ2=makeQuery(id+"F0.imprint","INTERSECT",VERTEX,{"disambiguationData":[OD(0.0)],"derivedFrom":[subQ1,subQ0]});Q285=makeQuery(id+"F0.imprint","IMPRINT",FACE,{"disambiguationData":[TD([[makeQuery(id+"F0.imprint","IMPRINT",EDGE,{"disambiguationData":[TD([[subQ2,-1.0]])],"derivedFrom":subQ1}),1.0]])]});}
            var Q286;
            {var subQ0=sQuery(id+"F0.wireOp",EDGE,"E2.3.2.1");var subQ1=sQuery(id+"F0.wireOp",EDGE,"E2.2.2.0");var subQ2=makeQuery(id+"F0.imprint","INTERSECT",VERTEX,{"derivedFrom":[subQ1,subQ0]});Q286=makeQuery(id+"F0.imprint","IMPRINT",FACE,{"disambiguationData":[TD([[makeQuery(id+"F0.imprint","IMPRINT",EDGE,{"disambiguationData":[TD([[subQ2,1.0]])],"derivedFrom":subQ1}),-1.0]])]});}
            var Q287;
            {var subQ0=sQuery(id+"F0.wireOp",EDGE,"E2.3.4.1");var subQ1=sQuery(id+"F0.wireOp",EDGE,"E2.2.4.0");var subQ2=makeQuery(id+"F0.imprint","INTERSECT",VERTEX,{"derivedFrom":[subQ1,subQ0]});Q287=makeQuery(id+"F0.imprint","IMPRINT",FACE,{"disambiguationData":[TD([[makeQuery(id+"F0.imprint","IMPRINT",EDGE,{"disambiguationData":[TD([[subQ2,1.0]])],"derivedFrom":subQ1}),-1.0]])]});}
            var Q288;
            {var subQ0=sQuery(id+"F0.wireOp",EDGE,"E2.3.1.0");var subQ1=sQuery(id+"F0.wireOp",EDGE,"E2.3.0.0");var subQ2=makeQuery(id+"F0.imprint","INTERSECT",VERTEX,{"disambiguationData":[OD(0.0)],"derivedFrom":[subQ1,subQ0]});Q288=makeQuery(id+"F0.imprint","IMPRINT",FACE,{"disambiguationData":[TD([[makeQuery(id+"F0.imprint","IMPRINT",EDGE,{"disambiguationData":[TD([[subQ2,-1.0]])],"derivedFrom":subQ1}),1.0]])]});}
            var Q289;
            {var subQ0=sQuery(id+"F0.wireOp",EDGE,"E2.0.5.0");var subQ1=sQuery(id+"F0.wireOp",EDGE,"E2.0.4.0");var subQ2=makeQuery(id+"F0.imprint","INTERSECT",VERTEX,{"disambiguationData":[OD(1.0)],"derivedFrom":[subQ1,subQ0]});Q289=makeQuery(id+"F0.imprint","IMPRINT",FACE,{"disambiguationData":[TD([[makeQuery(id+"F0.imprint","IMPRINT",EDGE,{"disambiguationData":[TD([[subQ2,-1.0]])],"derivedFrom":subQ1}),1.0]])]});}
            var Q290;
            {var subQ0=sQuery(id+"F0.wireOp",EDGE,"E2.1.1.0");var subQ1=sQuery(id+"F0.wireOp",EDGE,"E2.1.0.0");var subQ2=makeQuery(id+"F0.imprint","INTERSECT",VERTEX,{"disambiguationData":[OD(0.0)],"derivedFrom":[subQ1,subQ0]});Q290=makeQuery(id+"F0.imprint","IMPRINT",FACE,{"disambiguationData":[TD([[makeQuery(id+"F0.imprint","IMPRINT",EDGE,{"disambiguationData":[TD([[subQ2,-1.0]])],"derivedFrom":subQ1}),1.0]])]});}
            var Q291;
            {var subQ0=sQuery(id+"F0.wireOp",EDGE,"E2.2.2.1");var subQ1=sQuery(id+"F0.wireOp",EDGE,"E2.1.2.0");var subQ2=makeQuery(id+"F0.imprint","INTERSECT",VERTEX,{"derivedFrom":[subQ1,subQ0]});Q291=makeQuery(id+"F0.imprint","IMPRINT",FACE,{"disambiguationData":[TD([[makeQuery(id+"F0.imprint","IMPRINT",EDGE,{"disambiguationData":[TD([[subQ2,1.0]])],"derivedFrom":subQ1}),-1.0]])]});}
            var Q292;
            {var subQ0=sQuery(id+"F0.wireOp",EDGE,"E2.2.4.1");var subQ1=sQuery(id+"F0.wireOp",EDGE,"E2.1.4.0");var subQ2=makeQuery(id+"F0.imprint","INTERSECT",VERTEX,{"derivedFrom":[subQ1,subQ0]});Q292=makeQuery(id+"F0.imprint","IMPRINT",FACE,{"disambiguationData":[TD([[makeQuery(id+"F0.imprint","IMPRINT",EDGE,{"disambiguationData":[TD([[subQ2,1.0]])],"derivedFrom":subQ1}),-1.0]])]});}
            var Q293;
            {var subQ0=sQuery(id+"F0.wireOp",EDGE,"E2.1.2.0");var subQ1=sQuery(id+"F0.wireOp",EDGE,"E2.0.2.0");var subQ2=makeQuery(id+"F0.imprint","INTERSECT",VERTEX,{"disambiguationData":[OD(0.0)],"derivedFrom":[subQ1,subQ0]});Q293=makeQuery(id+"F0.imprint","IMPRINT",FACE,{"disambiguationData":[TD([[makeQuery(id+"F0.imprint","IMPRINT",EDGE,{"disambiguationData":[TD([[subQ2,-1.0]])],"derivedFrom":subQ1}),1.0]])]});}
            var Q294;
            {var subQ0=sQuery(id+"F0.wireOp",EDGE,"E2.10.5.0");var subQ1=sQuery(id+"F0.wireOp",EDGE,"E2.10.4.0");var subQ2=makeQuery(id+"F0.imprint","INTERSECT",VERTEX,{"disambiguationData":[OD(0.0)],"derivedFrom":[subQ1,subQ0]});Q294=makeQuery(id+"F0.imprint","IMPRINT",FACE,{"disambiguationData":[TD([[makeQuery(id+"F0.imprint","IMPRINT",EDGE,{"disambiguationData":[TD([[subQ2,-1.0]])],"derivedFrom":subQ1}),-1.0]])]});}
            var Q295;
            {var subQ0=sQuery(id+"F0.wireOp",EDGE,"E2.11.4.0");var subQ1=sQuery(id+"F0.wireOp",EDGE,"E2.11.3.0");var subQ2=makeQuery(id+"F0.imprint","INTERSECT",VERTEX,{"disambiguationData":[OD(0.0)],"derivedFrom":[subQ1,subQ0]});Q295=makeQuery(id+"F0.imprint","IMPRINT",FACE,{"disambiguationData":[TD([[makeQuery(id+"F0.imprint","IMPRINT",EDGE,{"disambiguationData":[TD([[subQ2,-1.0]])],"derivedFrom":subQ1}),1.0]])]});}
            var Q296;
            {var subQ0=sQuery(id+"F0.wireOp",EDGE,"E2.9.3.0");var subQ1=sQuery(id+"F0.wireOp",EDGE,"E2.9.2.0");var subQ2=makeQuery(id+"F0.imprint","INTERSECT",VERTEX,{"disambiguationData":[OD(0.0)],"derivedFrom":[subQ1,subQ0]});Q296=makeQuery(id+"F0.imprint","IMPRINT",FACE,{"disambiguationData":[TD([[makeQuery(id+"F0.imprint","IMPRINT",EDGE,{"disambiguationData":[TD([[subQ2,-1.0]])],"derivedFrom":subQ1}),-1.0]])]});}
            var Q297;
            {var subQ0=sQuery(id+"F0.wireOp",EDGE,"E2.10.3.0");var subQ1=sQuery(id+"F0.wireOp",EDGE,"E2.10.2.0");var subQ2=makeQuery(id+"F0.imprint","INTERSECT",VERTEX,{"disambiguationData":[OD(0.0)],"derivedFrom":[subQ1,subQ0]});Q297=makeQuery(id+"F0.imprint","IMPRINT",FACE,{"disambiguationData":[TD([[makeQuery(id+"F0.imprint","IMPRINT",EDGE,{"disambiguationData":[TD([[subQ2,-1.0]])],"derivedFrom":subQ1}),-1.0]])]});}
            var Q298;
            {var subQ0=sQuery(id+"F0.wireOp",EDGE,"E2.2.6.0");var subQ1=sQuery(id+"F0.wireOp",EDGE,"E2.2.5.0");var subQ2=makeQuery(id+"F0.imprint","INTERSECT",VERTEX,{"disambiguationData":[OD(0.0)],"derivedFrom":[subQ1,subQ0]});Q298=makeQuery(id+"F0.imprint","IMPRINT",FACE,{"disambiguationData":[TD([[makeQuery(id+"F0.imprint","IMPRINT",EDGE,{"disambiguationData":[TD([[subQ2,-1.0]])],"derivedFrom":subQ1}),1.0]])]});}
            var Q299;
            {var subQ0=sQuery(id+"F0.wireOp",EDGE,"E2.7.5.0");var subQ1=sQuery(id+"F0.wireOp",EDGE,"E2.7.4.0");var subQ2=makeQuery(id+"F0.imprint","INTERSECT",VERTEX,{"disambiguationData":[OD(0.0)],"derivedFrom":[subQ1,subQ0]});Q299=makeQuery(id+"F0.imprint","IMPRINT",FACE,{"disambiguationData":[TD([[makeQuery(id+"F0.imprint","IMPRINT",EDGE,{"disambiguationData":[TD([[subQ2,-1.0]])],"derivedFrom":subQ1}),-1.0]])]});}
            var Q300;
            {var subQ0=sQuery(id+"F0.wireOp",EDGE,"E2.6.3.0");var subQ1=sQuery(id+"F0.wireOp",EDGE,"E2.6.2.0");var subQ2=makeQuery(id+"F0.imprint","INTERSECT",VERTEX,{"disambiguationData":[OD(0.0)],"derivedFrom":[subQ1,subQ0]});Q300=makeQuery(id+"F0.imprint","IMPRINT",FACE,{"disambiguationData":[TD([[makeQuery(id+"F0.imprint","IMPRINT",EDGE,{"disambiguationData":[TD([[subQ2,-1.0]])],"derivedFrom":subQ1}),-1.0]])]});}
            var Q301;
            {var subQ0=sQuery(id+"F0.wireOp",EDGE,"E2.6.5.0");var subQ1=sQuery(id+"F0.wireOp",EDGE,"E2.6.4.0");var subQ2=makeQuery(id+"F0.imprint","INTERSECT",VERTEX,{"disambiguationData":[OD(0.0)],"derivedFrom":[subQ1,subQ0]});Q301=makeQuery(id+"F0.imprint","IMPRINT",FACE,{"disambiguationData":[TD([[makeQuery(id+"F0.imprint","IMPRINT",EDGE,{"disambiguationData":[TD([[subQ2,-1.0]])],"derivedFrom":subQ1}),-1.0]])]});}
            var Q302;
            {var subQ0=sQuery(id+"F0.wireOp",EDGE,"E2.5.3.0");var subQ1=sQuery(id+"F0.wireOp",EDGE,"E2.5.2.0");var subQ2=makeQuery(id+"F0.imprint","INTERSECT",VERTEX,{"disambiguationData":[OD(0.0)],"derivedFrom":[subQ1,subQ0]});Q302=makeQuery(id+"F0.imprint","IMPRINT",FACE,{"disambiguationData":[TD([[makeQuery(id+"F0.imprint","IMPRINT",EDGE,{"disambiguationData":[TD([[subQ2,-1.0]])],"derivedFrom":subQ1}),-1.0]])]});}
            var Q303;
            {var subQ0=sQuery(id+"F0.wireOp",EDGE,"E2.5.5.0");var subQ1=sQuery(id+"F0.wireOp",EDGE,"E2.5.4.0");var subQ2=makeQuery(id+"F0.imprint","INTERSECT",VERTEX,{"disambiguationData":[OD(0.0)],"derivedFrom":[subQ1,subQ0]});Q303=makeQuery(id+"F0.imprint","IMPRINT",FACE,{"disambiguationData":[TD([[makeQuery(id+"F0.imprint","IMPRINT",EDGE,{"disambiguationData":[TD([[subQ2,-1.0]])],"derivedFrom":subQ1}),-1.0]])]});}
            var Q304;
            {var subQ0=sQuery(id+"F0.wireOp",EDGE,"E2.3.3.0");var subQ1=sQuery(id+"F0.wireOp",EDGE,"E2.3.2.0");var subQ2=makeQuery(id+"F0.imprint","INTERSECT",VERTEX,{"disambiguationData":[OD(0.0)],"derivedFrom":[subQ1,subQ0]});Q304=makeQuery(id+"F0.imprint","IMPRINT",FACE,{"disambiguationData":[TD([[makeQuery(id+"F0.imprint","IMPRINT",EDGE,{"disambiguationData":[TD([[subQ2,-1.0]])],"derivedFrom":subQ1}),-1.0]])]});}
            var Q305;
            {var subQ0=sQuery(id+"F0.wireOp",EDGE,"E2.3.5.0");var subQ1=sQuery(id+"F0.wireOp",EDGE,"E2.3.4.0");var subQ2=makeQuery(id+"F0.imprint","INTERSECT",VERTEX,{"disambiguationData":[OD(0.0)],"derivedFrom":[subQ1,subQ0]});Q305=makeQuery(id+"F0.imprint","IMPRINT",FACE,{"disambiguationData":[TD([[makeQuery(id+"F0.imprint","IMPRINT",EDGE,{"disambiguationData":[TD([[subQ2,-1.0]])],"derivedFrom":subQ1}),-1.0]])]});}
            var Q306;
            {var subQ0=sQuery(id+"F0.wireOp",EDGE,"E2.2.5.0");var subQ1=sQuery(id+"F0.wireOp",EDGE,"E2.2.4.0");var subQ2=makeQuery(id+"F0.imprint","INTERSECT",VERTEX,{"disambiguationData":[OD(0.0)],"derivedFrom":[subQ1,subQ0]});Q306=makeQuery(id+"F0.imprint","IMPRINT",FACE,{"disambiguationData":[TD([[makeQuery(id+"F0.imprint","IMPRINT",EDGE,{"disambiguationData":[TD([[subQ2,-1.0]])],"derivedFrom":subQ1}),-1.0]])]});}
            var Q307;
            {var subQ0=sQuery(id+"F0.wireOp",EDGE,"E2.1.3.0");var subQ1=sQuery(id+"F0.wireOp",EDGE,"E2.1.2.0");var subQ2=makeQuery(id+"F0.imprint","INTERSECT",VERTEX,{"disambiguationData":[OD(0.0)],"derivedFrom":[subQ1,subQ0]});Q307=makeQuery(id+"F0.imprint","IMPRINT",FACE,{"disambiguationData":[TD([[makeQuery(id+"F0.imprint","IMPRINT",EDGE,{"disambiguationData":[TD([[subQ2,-1.0]])],"derivedFrom":subQ1}),-1.0]])]});}
            var Q308;
            {var subQ0=sQuery(id+"F0.wireOp",EDGE,"E2.1.5.0");var subQ1=sQuery(id+"F0.wireOp",EDGE,"E2.1.4.0");var subQ2=makeQuery(id+"F0.imprint","INTERSECT",VERTEX,{"disambiguationData":[OD(0.0)],"derivedFrom":[subQ1,subQ0]});Q308=makeQuery(id+"F0.imprint","IMPRINT",FACE,{"disambiguationData":[TD([[makeQuery(id+"F0.imprint","IMPRINT",EDGE,{"disambiguationData":[TD([[subQ2,-1.0]])],"derivedFrom":subQ1}),-1.0]])]});}
            var Q309;
            {var subQ0=sQuery(id+"F0.wireOp",EDGE,"E2.1.2.0");var subQ1=sQuery(id+"F0.wireOp",EDGE,"E2.0.2.0");var subQ2=makeQuery(id+"F0.imprint","INTERSECT",VERTEX,{"disambiguationData":[OD(0.0)],"derivedFrom":[subQ1,subQ0]});Q309=makeQuery(id+"F0.imprint","IMPRINT",FACE,{"disambiguationData":[TD([[makeQuery(id+"F0.imprint","IMPRINT",EDGE,{"disambiguationData":[TD([[subQ2,1.0]])],"derivedFrom":subQ1}),-1.0]])]});}
            var Q310;
            {var subQ0=sQuery(id+"F0.wireOp",EDGE,"E2.2.0.0");var subQ1=sQuery(id+"F0.wireOp",EDGE,"E2.1.0.0");var subQ2=makeQuery(id+"F0.imprint","INTERSECT",VERTEX,{"disambiguationData":[OD(0.0)],"derivedFrom":[subQ1,subQ0]});Q310=makeQuery(id+"F0.imprint","IMPRINT",FACE,{"disambiguationData":[TD([[makeQuery(id+"F0.imprint","IMPRINT",EDGE,{"disambiguationData":[TD([[subQ2,-1.0]])],"derivedFrom":subQ1}),-1.0]])]});}
            var Q311;
            {var subQ0=sQuery(id+"F0.wireOp",EDGE,"E2.9.3.0");var subQ1=sQuery(id+"F0.wireOp",EDGE,"E2.9.2.0");var subQ2=makeQuery(id+"F0.imprint","INTERSECT",VERTEX,{"disambiguationData":[OD(0.0)],"derivedFrom":[subQ1,subQ0]});Q311=makeQuery(id+"F0.imprint","IMPRINT",FACE,{"disambiguationData":[TD([[makeQuery(id+"F0.imprint","IMPRINT",EDGE,{"disambiguationData":[TD([[subQ2,-1.0]])],"derivedFrom":subQ1}),1.0]])]});}
            var Q312;
            {var subQ0=sQuery(id+"F0.wireOp",EDGE,"E2.9.5.0");var subQ1=sQuery(id+"F0.wireOp",EDGE,"E2.9.4.0");var subQ2=makeQuery(id+"F0.imprint","INTERSECT",VERTEX,{"disambiguationData":[OD(0.0)],"derivedFrom":[subQ1,subQ0]});Q312=makeQuery(id+"F0.imprint","IMPRINT",FACE,{"disambiguationData":[TD([[makeQuery(id+"F0.imprint","IMPRINT",EDGE,{"disambiguationData":[TD([[subQ2,-1.0]])],"derivedFrom":subQ1}),1.0]])]});}
            var Q313;
            {var subQ0=sQuery(id+"F0.wireOp",EDGE,"E2.11.0.0");var subQ1=sQuery(id+"F0.wireOp",EDGE,"E2.10.0.0");var subQ2=makeQuery(id+"F0.imprint","INTERSECT",VERTEX,{"disambiguationData":[OD(1.0)],"derivedFrom":[subQ1,subQ0]});Q313=makeQuery(id+"F0.imprint","IMPRINT",FACE,{"disambiguationData":[TD([[makeQuery(id+"F0.imprint","IMPRINT",EDGE,{"disambiguationData":[TD([[subQ2,-1.0]])],"derivedFrom":subQ1}),1.0]])]});}
            var Q314;
            {var subQ0=sQuery(id+"F0.wireOp",EDGE,"E2.10.3.0");var subQ1=sQuery(id+"F0.wireOp",EDGE,"E2.10.2.0");var subQ2=makeQuery(id+"F0.imprint","INTERSECT",VERTEX,{"disambiguationData":[OD(0.0)],"derivedFrom":[subQ1,subQ0]});Q314=makeQuery(id+"F0.imprint","IMPRINT",FACE,{"disambiguationData":[TD([[makeQuery(id+"F0.imprint","IMPRINT",EDGE,{"disambiguationData":[TD([[subQ2,-1.0]])],"derivedFrom":subQ1}),1.0]])]});}
            var Q315;
            {var subQ0=sQuery(id+"F0.wireOp",EDGE,"E2.9.0.0");var subQ1=sQuery(id+"F0.wireOp",EDGE,"E2.8.0.0");var subQ2=makeQuery(id+"F0.imprint","INTERSECT",VERTEX,{"disambiguationData":[OD(1.0)],"derivedFrom":[subQ1,subQ0]});Q315=makeQuery(id+"F0.imprint","IMPRINT",FACE,{"disambiguationData":[TD([[makeQuery(id+"F0.imprint","IMPRINT",EDGE,{"disambiguationData":[TD([[subQ2,-1.0]])],"derivedFrom":subQ1}),1.0]])]});}
            var Q316;
            {var subQ0=sQuery(id+"F0.wireOp",EDGE,"E2.8.3.0");var subQ1=sQuery(id+"F0.wireOp",EDGE,"E2.8.2.0");var subQ2=makeQuery(id+"F0.imprint","INTERSECT",VERTEX,{"disambiguationData":[OD(0.0)],"derivedFrom":[subQ1,subQ0]});Q316=makeQuery(id+"F0.imprint","IMPRINT",FACE,{"disambiguationData":[TD([[makeQuery(id+"F0.imprint","IMPRINT",EDGE,{"disambiguationData":[TD([[subQ2,-1.0]])],"derivedFrom":subQ1}),1.0]])]});}
            var Q317;
            {var subQ0=sQuery(id+"F0.wireOp",EDGE,"E2.8.5.0");var subQ1=sQuery(id+"F0.wireOp",EDGE,"E2.8.4.0");var subQ2=makeQuery(id+"F0.imprint","INTERSECT",VERTEX,{"disambiguationData":[OD(0.0)],"derivedFrom":[subQ1,subQ0]});Q317=makeQuery(id+"F0.imprint","IMPRINT",FACE,{"disambiguationData":[TD([[makeQuery(id+"F0.imprint","IMPRINT",EDGE,{"disambiguationData":[TD([[subQ2,-1.0]])],"derivedFrom":subQ1}),1.0]])]});}
            var Q318;
            {var subQ0=sQuery(id+"F0.wireOp",EDGE,"E2.10.0.0");var subQ1=sQuery(id+"F0.wireOp",EDGE,"E2.9.0.0");var subQ2=makeQuery(id+"F0.imprint","INTERSECT",VERTEX,{"disambiguationData":[OD(1.0)],"derivedFrom":[subQ1,subQ0]});Q318=makeQuery(id+"F0.imprint","IMPRINT",FACE,{"disambiguationData":[TD([[makeQuery(id+"F0.imprint","IMPRINT",EDGE,{"disambiguationData":[TD([[subQ2,-1.0]])],"derivedFrom":subQ1}),1.0]])]});}
            var Q319;
            {var subQ0=sQuery(id+"F0.wireOp",EDGE,"E2.7.3.0");var subQ1=sQuery(id+"F0.wireOp",EDGE,"E2.7.2.0");var subQ2=makeQuery(id+"F0.imprint","INTERSECT",VERTEX,{"disambiguationData":[OD(0.0)],"derivedFrom":[subQ1,subQ0]});Q319=makeQuery(id+"F0.imprint","IMPRINT",FACE,{"disambiguationData":[TD([[makeQuery(id+"F0.imprint","IMPRINT",EDGE,{"disambiguationData":[TD([[subQ2,-1.0]])],"derivedFrom":subQ1}),1.0]])]});}
            var Q320;
            {var subQ0=sQuery(id+"F0.wireOp",EDGE,"E2.7.5.0");var subQ1=sQuery(id+"F0.wireOp",EDGE,"E2.7.4.0");var subQ2=makeQuery(id+"F0.imprint","INTERSECT",VERTEX,{"disambiguationData":[OD(0.0)],"derivedFrom":[subQ1,subQ0]});Q320=makeQuery(id+"F0.imprint","IMPRINT",FACE,{"disambiguationData":[TD([[makeQuery(id+"F0.imprint","IMPRINT",EDGE,{"disambiguationData":[TD([[subQ2,-1.0]])],"derivedFrom":subQ1}),1.0]])]});}
            var Q321;
            {var subQ0=sQuery(id+"F0.wireOp",EDGE,"E2.6.3.0");var subQ1=sQuery(id+"F0.wireOp",EDGE,"E2.6.2.0");var subQ2=makeQuery(id+"F0.imprint","INTERSECT",VERTEX,{"disambiguationData":[OD(0.0)],"derivedFrom":[subQ1,subQ0]});Q321=makeQuery(id+"F0.imprint","IMPRINT",FACE,{"disambiguationData":[TD([[makeQuery(id+"F0.imprint","IMPRINT",EDGE,{"disambiguationData":[TD([[subQ2,-1.0]])],"derivedFrom":subQ1}),1.0]])]});}
            var Q322;
            {var subQ0=sQuery(id+"F0.wireOp",EDGE,"E2.6.5.0");var subQ1=sQuery(id+"F0.wireOp",EDGE,"E2.6.4.0");var subQ2=makeQuery(id+"F0.imprint","INTERSECT",VERTEX,{"disambiguationData":[OD(0.0)],"derivedFrom":[subQ1,subQ0]});Q322=makeQuery(id+"F0.imprint","IMPRINT",FACE,{"disambiguationData":[TD([[makeQuery(id+"F0.imprint","IMPRINT",EDGE,{"disambiguationData":[TD([[subQ2,-1.0]])],"derivedFrom":subQ1}),1.0]])]});}
            var Q323;
            {var subQ0=sQuery(id+"F0.wireOp",EDGE,"E2.8.0.0");var subQ1=sQuery(id+"F0.wireOp",EDGE,"E2.7.0.0");var subQ2=makeQuery(id+"F0.imprint","INTERSECT",VERTEX,{"disambiguationData":[OD(1.0)],"derivedFrom":[subQ1,subQ0]});Q323=makeQuery(id+"F0.imprint","IMPRINT",FACE,{"disambiguationData":[TD([[makeQuery(id+"F0.imprint","IMPRINT",EDGE,{"disambiguationData":[TD([[subQ2,-1.0]])],"derivedFrom":subQ1}),1.0]])]});}
            var Q324;
            {var subQ0=sQuery(id+"F0.wireOp",EDGE,"E2.4.5.0");var subQ1=sQuery(id+"F0.wireOp",EDGE,"E2.4.4.0");var subQ2=makeQuery(id+"F0.imprint","INTERSECT",VERTEX,{"disambiguationData":[OD(0.0)],"derivedFrom":[subQ1,subQ0]});Q324=makeQuery(id+"F0.imprint","IMPRINT",FACE,{"disambiguationData":[TD([[makeQuery(id+"F0.imprint","IMPRINT",EDGE,{"disambiguationData":[TD([[subQ2,-1.0]])],"derivedFrom":subQ1}),1.0]])]});}
            var Q325;
            {var subQ0=sQuery(id+"F0.wireOp",EDGE,"E2.6.0.0");var subQ1=sQuery(id+"F0.wireOp",EDGE,"E2.5.0.0");var subQ2=makeQuery(id+"F0.imprint","INTERSECT",VERTEX,{"disambiguationData":[OD(1.0)],"derivedFrom":[subQ1,subQ0]});Q325=makeQuery(id+"F0.imprint","IMPRINT",FACE,{"disambiguationData":[TD([[makeQuery(id+"F0.imprint","IMPRINT",EDGE,{"disambiguationData":[TD([[subQ2,-1.0]])],"derivedFrom":subQ1}),1.0]])]});}
            var Q326;
            {var subQ0=sQuery(id+"F0.wireOp",EDGE,"E2.5.3.0");var subQ1=sQuery(id+"F0.wireOp",EDGE,"E2.5.2.0");var subQ2=makeQuery(id+"F0.imprint","INTERSECT",VERTEX,{"disambiguationData":[OD(0.0)],"derivedFrom":[subQ1,subQ0]});Q326=makeQuery(id+"F0.imprint","IMPRINT",FACE,{"disambiguationData":[TD([[makeQuery(id+"F0.imprint","IMPRINT",EDGE,{"disambiguationData":[TD([[subQ2,-1.0]])],"derivedFrom":subQ1}),1.0]])]});}
            var Q327;
            {var subQ0=sQuery(id+"F0.wireOp",EDGE,"E2.5.5.0");var subQ1=sQuery(id+"F0.wireOp",EDGE,"E2.5.4.0");var subQ2=makeQuery(id+"F0.imprint","INTERSECT",VERTEX,{"disambiguationData":[OD(0.0)],"derivedFrom":[subQ1,subQ0]});Q327=makeQuery(id+"F0.imprint","IMPRINT",FACE,{"disambiguationData":[TD([[makeQuery(id+"F0.imprint","IMPRINT",EDGE,{"disambiguationData":[TD([[subQ2,-1.0]])],"derivedFrom":subQ1}),1.0]])]});}
            var Q328;
            {var subQ0=sQuery(id+"F0.wireOp",EDGE,"E2.3.3.0");var subQ1=sQuery(id+"F0.wireOp",EDGE,"E2.3.2.0");var subQ2=makeQuery(id+"F0.imprint","INTERSECT",VERTEX,{"disambiguationData":[OD(0.0)],"derivedFrom":[subQ1,subQ0]});Q328=makeQuery(id+"F0.imprint","IMPRINT",FACE,{"disambiguationData":[TD([[makeQuery(id+"F0.imprint","IMPRINT",EDGE,{"disambiguationData":[TD([[subQ2,-1.0]])],"derivedFrom":subQ1}),1.0]])]});}
            var Q329;
            {var subQ0=sQuery(id+"F0.wireOp",EDGE,"E2.3.5.0");var subQ1=sQuery(id+"F0.wireOp",EDGE,"E2.3.4.0");var subQ2=makeQuery(id+"F0.imprint","INTERSECT",VERTEX,{"disambiguationData":[OD(0.0)],"derivedFrom":[subQ1,subQ0]});Q329=makeQuery(id+"F0.imprint","IMPRINT",FACE,{"disambiguationData":[TD([[makeQuery(id+"F0.imprint","IMPRINT",EDGE,{"disambiguationData":[TD([[subQ2,-1.0]])],"derivedFrom":subQ1}),1.0]])]});}
            var Q330;
            {var subQ0=sQuery(id+"F0.wireOp",EDGE,"E2.5.0.0");var subQ1=sQuery(id+"F0.wireOp",EDGE,"E2.4.0.0");var subQ2=makeQuery(id+"F0.imprint","INTERSECT",VERTEX,{"disambiguationData":[OD(1.0)],"derivedFrom":[subQ1,subQ0]});Q330=makeQuery(id+"F0.imprint","IMPRINT",FACE,{"disambiguationData":[TD([[makeQuery(id+"F0.imprint","IMPRINT",EDGE,{"disambiguationData":[TD([[subQ2,-1.0]])],"derivedFrom":subQ1}),1.0]])]});}
            var Q331;
            {var subQ0=sQuery(id+"F0.wireOp",EDGE,"E2.4.3.0");var subQ1=sQuery(id+"F0.wireOp",EDGE,"E2.4.2.0");var subQ2=makeQuery(id+"F0.imprint","INTERSECT",VERTEX,{"disambiguationData":[OD(0.0)],"derivedFrom":[subQ1,subQ0]});Q331=makeQuery(id+"F0.imprint","IMPRINT",FACE,{"disambiguationData":[TD([[makeQuery(id+"F0.imprint","IMPRINT",EDGE,{"disambiguationData":[TD([[subQ2,-1.0]])],"derivedFrom":subQ1}),1.0]])]});}
            var Q332;
            {var subQ0=sQuery(id+"F0.wireOp",EDGE,"E2.2.3.0");var subQ1=sQuery(id+"F0.wireOp",EDGE,"E2.2.2.0");var subQ2=makeQuery(id+"F0.imprint","INTERSECT",VERTEX,{"disambiguationData":[OD(0.0)],"derivedFrom":[subQ1,subQ0]});Q332=makeQuery(id+"F0.imprint","IMPRINT",FACE,{"disambiguationData":[TD([[makeQuery(id+"F0.imprint","IMPRINT",EDGE,{"disambiguationData":[TD([[subQ2,-1.0]])],"derivedFrom":subQ1}),1.0]])]});}
            var Q333;
            {var subQ0=sQuery(id+"F0.wireOp",EDGE,"E2.4.0.0");var subQ1=sQuery(id+"F0.wireOp",EDGE,"E2.3.0.0");var subQ2=makeQuery(id+"F0.imprint","INTERSECT",VERTEX,{"disambiguationData":[OD(1.0)],"derivedFrom":[subQ1,subQ0]});Q333=makeQuery(id+"F0.imprint","IMPRINT",FACE,{"disambiguationData":[TD([[makeQuery(id+"F0.imprint","IMPRINT",EDGE,{"disambiguationData":[TD([[subQ2,-1.0]])],"derivedFrom":subQ1}),1.0]])]});}
            var Q334;
            {var subQ0=sQuery(id+"F0.wireOp",EDGE,"E2.10.5.0");var subQ1=sQuery(id+"F0.wireOp",EDGE,"E2.10.4.0");var subQ2=makeQuery(id+"F0.imprint","INTERSECT",VERTEX,{"disambiguationData":[OD(0.0)],"derivedFrom":[subQ1,subQ0]});Q334=makeQuery(id+"F0.imprint","IMPRINT",FACE,{"disambiguationData":[TD([[makeQuery(id+"F0.imprint","IMPRINT",EDGE,{"disambiguationData":[TD([[subQ2,-1.0]])],"derivedFrom":subQ1}),1.0]])]});}
            var Q335;
            {var subQ0=sQuery(id+"F0.wireOp",EDGE,"E2.11.3.0");var subQ1=sQuery(id+"F0.wireOp",EDGE,"E2.11.2.0");var subQ2=makeQuery(id+"F0.imprint","INTERSECT",VERTEX,{"disambiguationData":[OD(0.0)],"derivedFrom":[subQ1,subQ0]});Q335=makeQuery(id+"F0.imprint","IMPRINT",FACE,{"disambiguationData":[TD([[makeQuery(id+"F0.imprint","IMPRINT",EDGE,{"disambiguationData":[TD([[subQ2,-1.0]])],"derivedFrom":subQ1}),1.0]])]});}
            var Q336;
            {var subQ0=sQuery(id+"F0.wireOp",EDGE,"E2.1.4.0");var subQ1=sQuery(id+"F0.wireOp",EDGE,"E2.0.4.0");var subQ2=makeQuery(id+"F0.imprint","INTERSECT",VERTEX,{"disambiguationData":[OD(0.0)],"derivedFrom":[subQ1,subQ0]});Q336=makeQuery(id+"F0.imprint","IMPRINT",FACE,{"disambiguationData":[TD([[makeQuery(id+"F0.imprint","IMPRINT",EDGE,{"disambiguationData":[TD([[subQ2,-1.0]])],"derivedFrom":subQ1}),1.0]])]});}
            var Q337;
            {var subQ0=sQuery(id+"F0.wireOp",EDGE,"E2.2.0.0");var subQ1=sQuery(id+"F0.wireOp",EDGE,"E2.1.0.0");var subQ2=makeQuery(id+"F0.imprint","INTERSECT",VERTEX,{"disambiguationData":[OD(1.0)],"derivedFrom":[subQ1,subQ0]});Q337=makeQuery(id+"F0.imprint","IMPRINT",FACE,{"disambiguationData":[TD([[makeQuery(id+"F0.imprint","IMPRINT",EDGE,{"disambiguationData":[TD([[subQ2,-1.0]])],"derivedFrom":subQ1}),1.0]])]});}
            var Q338;
            {var subQ0=sQuery(id+"F0.wireOp",EDGE,"E2.1.3.0");var subQ1=sQuery(id+"F0.wireOp",EDGE,"E2.1.2.0");var subQ2=makeQuery(id+"F0.imprint","INTERSECT",VERTEX,{"disambiguationData":[OD(0.0)],"derivedFrom":[subQ1,subQ0]});Q338=makeQuery(id+"F0.imprint","IMPRINT",FACE,{"disambiguationData":[TD([[makeQuery(id+"F0.imprint","IMPRINT",EDGE,{"disambiguationData":[TD([[subQ2,-1.0]])],"derivedFrom":subQ1}),1.0]])]});}
            var Q339;
            {var subQ0=sQuery(id+"F0.wireOp",EDGE,"E2.1.5.0");var subQ1=sQuery(id+"F0.wireOp",EDGE,"E2.1.4.0");var subQ2=makeQuery(id+"F0.imprint","INTERSECT",VERTEX,{"disambiguationData":[OD(0.0)],"derivedFrom":[subQ1,subQ0]});Q339=makeQuery(id+"F0.imprint","IMPRINT",FACE,{"disambiguationData":[TD([[makeQuery(id+"F0.imprint","IMPRINT",EDGE,{"disambiguationData":[TD([[subQ2,-1.0]])],"derivedFrom":subQ1}),1.0]])]});}
            var Q340;
            {var subQ0=sQuery(id+"F0.wireOp",EDGE,"E2.7.0.0");var subQ1=sQuery(id+"F0.wireOp",EDGE,"E2.6.0.0");var subQ2=makeQuery(id+"F0.imprint","INTERSECT",VERTEX,{"disambiguationData":[OD(1.0)],"derivedFrom":[subQ1,subQ0]});Q340=makeQuery(id+"F0.imprint","IMPRINT",FACE,{"disambiguationData":[TD([[makeQuery(id+"F0.imprint","IMPRINT",EDGE,{"disambiguationData":[TD([[subQ2,1.0]])],"derivedFrom":subQ1}),-1.0]])]});}
            var Q341;
            {var subQ0=sQuery(id+"F0.wireOp",EDGE,"E2.8.0.0");var subQ1=sQuery(id+"F0.wireOp",EDGE,"E2.7.0.0");var subQ2=makeQuery(id+"F0.imprint","INTERSECT",VERTEX,{"disambiguationData":[OD(1.0)],"derivedFrom":[subQ1,subQ0]});Q341=makeQuery(id+"F0.imprint","IMPRINT",FACE,{"disambiguationData":[TD([[makeQuery(id+"F0.imprint","IMPRINT",EDGE,{"disambiguationData":[TD([[subQ2,1.0]])],"derivedFrom":subQ1}),-1.0]])]});}
            var Q342;
            {var subQ0=sQuery(id+"F0.wireOp",EDGE,"E2.6.0.0");var subQ1=sQuery(id+"F0.wireOp",EDGE,"E2.5.0.0");var subQ2=makeQuery(id+"F0.imprint","INTERSECT",VERTEX,{"disambiguationData":[OD(1.0)],"derivedFrom":[subQ1,subQ0]});Q342=makeQuery(id+"F0.imprint","IMPRINT",FACE,{"disambiguationData":[TD([[makeQuery(id+"F0.imprint","IMPRINT",EDGE,{"disambiguationData":[TD([[subQ2,1.0]])],"derivedFrom":subQ1}),-1.0]])]});}
            var Q343;
            {var subQ0=sQuery(id+"F0.wireOp",EDGE,"E2.3.0.0");var subQ1=sQuery(id+"F0.wireOp",EDGE,"E2.2.0.0");var subQ2=makeQuery(id+"F0.imprint","INTERSECT",VERTEX,{"disambiguationData":[OD(1.0)],"derivedFrom":[subQ1,subQ0]});Q343=makeQuery(id+"F0.imprint","IMPRINT",FACE,{"disambiguationData":[TD([[makeQuery(id+"F0.imprint","IMPRINT",EDGE,{"disambiguationData":[TD([[subQ2,1.0]])],"derivedFrom":subQ1}),-1.0]])]});}
            var Q344;
            {var subQ0=sQuery(id+"F0.wireOp",EDGE,"E2.4.0.0");var subQ1=sQuery(id+"F0.wireOp",EDGE,"E2.3.0.0");var subQ2=makeQuery(id+"F0.imprint","INTERSECT",VERTEX,{"disambiguationData":[OD(1.0)],"derivedFrom":[subQ1,subQ0]});Q344=makeQuery(id+"F0.imprint","IMPRINT",FACE,{"disambiguationData":[TD([[makeQuery(id+"F0.imprint","IMPRINT",EDGE,{"disambiguationData":[TD([[subQ2,1.0]])],"derivedFrom":subQ1}),-1.0]])]});}
            var Q345;
            {var subQ0=sQuery(id+"F0.wireOp",EDGE,"E2.1.4.0");var subQ1=sQuery(id+"F0.wireOp",EDGE,"E2.0.4.0");var subQ2=makeQuery(id+"F0.imprint","INTERSECT",VERTEX,{"disambiguationData":[OD(0.0)],"derivedFrom":[subQ1,subQ0]});Q345=makeQuery(id+"F0.imprint","IMPRINT",FACE,{"disambiguationData":[TD([[makeQuery(id+"F0.imprint","IMPRINT",EDGE,{"disambiguationData":[TD([[subQ2,1.0]])],"derivedFrom":subQ1}),-1.0]])]});}
            var Q346;
            {var subQ0=sQuery(id+"F0.wireOp",EDGE,"E2.2.0.0");var subQ1=sQuery(id+"F0.wireOp",EDGE,"E2.1.0.0");var subQ2=makeQuery(id+"F0.imprint","INTERSECT",VERTEX,{"disambiguationData":[OD(1.0)],"derivedFrom":[subQ1,subQ0]});Q346=makeQuery(id+"F0.imprint","IMPRINT",FACE,{"disambiguationData":[TD([[makeQuery(id+"F0.imprint","IMPRINT",EDGE,{"disambiguationData":[TD([[subQ2,1.0]])],"derivedFrom":subQ1}),-1.0]])]});}
            var Q347;
            {var subQ0=sQuery(id+"F0.wireOp",EDGE,"E2.11.2.0");var subQ1=sQuery(id+"F0.wireOp",EDGE,"E2.11.1.0");var subQ2=makeQuery(id+"F0.imprint","INTERSECT",VERTEX,{"disambiguationData":[OD(0.0)],"derivedFrom":[subQ1,subQ0]});Q347=makeQuery(id+"F0.imprint","IMPRINT",FACE,{"disambiguationData":[TD([[makeQuery(id+"F0.imprint","IMPRINT",EDGE,{"disambiguationData":[TD([[subQ2,-1.0]])],"derivedFrom":subQ1}),1.0]])]});}
            var Q348;
            {var subQ0=sQuery(id+"F0.wireOp",EDGE,"E2.11.0.0");var subQ1=sQuery(id+"F0.wireOp",EDGE,"E2.10.0.0");var subQ2=makeQuery(id+"F0.imprint","INTERSECT",VERTEX,{"disambiguationData":[OD(1.0)],"derivedFrom":[subQ1,subQ0]});Q348=makeQuery(id+"F0.imprint","IMPRINT",FACE,{"disambiguationData":[TD([[makeQuery(id+"F0.imprint","IMPRINT",EDGE,{"disambiguationData":[TD([[subQ2,1.0]])],"derivedFrom":subQ1}),-1.0]])]});}
            var Q349;
            {var subQ0=sQuery(id+"F0.wireOp",EDGE,"E2.9.6.0");var subQ1=sQuery(id+"F0.wireOp",EDGE,"E2.8.6.0");var subQ2=makeQuery(id+"F0.imprint","INTERSECT",VERTEX,{"disambiguationData":[OD(0.0)],"derivedFrom":[subQ1,subQ0]});Q349=makeQuery(id+"F0.imprint","IMPRINT",FACE,{"disambiguationData":[TD([[makeQuery(id+"F0.imprint","IMPRINT",EDGE,{"disambiguationData":[TD([[subQ2,1.0]])],"derivedFrom":subQ1}),-1.0]])]});}
            var Q350;
            {var subQ0=sQuery(id+"F0.wireOp",EDGE,"E2.1.1.1");var subQ1=sQuery(id+"F0.wireOp",EDGE,"E2.0.1.0");var subQ2=makeQuery(id+"F0.imprint","INTERSECT",VERTEX,{"derivedFrom":[subQ1,subQ0]});Q350=makeQuery(id+"F0.imprint","IMPRINT",FACE,{"disambiguationData":[TD([[makeQuery(id+"F0.imprint","IMPRINT",EDGE,{"disambiguationData":[TD([[subQ2,1.0]])],"derivedFrom":subQ1}),-1.0]])]});}
            var Q351;
            {var subQ0=sQuery(id+"F0.wireOp",EDGE,"E2.11.4.0");var subQ1=sQuery(id+"F0.wireOp",EDGE,"E2.10.4.0");var subQ2=makeQuery(id+"F0.imprint","INTERSECT",VERTEX,{"disambiguationData":[OD(0.0)],"derivedFrom":[subQ1,subQ0]});Q351=makeQuery(id+"F0.imprint","IMPRINT",FACE,{"disambiguationData":[TD([[makeQuery(id+"F0.imprint","IMPRINT",EDGE,{"disambiguationData":[TD([[subQ2,1.0]])],"derivedFrom":subQ1}),-1.0]])]});}
            var Q352;
            {var subQ0=sQuery(id+"F0.wireOp",EDGE,"E2.11.6.1");var subQ1=sQuery(id+"F0.wireOp",EDGE,"E2.10.6.0");var subQ2=makeQuery(id+"F0.imprint","INTERSECT",VERTEX,{"derivedFrom":[subQ1,subQ0]});Q352=makeQuery(id+"F0.imprint","IMPRINT",FACE,{"disambiguationData":[TD([[makeQuery(id+"F0.imprint","IMPRINT",EDGE,{"disambiguationData":[TD([[subQ2,1.0]])],"derivedFrom":subQ1}),-1.0]])]});}
            var Q353;
            {var subQ0=sQuery(id+"F0.wireOp",EDGE,"E2.10.2.0");var subQ1=sQuery(id+"F0.wireOp",EDGE,"E2.9.2.0");var subQ2=makeQuery(id+"F0.imprint","INTERSECT",VERTEX,{"disambiguationData":[OD(0.0)],"derivedFrom":[subQ1,subQ0]});Q353=makeQuery(id+"F0.imprint","IMPRINT",FACE,{"disambiguationData":[TD([[makeQuery(id+"F0.imprint","IMPRINT",EDGE,{"disambiguationData":[TD([[subQ2,1.0]])],"derivedFrom":subQ1}),-1.0]])]});}
            var Q354;
            {var subQ0=sQuery(id+"F0.wireOp",EDGE,"E2.10.4.0");var subQ1=sQuery(id+"F0.wireOp",EDGE,"E2.9.4.0");var subQ2=makeQuery(id+"F0.imprint","INTERSECT",VERTEX,{"disambiguationData":[OD(0.0)],"derivedFrom":[subQ1,subQ0]});Q354=makeQuery(id+"F0.imprint","IMPRINT",FACE,{"disambiguationData":[TD([[makeQuery(id+"F0.imprint","IMPRINT",EDGE,{"disambiguationData":[TD([[subQ2,1.0]])],"derivedFrom":subQ1}),-1.0]])]});}
            var Q355;
            {var subQ0=sQuery(id+"F0.wireOp",EDGE,"E2.10.6.1");var subQ1=sQuery(id+"F0.wireOp",EDGE,"E2.9.6.0");var subQ2=makeQuery(id+"F0.imprint","INTERSECT",VERTEX,{"derivedFrom":[subQ1,subQ0]});Q355=makeQuery(id+"F0.imprint","IMPRINT",FACE,{"disambiguationData":[TD([[makeQuery(id+"F0.imprint","IMPRINT",EDGE,{"disambiguationData":[TD([[subQ2,1.0]])],"derivedFrom":subQ1}),-1.0]])]});}
            var Q356;
            {var subQ0=sQuery(id+"F0.wireOp",EDGE,"E2.11.2.0");var subQ1=sQuery(id+"F0.wireOp",EDGE,"E2.10.2.0");var subQ2=makeQuery(id+"F0.imprint","INTERSECT",VERTEX,{"disambiguationData":[OD(0.0)],"derivedFrom":[subQ1,subQ0]});Q356=makeQuery(id+"F0.imprint","IMPRINT",FACE,{"disambiguationData":[TD([[makeQuery(id+"F0.imprint","IMPRINT",EDGE,{"disambiguationData":[TD([[subQ2,1.0]])],"derivedFrom":subQ1}),-1.0]])]});}
            var Q357;
            {var subQ0=sQuery(id+"F0.wireOp",EDGE,"E2.8.6.1");var subQ1=sQuery(id+"F0.wireOp",EDGE,"E2.7.6.0");var subQ2=makeQuery(id+"F0.imprint","INTERSECT",VERTEX,{"derivedFrom":[subQ1,subQ0]});Q357=makeQuery(id+"F0.imprint","IMPRINT",FACE,{"disambiguationData":[TD([[makeQuery(id+"F0.imprint","IMPRINT",EDGE,{"disambiguationData":[TD([[subQ2,1.0]])],"derivedFrom":subQ1}),-1.0]])]});}
            var Q358;
            {var subQ0=sQuery(id+"F0.wireOp",EDGE,"E2.9.2.0");var subQ1=sQuery(id+"F0.wireOp",EDGE,"E2.8.2.0");var subQ2=makeQuery(id+"F0.imprint","INTERSECT",VERTEX,{"disambiguationData":[OD(0.0)],"derivedFrom":[subQ1,subQ0]});Q358=makeQuery(id+"F0.imprint","IMPRINT",FACE,{"disambiguationData":[TD([[makeQuery(id+"F0.imprint","IMPRINT",EDGE,{"disambiguationData":[TD([[subQ2,1.0]])],"derivedFrom":subQ1}),-1.0]])]});}
            var Q359;
            {var subQ0=sQuery(id+"F0.wireOp",EDGE,"E2.9.4.0");var subQ1=sQuery(id+"F0.wireOp",EDGE,"E2.8.4.0");var subQ2=makeQuery(id+"F0.imprint","INTERSECT",VERTEX,{"disambiguationData":[OD(0.0)],"derivedFrom":[subQ1,subQ0]});Q359=makeQuery(id+"F0.imprint","IMPRINT",FACE,{"disambiguationData":[TD([[makeQuery(id+"F0.imprint","IMPRINT",EDGE,{"disambiguationData":[TD([[subQ2,1.0]])],"derivedFrom":subQ1}),-1.0]])]});}
            var Q360;
            {var subQ0=sQuery(id+"F0.wireOp",EDGE,"E2.9.6.1");var subQ1=sQuery(id+"F0.wireOp",EDGE,"E2.8.6.0");var subQ2=makeQuery(id+"F0.imprint","INTERSECT",VERTEX,{"derivedFrom":[subQ1,subQ0]});Q360=makeQuery(id+"F0.imprint","IMPRINT",FACE,{"disambiguationData":[TD([[makeQuery(id+"F0.imprint","IMPRINT",EDGE,{"disambiguationData":[TD([[subQ2,1.0]])],"derivedFrom":subQ1}),-1.0]])]});}
            var Q361;
            {var subQ0=sQuery(id+"F0.wireOp",EDGE,"E2.8.4.0");var subQ1=sQuery(id+"F0.wireOp",EDGE,"E2.7.4.0");var subQ2=makeQuery(id+"F0.imprint","INTERSECT",VERTEX,{"disambiguationData":[OD(0.0)],"derivedFrom":[subQ1,subQ0]});Q361=makeQuery(id+"F0.imprint","IMPRINT",FACE,{"disambiguationData":[TD([[makeQuery(id+"F0.imprint","IMPRINT",EDGE,{"disambiguationData":[TD([[subQ2,1.0]])],"derivedFrom":subQ1}),-1.0]])]});}
            var Q362;
            {var subQ0=sQuery(id+"F0.wireOp",EDGE,"E2.8.2.0");var subQ1=sQuery(id+"F0.wireOp",EDGE,"E2.7.2.0");var subQ2=makeQuery(id+"F0.imprint","INTERSECT",VERTEX,{"disambiguationData":[OD(0.0)],"derivedFrom":[subQ1,subQ0]});Q362=makeQuery(id+"F0.imprint","IMPRINT",FACE,{"disambiguationData":[TD([[makeQuery(id+"F0.imprint","IMPRINT",EDGE,{"disambiguationData":[TD([[subQ2,1.0]])],"derivedFrom":subQ1}),-1.0]])]});}
            var Q363;
            {var subQ0=sQuery(id+"F0.wireOp",EDGE,"E2.6.6.1");var subQ1=sQuery(id+"F0.wireOp",EDGE,"E2.5.6.0");var subQ2=makeQuery(id+"F0.imprint","INTERSECT",VERTEX,{"derivedFrom":[subQ1,subQ0]});Q363=makeQuery(id+"F0.imprint","IMPRINT",FACE,{"disambiguationData":[TD([[makeQuery(id+"F0.imprint","IMPRINT",EDGE,{"disambiguationData":[TD([[subQ2,1.0]])],"derivedFrom":subQ1}),-1.0]])]});}
            var Q364;
            {var subQ0=sQuery(id+"F0.wireOp",EDGE,"E2.7.2.0");var subQ1=sQuery(id+"F0.wireOp",EDGE,"E2.6.2.0");var subQ2=makeQuery(id+"F0.imprint","INTERSECT",VERTEX,{"disambiguationData":[OD(0.0)],"derivedFrom":[subQ1,subQ0]});Q364=makeQuery(id+"F0.imprint","IMPRINT",FACE,{"disambiguationData":[TD([[makeQuery(id+"F0.imprint","IMPRINT",EDGE,{"disambiguationData":[TD([[subQ2,1.0]])],"derivedFrom":subQ1}),-1.0]])]});}
            var Q365;
            {var subQ0=sQuery(id+"F0.wireOp",EDGE,"E2.7.6.1");var subQ1=sQuery(id+"F0.wireOp",EDGE,"E2.6.6.0");var subQ2=makeQuery(id+"F0.imprint","INTERSECT",VERTEX,{"derivedFrom":[subQ1,subQ0]});Q365=makeQuery(id+"F0.imprint","IMPRINT",FACE,{"disambiguationData":[TD([[makeQuery(id+"F0.imprint","IMPRINT",EDGE,{"disambiguationData":[TD([[subQ2,1.0]])],"derivedFrom":subQ1}),-1.0]])]});}
            var Q366;
            {var subQ0=sQuery(id+"F0.wireOp",EDGE,"E2.5.4.0");var subQ1=sQuery(id+"F0.wireOp",EDGE,"E2.4.4.0");var subQ2=makeQuery(id+"F0.imprint","INTERSECT",VERTEX,{"disambiguationData":[OD(0.0)],"derivedFrom":[subQ1,subQ0]});Q366=makeQuery(id+"F0.imprint","IMPRINT",FACE,{"disambiguationData":[TD([[makeQuery(id+"F0.imprint","IMPRINT",EDGE,{"disambiguationData":[TD([[subQ2,1.0]])],"derivedFrom":subQ1}),-1.0]])]});}
            var Q367;
            {var subQ0=sQuery(id+"F0.wireOp",EDGE,"E2.5.6.1");var subQ1=sQuery(id+"F0.wireOp",EDGE,"E2.4.6.0");var subQ2=makeQuery(id+"F0.imprint","INTERSECT",VERTEX,{"derivedFrom":[subQ1,subQ0]});Q367=makeQuery(id+"F0.imprint","IMPRINT",FACE,{"disambiguationData":[TD([[makeQuery(id+"F0.imprint","IMPRINT",EDGE,{"disambiguationData":[TD([[subQ2,1.0]])],"derivedFrom":subQ1}),-1.0]])]});}
            var Q368;
            {var subQ0=sQuery(id+"F0.wireOp",EDGE,"E2.6.2.0");var subQ1=sQuery(id+"F0.wireOp",EDGE,"E2.5.2.0");var subQ2=makeQuery(id+"F0.imprint","INTERSECT",VERTEX,{"disambiguationData":[OD(0.0)],"derivedFrom":[subQ1,subQ0]});Q368=makeQuery(id+"F0.imprint","IMPRINT",FACE,{"disambiguationData":[TD([[makeQuery(id+"F0.imprint","IMPRINT",EDGE,{"disambiguationData":[TD([[subQ2,1.0]])],"derivedFrom":subQ1}),-1.0]])]});}
            var Q369;
            {var subQ0=sQuery(id+"F0.wireOp",EDGE,"E2.6.4.0");var subQ1=sQuery(id+"F0.wireOp",EDGE,"E2.5.4.0");var subQ2=makeQuery(id+"F0.imprint","INTERSECT",VERTEX,{"disambiguationData":[OD(0.0)],"derivedFrom":[subQ1,subQ0]});Q369=makeQuery(id+"F0.imprint","IMPRINT",FACE,{"disambiguationData":[TD([[makeQuery(id+"F0.imprint","IMPRINT",EDGE,{"disambiguationData":[TD([[subQ2,1.0]])],"derivedFrom":subQ1}),-1.0]])]});}
            var Q370;
            {var subQ0=sQuery(id+"F0.wireOp",EDGE,"E2.4.2.0");var subQ1=sQuery(id+"F0.wireOp",EDGE,"E2.3.2.0");var subQ2=makeQuery(id+"F0.imprint","INTERSECT",VERTEX,{"disambiguationData":[OD(0.0)],"derivedFrom":[subQ1,subQ0]});Q370=makeQuery(id+"F0.imprint","IMPRINT",FACE,{"disambiguationData":[TD([[makeQuery(id+"F0.imprint","IMPRINT",EDGE,{"disambiguationData":[TD([[subQ2,1.0]])],"derivedFrom":subQ1}),-1.0]])]});}
            var Q371;
            {var subQ0=sQuery(id+"F0.wireOp",EDGE,"E2.4.4.0");var subQ1=sQuery(id+"F0.wireOp",EDGE,"E2.3.4.0");var subQ2=makeQuery(id+"F0.imprint","INTERSECT",VERTEX,{"disambiguationData":[OD(0.0)],"derivedFrom":[subQ1,subQ0]});Q371=makeQuery(id+"F0.imprint","IMPRINT",FACE,{"disambiguationData":[TD([[makeQuery(id+"F0.imprint","IMPRINT",EDGE,{"disambiguationData":[TD([[subQ2,1.0]])],"derivedFrom":subQ1}),-1.0]])]});}
            var Q372;
            {var subQ0=sQuery(id+"F0.wireOp",EDGE,"E2.4.6.1");var subQ1=sQuery(id+"F0.wireOp",EDGE,"E2.3.6.0");var subQ2=makeQuery(id+"F0.imprint","INTERSECT",VERTEX,{"derivedFrom":[subQ1,subQ0]});Q372=makeQuery(id+"F0.imprint","IMPRINT",FACE,{"disambiguationData":[TD([[makeQuery(id+"F0.imprint","IMPRINT",EDGE,{"disambiguationData":[TD([[subQ2,1.0]])],"derivedFrom":subQ1}),-1.0]])]});}
            var Q373;
            {var subQ0=sQuery(id+"F0.wireOp",EDGE,"E2.5.2.0");var subQ1=sQuery(id+"F0.wireOp",EDGE,"E2.4.2.0");var subQ2=makeQuery(id+"F0.imprint","INTERSECT",VERTEX,{"disambiguationData":[OD(0.0)],"derivedFrom":[subQ1,subQ0]});Q373=makeQuery(id+"F0.imprint","IMPRINT",FACE,{"disambiguationData":[TD([[makeQuery(id+"F0.imprint","IMPRINT",EDGE,{"disambiguationData":[TD([[subQ2,1.0]])],"derivedFrom":subQ1}),-1.0]])]});}
            var Q374;
            {var subQ0=sQuery(id+"F0.wireOp",EDGE,"E2.2.6.1");var subQ1=sQuery(id+"F0.wireOp",EDGE,"E2.1.6.0");var subQ2=makeQuery(id+"F0.imprint","INTERSECT",VERTEX,{"derivedFrom":[subQ1,subQ0]});Q374=makeQuery(id+"F0.imprint","IMPRINT",FACE,{"disambiguationData":[TD([[makeQuery(id+"F0.imprint","IMPRINT",EDGE,{"disambiguationData":[TD([[subQ2,1.0]])],"derivedFrom":subQ1}),-1.0]])]});}
            var Q375;
            {var subQ0=sQuery(id+"F0.wireOp",EDGE,"E2.3.2.0");var subQ1=sQuery(id+"F0.wireOp",EDGE,"E2.2.2.0");var subQ2=makeQuery(id+"F0.imprint","INTERSECT",VERTEX,{"disambiguationData":[OD(0.0)],"derivedFrom":[subQ1,subQ0]});Q375=makeQuery(id+"F0.imprint","IMPRINT",FACE,{"disambiguationData":[TD([[makeQuery(id+"F0.imprint","IMPRINT",EDGE,{"disambiguationData":[TD([[subQ2,1.0]])],"derivedFrom":subQ1}),-1.0]])]});}
            var Q376;
            {var subQ0=sQuery(id+"F0.wireOp",EDGE,"E2.3.4.0");var subQ1=sQuery(id+"F0.wireOp",EDGE,"E2.2.4.0");var subQ2=makeQuery(id+"F0.imprint","INTERSECT",VERTEX,{"disambiguationData":[OD(0.0)],"derivedFrom":[subQ1,subQ0]});Q376=makeQuery(id+"F0.imprint","IMPRINT",FACE,{"disambiguationData":[TD([[makeQuery(id+"F0.imprint","IMPRINT",EDGE,{"disambiguationData":[TD([[subQ2,1.0]])],"derivedFrom":subQ1}),-1.0]])]});}
            var Q377;
            {var subQ0=sQuery(id+"F0.wireOp",EDGE,"E2.3.6.1");var subQ1=sQuery(id+"F0.wireOp",EDGE,"E2.2.6.0");var subQ2=makeQuery(id+"F0.imprint","INTERSECT",VERTEX,{"derivedFrom":[subQ1,subQ0]});Q377=makeQuery(id+"F0.imprint","IMPRINT",FACE,{"disambiguationData":[TD([[makeQuery(id+"F0.imprint","IMPRINT",EDGE,{"disambiguationData":[TD([[subQ2,1.0]])],"derivedFrom":subQ1}),-1.0]])]});}
            var Q378;
            {var subQ0=sQuery(id+"F0.wireOp",EDGE,"E2.1.3.1");var subQ1=sQuery(id+"F0.wireOp",EDGE,"E2.0.3.0");var subQ2=makeQuery(id+"F0.imprint","INTERSECT",VERTEX,{"derivedFrom":[subQ1,subQ0]});Q378=makeQuery(id+"F0.imprint","IMPRINT",FACE,{"disambiguationData":[TD([[makeQuery(id+"F0.imprint","IMPRINT",EDGE,{"disambiguationData":[TD([[subQ2,1.0]])],"derivedFrom":subQ1}),-1.0]])]});}
            var Q379;
            {var subQ0=sQuery(id+"F0.wireOp",EDGE,"E2.1.6.1");var subQ1=sQuery(id+"F0.wireOp",EDGE,"E2.0.6.0");var subQ2=makeQuery(id+"F0.imprint","INTERSECT",VERTEX,{"derivedFrom":[subQ1,subQ0]});Q379=makeQuery(id+"F0.imprint","IMPRINT",FACE,{"disambiguationData":[TD([[makeQuery(id+"F0.imprint","IMPRINT",EDGE,{"disambiguationData":[TD([[subQ2,1.0]])],"derivedFrom":subQ1}),-1.0]])]});}
            var Q380;
            {var subQ0=sQuery(id+"F0.wireOp",EDGE,"E2.2.2.0");var subQ1=sQuery(id+"F0.wireOp",EDGE,"E2.1.2.0");var subQ2=makeQuery(id+"F0.imprint","INTERSECT",VERTEX,{"disambiguationData":[OD(0.0)],"derivedFrom":[subQ1,subQ0]});Q380=makeQuery(id+"F0.imprint","IMPRINT",FACE,{"disambiguationData":[TD([[makeQuery(id+"F0.imprint","IMPRINT",EDGE,{"disambiguationData":[TD([[subQ2,1.0]])],"derivedFrom":subQ1}),-1.0]])]});}
            var Q381;
            {var subQ0=sQuery(id+"F0.wireOp",EDGE,"E2.2.4.0");var subQ1=sQuery(id+"F0.wireOp",EDGE,"E2.1.4.0");var subQ2=makeQuery(id+"F0.imprint","INTERSECT",VERTEX,{"disambiguationData":[OD(0.0)],"derivedFrom":[subQ1,subQ0]});Q381=makeQuery(id+"F0.imprint","IMPRINT",FACE,{"disambiguationData":[TD([[makeQuery(id+"F0.imprint","IMPRINT",EDGE,{"disambiguationData":[TD([[subQ2,1.0]])],"derivedFrom":subQ1}),-1.0]])]});}
            var Q382;
            {var subQ0=sQuery(id+"F0.wireOp",EDGE,"E2.9.0.0");var subQ1=sQuery(id+"F0.wireOp",EDGE,"E2.8.0.0");var subQ2=makeQuery(id+"F0.imprint","INTERSECT",VERTEX,{"disambiguationData":[OD(0.0)],"derivedFrom":[subQ1,subQ0]});Q382=makeQuery(id+"F0.imprint","IMPRINT",FACE,{"disambiguationData":[TD([[makeQuery(id+"F0.imprint","IMPRINT",EDGE,{"disambiguationData":[TD([[subQ2,-1.0]])],"derivedFrom":subQ1}),-1.0]])]});}
            var Q383;
            {var subQ0=sQuery(id+"F0.wireOp",EDGE,"E2.0.2.0");var subQ1=sQuery(id+"F0.wireOp",EDGE,"E2.0.1.0");var subQ2=makeQuery(id+"F0.imprint","INTERSECT",VERTEX,{"disambiguationData":[OD(1.0)],"derivedFrom":[subQ1,subQ0]});Q383=makeQuery(id+"F0.imprint","IMPRINT",FACE,{"disambiguationData":[TD([[makeQuery(id+"F0.imprint","IMPRINT",EDGE,{"disambiguationData":[TD([[subQ2,-1.0]])],"derivedFrom":subQ1}),1.0]])]});}
            var Q384;
            {var subQ0=sQuery(id+"F0.wireOp",EDGE,"E2.10.2.0");var subQ1=sQuery(id+"F0.wireOp",EDGE,"E2.9.2.0");var subQ2=makeQuery(id+"F0.imprint","INTERSECT",VERTEX,{"disambiguationData":[OD(0.0)],"derivedFrom":[subQ1,subQ0]});Q384=makeQuery(id+"F0.imprint","IMPRINT",FACE,{"disambiguationData":[TD([[makeQuery(id+"F0.imprint","IMPRINT",EDGE,{"disambiguationData":[TD([[subQ2,1.0]])],"derivedFrom":subQ1}),1.0]])]});}
            var Q385;
            {var subQ0=sQuery(id+"F0.wireOp",EDGE,"E2.10.4.0");var subQ1=sQuery(id+"F0.wireOp",EDGE,"E2.9.4.0");var subQ2=makeQuery(id+"F0.imprint","INTERSECT",VERTEX,{"disambiguationData":[OD(0.0)],"derivedFrom":[subQ1,subQ0]});Q385=makeQuery(id+"F0.imprint","IMPRINT",FACE,{"disambiguationData":[TD([[makeQuery(id+"F0.imprint","IMPRINT",EDGE,{"disambiguationData":[TD([[subQ2,1.0]])],"derivedFrom":subQ1}),1.0]])]});}
            var Q386;
            {var subQ0=sQuery(id+"F0.wireOp",EDGE,"E2.10.6.0");var subQ1=sQuery(id+"F0.wireOp",EDGE,"E2.9.6.0");var subQ2=makeQuery(id+"F0.imprint","INTERSECT",VERTEX,{"disambiguationData":[OD(0.0)],"derivedFrom":[subQ1,subQ0]});Q386=makeQuery(id+"F0.imprint","IMPRINT",FACE,{"disambiguationData":[TD([[makeQuery(id+"F0.imprint","IMPRINT",EDGE,{"disambiguationData":[TD([[subQ2,1.0]])],"derivedFrom":subQ1}),1.0]])]});}
            var Q387;
            {var subQ0=sQuery(id+"F0.wireOp",EDGE,"E2.8.6.0");var subQ1=sQuery(id+"F0.wireOp",EDGE,"E2.7.6.0");var subQ2=makeQuery(id+"F0.imprint","INTERSECT",VERTEX,{"disambiguationData":[OD(0.0)],"derivedFrom":[subQ1,subQ0]});Q387=makeQuery(id+"F0.imprint","IMPRINT",FACE,{"disambiguationData":[TD([[makeQuery(id+"F0.imprint","IMPRINT",EDGE,{"disambiguationData":[TD([[subQ2,1.0]])],"derivedFrom":subQ1}),1.0]])]});}
            var Q388;
            {var subQ0=sQuery(id+"F0.wireOp",EDGE,"E2.9.2.0");var subQ1=sQuery(id+"F0.wireOp",EDGE,"E2.8.2.0");var subQ2=makeQuery(id+"F0.imprint","INTERSECT",VERTEX,{"disambiguationData":[OD(0.0)],"derivedFrom":[subQ1,subQ0]});Q388=makeQuery(id+"F0.imprint","IMPRINT",FACE,{"disambiguationData":[TD([[makeQuery(id+"F0.imprint","IMPRINT",EDGE,{"disambiguationData":[TD([[subQ2,1.0]])],"derivedFrom":subQ1}),1.0]])]});}
            var Q389;
            {var subQ0=sQuery(id+"F0.wireOp",EDGE,"E2.9.4.0");var subQ1=sQuery(id+"F0.wireOp",EDGE,"E2.8.4.0");var subQ2=makeQuery(id+"F0.imprint","INTERSECT",VERTEX,{"disambiguationData":[OD(0.0)],"derivedFrom":[subQ1,subQ0]});Q389=makeQuery(id+"F0.imprint","IMPRINT",FACE,{"disambiguationData":[TD([[makeQuery(id+"F0.imprint","IMPRINT",EDGE,{"disambiguationData":[TD([[subQ2,1.0]])],"derivedFrom":subQ1}),1.0]])]});}
            var Q390;
            {var subQ0=sQuery(id+"F0.wireOp",EDGE,"E2.9.6.0");var subQ1=sQuery(id+"F0.wireOp",EDGE,"E2.8.6.0");var subQ2=makeQuery(id+"F0.imprint","INTERSECT",VERTEX,{"disambiguationData":[OD(0.0)],"derivedFrom":[subQ1,subQ0]});Q390=makeQuery(id+"F0.imprint","IMPRINT",FACE,{"disambiguationData":[TD([[makeQuery(id+"F0.imprint","IMPRINT",EDGE,{"disambiguationData":[TD([[subQ2,1.0]])],"derivedFrom":subQ1}),1.0]])]});}
            var Q391;
            {var subQ0=sQuery(id+"F0.wireOp",EDGE,"E2.8.4.0");var subQ1=sQuery(id+"F0.wireOp",EDGE,"E2.7.4.0");var subQ2=makeQuery(id+"F0.imprint","INTERSECT",VERTEX,{"disambiguationData":[OD(0.0)],"derivedFrom":[subQ1,subQ0]});Q391=makeQuery(id+"F0.imprint","IMPRINT",FACE,{"disambiguationData":[TD([[makeQuery(id+"F0.imprint","IMPRINT",EDGE,{"disambiguationData":[TD([[subQ2,1.0]])],"derivedFrom":subQ1}),1.0]])]});}
            var Q392;
            {var subQ0=sQuery(id+"F0.wireOp",EDGE,"E2.8.2.0");var subQ1=sQuery(id+"F0.wireOp",EDGE,"E2.7.2.0");var subQ2=makeQuery(id+"F0.imprint","INTERSECT",VERTEX,{"disambiguationData":[OD(0.0)],"derivedFrom":[subQ1,subQ0]});Q392=makeQuery(id+"F0.imprint","IMPRINT",FACE,{"disambiguationData":[TD([[makeQuery(id+"F0.imprint","IMPRINT",EDGE,{"disambiguationData":[TD([[subQ2,1.0]])],"derivedFrom":subQ1}),1.0]])]});}
            var Q393;
            {var subQ0=sQuery(id+"F0.wireOp",EDGE,"E2.7.2.0");var subQ1=sQuery(id+"F0.wireOp",EDGE,"E2.6.2.0");var subQ2=makeQuery(id+"F0.imprint","INTERSECT",VERTEX,{"disambiguationData":[OD(0.0)],"derivedFrom":[subQ1,subQ0]});Q393=makeQuery(id+"F0.imprint","IMPRINT",FACE,{"disambiguationData":[TD([[makeQuery(id+"F0.imprint","IMPRINT",EDGE,{"disambiguationData":[TD([[subQ2,1.0]])],"derivedFrom":subQ1}),1.0]])]});}
            var Q394;
            {var subQ0=sQuery(id+"F0.wireOp",EDGE,"E2.7.4.0");var subQ1=sQuery(id+"F0.wireOp",EDGE,"E2.6.4.0");var subQ2=makeQuery(id+"F0.imprint","INTERSECT",VERTEX,{"disambiguationData":[OD(0.0)],"derivedFrom":[subQ1,subQ0]});Q394=makeQuery(id+"F0.imprint","IMPRINT",FACE,{"disambiguationData":[TD([[makeQuery(id+"F0.imprint","IMPRINT",EDGE,{"disambiguationData":[TD([[subQ2,1.0]])],"derivedFrom":subQ1}),1.0]])]});}
            var Q395;
            {var subQ0=sQuery(id+"F0.wireOp",EDGE,"E2.7.6.0");var subQ1=sQuery(id+"F0.wireOp",EDGE,"E2.6.6.0");var subQ2=makeQuery(id+"F0.imprint","INTERSECT",VERTEX,{"disambiguationData":[OD(0.0)],"derivedFrom":[subQ1,subQ0]});Q395=makeQuery(id+"F0.imprint","IMPRINT",FACE,{"disambiguationData":[TD([[makeQuery(id+"F0.imprint","IMPRINT",EDGE,{"disambiguationData":[TD([[subQ2,1.0]])],"derivedFrom":subQ1}),1.0]])]});}
            var Q396;
            {var subQ0=sQuery(id+"F0.wireOp",EDGE,"E2.5.4.0");var subQ1=sQuery(id+"F0.wireOp",EDGE,"E2.4.4.0");var subQ2=makeQuery(id+"F0.imprint","INTERSECT",VERTEX,{"disambiguationData":[OD(0.0)],"derivedFrom":[subQ1,subQ0]});Q396=makeQuery(id+"F0.imprint","IMPRINT",FACE,{"disambiguationData":[TD([[makeQuery(id+"F0.imprint","IMPRINT",EDGE,{"disambiguationData":[TD([[subQ2,1.0]])],"derivedFrom":subQ1}),1.0]])]});}
            var Q397;
            {var subQ0=sQuery(id+"F0.wireOp",EDGE,"E2.5.6.0");var subQ1=sQuery(id+"F0.wireOp",EDGE,"E2.4.6.0");var subQ2=makeQuery(id+"F0.imprint","INTERSECT",VERTEX,{"disambiguationData":[OD(0.0)],"derivedFrom":[subQ1,subQ0]});Q397=makeQuery(id+"F0.imprint","IMPRINT",FACE,{"disambiguationData":[TD([[makeQuery(id+"F0.imprint","IMPRINT",EDGE,{"disambiguationData":[TD([[subQ2,1.0]])],"derivedFrom":subQ1}),1.0]])]});}
            var Q398;
            {var subQ0=sQuery(id+"F0.wireOp",EDGE,"E2.4.2.0");var subQ1=sQuery(id+"F0.wireOp",EDGE,"E2.3.2.0");var subQ2=makeQuery(id+"F0.imprint","INTERSECT",VERTEX,{"disambiguationData":[OD(0.0)],"derivedFrom":[subQ1,subQ0]});Q398=makeQuery(id+"F0.imprint","IMPRINT",FACE,{"disambiguationData":[TD([[makeQuery(id+"F0.imprint","IMPRINT",EDGE,{"disambiguationData":[TD([[subQ2,1.0]])],"derivedFrom":subQ1}),1.0]])]});}
            var Q399;
            {var subQ0=sQuery(id+"F0.wireOp",EDGE,"E2.4.4.0");var subQ1=sQuery(id+"F0.wireOp",EDGE,"E2.3.4.0");var subQ2=makeQuery(id+"F0.imprint","INTERSECT",VERTEX,{"disambiguationData":[OD(0.0)],"derivedFrom":[subQ1,subQ0]});Q399=makeQuery(id+"F0.imprint","IMPRINT",FACE,{"disambiguationData":[TD([[makeQuery(id+"F0.imprint","IMPRINT",EDGE,{"disambiguationData":[TD([[subQ2,1.0]])],"derivedFrom":subQ1}),1.0]])]});}
            var Q400;
            {var subQ0=sQuery(id+"F0.wireOp",EDGE,"E2.4.6.0");var subQ1=sQuery(id+"F0.wireOp",EDGE,"E2.3.6.0");var subQ2=makeQuery(id+"F0.imprint","INTERSECT",VERTEX,{"disambiguationData":[OD(0.0)],"derivedFrom":[subQ1,subQ0]});Q400=makeQuery(id+"F0.imprint","IMPRINT",FACE,{"disambiguationData":[TD([[makeQuery(id+"F0.imprint","IMPRINT",EDGE,{"disambiguationData":[TD([[subQ2,1.0]])],"derivedFrom":subQ1}),1.0]])]});}
            var Q401;
            {var subQ0=sQuery(id+"F0.wireOp",EDGE,"E2.5.2.0");var subQ1=sQuery(id+"F0.wireOp",EDGE,"E2.4.2.0");var subQ2=makeQuery(id+"F0.imprint","INTERSECT",VERTEX,{"disambiguationData":[OD(0.0)],"derivedFrom":[subQ1,subQ0]});Q401=makeQuery(id+"F0.imprint","IMPRINT",FACE,{"disambiguationData":[TD([[makeQuery(id+"F0.imprint","IMPRINT",EDGE,{"disambiguationData":[TD([[subQ2,1.0]])],"derivedFrom":subQ1}),1.0]])]});}
            var Q402;
            {var subQ0=sQuery(id+"F0.wireOp",EDGE,"E2.2.6.0");var subQ1=sQuery(id+"F0.wireOp",EDGE,"E2.1.6.0");var subQ2=makeQuery(id+"F0.imprint","INTERSECT",VERTEX,{"disambiguationData":[OD(0.0)],"derivedFrom":[subQ1,subQ0]});Q402=makeQuery(id+"F0.imprint","IMPRINT",FACE,{"disambiguationData":[TD([[makeQuery(id+"F0.imprint","IMPRINT",EDGE,{"disambiguationData":[TD([[subQ2,1.0]])],"derivedFrom":subQ1}),1.0]])]});}
            var Q403;
            {var subQ0=sQuery(id+"F0.wireOp",EDGE,"E2.3.2.0");var subQ1=sQuery(id+"F0.wireOp",EDGE,"E2.2.2.0");var subQ2=makeQuery(id+"F0.imprint","INTERSECT",VERTEX,{"disambiguationData":[OD(0.0)],"derivedFrom":[subQ1,subQ0]});Q403=makeQuery(id+"F0.imprint","IMPRINT",FACE,{"disambiguationData":[TD([[makeQuery(id+"F0.imprint","IMPRINT",EDGE,{"disambiguationData":[TD([[subQ2,1.0]])],"derivedFrom":subQ1}),1.0]])]});}
            var Q404;
            {var subQ0=sQuery(id+"F0.wireOp",EDGE,"E2.3.4.0");var subQ1=sQuery(id+"F0.wireOp",EDGE,"E2.2.4.0");var subQ2=makeQuery(id+"F0.imprint","INTERSECT",VERTEX,{"disambiguationData":[OD(0.0)],"derivedFrom":[subQ1,subQ0]});Q404=makeQuery(id+"F0.imprint","IMPRINT",FACE,{"disambiguationData":[TD([[makeQuery(id+"F0.imprint","IMPRINT",EDGE,{"disambiguationData":[TD([[subQ2,1.0]])],"derivedFrom":subQ1}),1.0]])]});}
            var Q405;
            {var subQ0=sQuery(id+"F0.wireOp",EDGE,"E2.3.6.0");var subQ1=sQuery(id+"F0.wireOp",EDGE,"E2.2.6.0");var subQ2=makeQuery(id+"F0.imprint","INTERSECT",VERTEX,{"disambiguationData":[OD(0.0)],"derivedFrom":[subQ1,subQ0]});Q405=makeQuery(id+"F0.imprint","IMPRINT",FACE,{"disambiguationData":[TD([[makeQuery(id+"F0.imprint","IMPRINT",EDGE,{"disambiguationData":[TD([[subQ2,1.0]])],"derivedFrom":subQ1}),1.0]])]});}
            var Q406;
            {var subQ0=sQuery(id+"F0.wireOp",EDGE,"E2.0.4.0");var subQ1=sQuery(id+"F0.wireOp",EDGE,"E2.0.3.0");var subQ2=makeQuery(id+"F0.imprint","INTERSECT",VERTEX,{"disambiguationData":[OD(1.0)],"derivedFrom":[subQ1,subQ0]});Q406=makeQuery(id+"F0.imprint","IMPRINT",FACE,{"disambiguationData":[TD([[makeQuery(id+"F0.imprint","IMPRINT",EDGE,{"disambiguationData":[TD([[subQ2,-1.0]])],"derivedFrom":subQ1}),-1.0]])]});}
            var Q407;
            {var subQ0=sQuery(id+"F0.wireOp",EDGE,"E2.2.2.0");var subQ1=sQuery(id+"F0.wireOp",EDGE,"E2.1.2.0");var subQ2=makeQuery(id+"F0.imprint","INTERSECT",VERTEX,{"disambiguationData":[OD(0.0)],"derivedFrom":[subQ1,subQ0]});Q407=makeQuery(id+"F0.imprint","IMPRINT",FACE,{"disambiguationData":[TD([[makeQuery(id+"F0.imprint","IMPRINT",EDGE,{"disambiguationData":[TD([[subQ2,1.0]])],"derivedFrom":subQ1}),1.0]])]});}
            var Q408;
            {var subQ0=sQuery(id+"F0.wireOp",EDGE,"E2.2.4.0");var subQ1=sQuery(id+"F0.wireOp",EDGE,"E2.1.4.0");var subQ2=makeQuery(id+"F0.imprint","INTERSECT",VERTEX,{"disambiguationData":[OD(0.0)],"derivedFrom":[subQ1,subQ0]});Q408=makeQuery(id+"F0.imprint","IMPRINT",FACE,{"disambiguationData":[TD([[makeQuery(id+"F0.imprint","IMPRINT",EDGE,{"disambiguationData":[TD([[subQ2,1.0]])],"derivedFrom":subQ1}),1.0]])]});}
            var Q409;
            {var subQ0=sQuery(id+"F0.wireOp",EDGE,"E2.11.3.0");var subQ1=sQuery(id+"F0.wireOp",EDGE,"E2.11.2.0");var subQ2=makeQuery(id+"F0.imprint","INTERSECT",VERTEX,{"disambiguationData":[OD(0.0)],"derivedFrom":[subQ1,subQ0]});Q409=makeQuery(id+"F0.imprint","IMPRINT",FACE,{"disambiguationData":[TD([[makeQuery(id+"F0.imprint","IMPRINT",EDGE,{"disambiguationData":[TD([[subQ2,-1.0]])],"derivedFrom":subQ1}),-1.0]])]});}
            var Q410;
            {var subQ0=sQuery(id+"F0.wireOp",EDGE,"E2.3.2.0");var subQ1=sQuery(id+"F0.wireOp",EDGE,"E2.2.2.0");var subQ2=makeQuery(id+"F0.imprint","INTERSECT",VERTEX,{"disambiguationData":[OD(0.0)],"derivedFrom":[subQ1,subQ0]});Q410=makeQuery(id+"F0.imprint","IMPRINT",FACE,{"disambiguationData":[TD([[makeQuery(id+"F0.imprint","IMPRINT",EDGE,{"disambiguationData":[TD([[subQ2,-1.0]])],"derivedFrom":subQ1}),1.0]])]});}
            var Q411;
            {var subQ0=sQuery(id+"F0.wireOp",EDGE,"E2.3.4.0");var subQ1=sQuery(id+"F0.wireOp",EDGE,"E2.2.4.0");var subQ2=makeQuery(id+"F0.imprint","INTERSECT",VERTEX,{"disambiguationData":[OD(0.0)],"derivedFrom":[subQ1,subQ0]});Q411=makeQuery(id+"F0.imprint","IMPRINT",FACE,{"disambiguationData":[TD([[makeQuery(id+"F0.imprint","IMPRINT",EDGE,{"disambiguationData":[TD([[subQ2,-1.0]])],"derivedFrom":subQ1}),1.0]])]});}
            var Q412;
            {var subQ0=sQuery(id+"F0.wireOp",EDGE,"E2.4.0.0");var subQ1=sQuery(id+"F0.wireOp",EDGE,"E2.3.0.0");var subQ2=makeQuery(id+"F0.imprint","INTERSECT",VERTEX,{"disambiguationData":[OD(1.0)],"derivedFrom":[subQ1,subQ0]});Q412=makeQuery(id+"F0.imprint","IMPRINT",FACE,{"disambiguationData":[TD([[makeQuery(id+"F0.imprint","IMPRINT",EDGE,{"disambiguationData":[TD([[subQ2,1.0]])],"derivedFrom":subQ1}),1.0]])]});}
            var Q413;
            {var subQ0=sQuery(id+"F0.wireOp",EDGE,"E2.4.2.0");var subQ1=sQuery(id+"F0.wireOp",EDGE,"E2.3.2.0");var subQ2=makeQuery(id+"F0.imprint","INTERSECT",VERTEX,{"disambiguationData":[OD(0.0)],"derivedFrom":[subQ1,subQ0]});Q413=makeQuery(id+"F0.imprint","IMPRINT",FACE,{"disambiguationData":[TD([[makeQuery(id+"F0.imprint","IMPRINT",EDGE,{"disambiguationData":[TD([[subQ2,-1.0]])],"derivedFrom":subQ1}),1.0]])]});}
            var Q414;
            {var subQ0=sQuery(id+"F0.wireOp",EDGE,"E2.2.0.0");var subQ1=sQuery(id+"F0.wireOp",EDGE,"E2.1.0.0");var subQ2=makeQuery(id+"F0.imprint","INTERSECT",VERTEX,{"disambiguationData":[OD(1.0)],"derivedFrom":[subQ1,subQ0]});Q414=makeQuery(id+"F0.imprint","IMPRINT",FACE,{"disambiguationData":[TD([[makeQuery(id+"F0.imprint","IMPRINT",EDGE,{"disambiguationData":[TD([[subQ2,1.0]])],"derivedFrom":subQ1}),1.0]])]});}
            var Q415;
            {var subQ0=sQuery(id+"F0.wireOp",EDGE,"E2.2.2.0");var subQ1=sQuery(id+"F0.wireOp",EDGE,"E2.1.2.0");var subQ2=makeQuery(id+"F0.imprint","INTERSECT",VERTEX,{"disambiguationData":[OD(0.0)],"derivedFrom":[subQ1,subQ0]});Q415=makeQuery(id+"F0.imprint","IMPRINT",FACE,{"disambiguationData":[TD([[makeQuery(id+"F0.imprint","IMPRINT",EDGE,{"disambiguationData":[TD([[subQ2,-1.0]])],"derivedFrom":subQ1}),1.0]])]});}
            var Q416;
            {var subQ0=sQuery(id+"F0.wireOp",EDGE,"E2.2.4.0");var subQ1=sQuery(id+"F0.wireOp",EDGE,"E2.1.4.0");var subQ2=makeQuery(id+"F0.imprint","INTERSECT",VERTEX,{"disambiguationData":[OD(0.0)],"derivedFrom":[subQ1,subQ0]});Q416=makeQuery(id+"F0.imprint","IMPRINT",FACE,{"disambiguationData":[TD([[makeQuery(id+"F0.imprint","IMPRINT",EDGE,{"disambiguationData":[TD([[subQ2,-1.0]])],"derivedFrom":subQ1}),1.0]])]});}
            var Q417;
            {var subQ0=sQuery(id+"F0.wireOp",EDGE,"E2.3.0.0");var subQ1=sQuery(id+"F0.wireOp",EDGE,"E2.2.0.0");var subQ2=makeQuery(id+"F0.imprint","INTERSECT",VERTEX,{"disambiguationData":[OD(1.0)],"derivedFrom":[subQ1,subQ0]});Q417=makeQuery(id+"F0.imprint","IMPRINT",FACE,{"disambiguationData":[TD([[makeQuery(id+"F0.imprint","IMPRINT",EDGE,{"disambiguationData":[TD([[subQ2,1.0]])],"derivedFrom":subQ1}),1.0]])]});}
            var Q418;
            {var subQ0=sQuery(id+"F0.wireOp",EDGE,"E2.11.4.0");var subQ1=sQuery(id+"F0.wireOp",EDGE,"E2.11.3.0");var subQ2=makeQuery(id+"F0.imprint","INTERSECT",VERTEX,{"disambiguationData":[OD(0.0)],"derivedFrom":[subQ1,subQ0]});Q418=makeQuery(id+"F0.imprint","IMPRINT",FACE,{"disambiguationData":[TD([[makeQuery(id+"F0.imprint","IMPRINT",EDGE,{"disambiguationData":[TD([[subQ2,-1.0]])],"derivedFrom":subQ1}),-1.0]])]});}
            var Q419;
            {var subQ0=sQuery(id+"F0.wireOp",EDGE,"E2.0.2.0");var subQ1=sQuery(id+"F0.wireOp",EDGE,"E2.0.1.0");var subQ2=makeQuery(id+"F0.imprint","INTERSECT",VERTEX,{"disambiguationData":[OD(1.0)],"derivedFrom":[subQ1,subQ0]});Q419=makeQuery(id+"F0.imprint","IMPRINT",FACE,{"disambiguationData":[TD([[makeQuery(id+"F0.imprint","IMPRINT",EDGE,{"disambiguationData":[TD([[subQ2,-1.0]])],"derivedFrom":subQ1}),-1.0]])]});}
            var Q420;
            {var subQ0=sQuery(id+"F0.wireOp",EDGE,"E2.11.1.0");var subQ1=sQuery(id+"F0.wireOp",EDGE,"E2.11.0.0");var subQ2=makeQuery(id+"F0.imprint","INTERSECT",VERTEX,{"disambiguationData":[OD(0.0)],"derivedFrom":[subQ1,subQ0]});Q420=makeQuery(id+"F0.imprint","IMPRINT",FACE,{"disambiguationData":[TD([[makeQuery(id+"F0.imprint","IMPRINT",EDGE,{"disambiguationData":[TD([[subQ2,-1.0]])],"derivedFrom":subQ1}),1.0]])]});}
            var Q421;
            {var subQ0=sQuery(id+"F0.wireOp",EDGE,"E2.11.2.0");var subQ1=sQuery(id+"F0.wireOp",EDGE,"E2.10.2.0");var subQ2=makeQuery(id+"F0.imprint","INTERSECT",VERTEX,{"disambiguationData":[OD(0.0)],"derivedFrom":[subQ1,subQ0]});Q421=makeQuery(id+"F0.imprint","IMPRINT",FACE,{"disambiguationData":[TD([[makeQuery(id+"F0.imprint","IMPRINT",EDGE,{"disambiguationData":[TD([[subQ2,-1.0]])],"derivedFrom":subQ1}),1.0]])]});}
            var Q422;
            {var subQ0=sQuery(id+"F0.wireOp",EDGE,"E2.11.4.0");var subQ1=sQuery(id+"F0.wireOp",EDGE,"E2.10.4.0");var subQ2=makeQuery(id+"F0.imprint","INTERSECT",VERTEX,{"disambiguationData":[OD(0.0)],"derivedFrom":[subQ1,subQ0]});Q422=makeQuery(id+"F0.imprint","IMPRINT",FACE,{"disambiguationData":[TD([[makeQuery(id+"F0.imprint","IMPRINT",EDGE,{"disambiguationData":[TD([[subQ2,-1.0]])],"derivedFrom":subQ1}),1.0]])]});}
            var Q423;
            {var subQ0=sQuery(id+"F0.wireOp",EDGE,"E2.9.2.0");var subQ1=sQuery(id+"F0.wireOp",EDGE,"E2.8.2.0");var subQ2=makeQuery(id+"F0.imprint","INTERSECT",VERTEX,{"disambiguationData":[OD(0.0)],"derivedFrom":[subQ1,subQ0]});Q423=makeQuery(id+"F0.imprint","IMPRINT",FACE,{"disambiguationData":[TD([[makeQuery(id+"F0.imprint","IMPRINT",EDGE,{"disambiguationData":[TD([[subQ2,-1.0]])],"derivedFrom":subQ1}),1.0]])]});}
            var Q424;
            {var subQ0=sQuery(id+"F0.wireOp",EDGE,"E2.9.4.0");var subQ1=sQuery(id+"F0.wireOp",EDGE,"E2.8.4.0");var subQ2=makeQuery(id+"F0.imprint","INTERSECT",VERTEX,{"disambiguationData":[OD(0.0)],"derivedFrom":[subQ1,subQ0]});Q424=makeQuery(id+"F0.imprint","IMPRINT",FACE,{"disambiguationData":[TD([[makeQuery(id+"F0.imprint","IMPRINT",EDGE,{"disambiguationData":[TD([[subQ2,-1.0]])],"derivedFrom":subQ1}),1.0]])]});}
            var Q425;
            {var subQ0=sQuery(id+"F0.wireOp",EDGE,"E2.10.0.0");var subQ1=sQuery(id+"F0.wireOp",EDGE,"E2.9.0.0");var subQ2=makeQuery(id+"F0.imprint","INTERSECT",VERTEX,{"disambiguationData":[OD(1.0)],"derivedFrom":[subQ1,subQ0]});Q425=makeQuery(id+"F0.imprint","IMPRINT",FACE,{"disambiguationData":[TD([[makeQuery(id+"F0.imprint","IMPRINT",EDGE,{"disambiguationData":[TD([[subQ2,1.0]])],"derivedFrom":subQ1}),1.0]])]});}
            var Q426;
            {var subQ0=sQuery(id+"F0.wireOp",EDGE,"E2.10.2.0");var subQ1=sQuery(id+"F0.wireOp",EDGE,"E2.9.2.0");var subQ2=makeQuery(id+"F0.imprint","INTERSECT",VERTEX,{"disambiguationData":[OD(0.0)],"derivedFrom":[subQ1,subQ0]});Q426=makeQuery(id+"F0.imprint","IMPRINT",FACE,{"disambiguationData":[TD([[makeQuery(id+"F0.imprint","IMPRINT",EDGE,{"disambiguationData":[TD([[subQ2,-1.0]])],"derivedFrom":subQ1}),1.0]])]});}
            var Q427;
            {var subQ0=sQuery(id+"F0.wireOp",EDGE,"E2.8.4.0");var subQ1=sQuery(id+"F0.wireOp",EDGE,"E2.7.4.0");var subQ2=makeQuery(id+"F0.imprint","INTERSECT",VERTEX,{"disambiguationData":[OD(0.0)],"derivedFrom":[subQ1,subQ0]});Q427=makeQuery(id+"F0.imprint","IMPRINT",FACE,{"disambiguationData":[TD([[makeQuery(id+"F0.imprint","IMPRINT",EDGE,{"disambiguationData":[TD([[subQ2,-1.0]])],"derivedFrom":subQ1}),1.0]])]});}
            var Q428;
            {var subQ0=sQuery(id+"F0.wireOp",EDGE,"E2.9.0.0");var subQ1=sQuery(id+"F0.wireOp",EDGE,"E2.8.0.0");var subQ2=makeQuery(id+"F0.imprint","INTERSECT",VERTEX,{"disambiguationData":[OD(1.0)],"derivedFrom":[subQ1,subQ0]});Q428=makeQuery(id+"F0.imprint","IMPRINT",FACE,{"disambiguationData":[TD([[makeQuery(id+"F0.imprint","IMPRINT",EDGE,{"disambiguationData":[TD([[subQ2,1.0]])],"derivedFrom":subQ1}),1.0]])]});}
            var Q429;
            {var subQ0=sQuery(id+"F0.wireOp",EDGE,"E2.7.2.0");var subQ1=sQuery(id+"F0.wireOp",EDGE,"E2.6.2.0");var subQ2=makeQuery(id+"F0.imprint","INTERSECT",VERTEX,{"disambiguationData":[OD(0.0)],"derivedFrom":[subQ1,subQ0]});Q429=makeQuery(id+"F0.imprint","IMPRINT",FACE,{"disambiguationData":[TD([[makeQuery(id+"F0.imprint","IMPRINT",EDGE,{"disambiguationData":[TD([[subQ2,-1.0]])],"derivedFrom":subQ1}),1.0]])]});}
            var Q430;
            {var subQ0=sQuery(id+"F0.wireOp",EDGE,"E2.7.4.0");var subQ1=sQuery(id+"F0.wireOp",EDGE,"E2.6.4.0");var subQ2=makeQuery(id+"F0.imprint","INTERSECT",VERTEX,{"disambiguationData":[OD(0.0)],"derivedFrom":[subQ1,subQ0]});Q430=makeQuery(id+"F0.imprint","IMPRINT",FACE,{"disambiguationData":[TD([[makeQuery(id+"F0.imprint","IMPRINT",EDGE,{"disambiguationData":[TD([[subQ2,-1.0]])],"derivedFrom":subQ1}),1.0]])]});}
            var Q431;
            {var subQ0=sQuery(id+"F0.wireOp",EDGE,"E2.8.0.0");var subQ1=sQuery(id+"F0.wireOp",EDGE,"E2.7.0.0");var subQ2=makeQuery(id+"F0.imprint","INTERSECT",VERTEX,{"disambiguationData":[OD(1.0)],"derivedFrom":[subQ1,subQ0]});Q431=makeQuery(id+"F0.imprint","IMPRINT",FACE,{"disambiguationData":[TD([[makeQuery(id+"F0.imprint","IMPRINT",EDGE,{"disambiguationData":[TD([[subQ2,1.0]])],"derivedFrom":subQ1}),1.0]])]});}
            var Q432;
            {var subQ0=sQuery(id+"F0.wireOp",EDGE,"E2.8.2.0");var subQ1=sQuery(id+"F0.wireOp",EDGE,"E2.7.2.0");var subQ2=makeQuery(id+"F0.imprint","INTERSECT",VERTEX,{"disambiguationData":[OD(0.0)],"derivedFrom":[subQ1,subQ0]});Q432=makeQuery(id+"F0.imprint","IMPRINT",FACE,{"disambiguationData":[TD([[makeQuery(id+"F0.imprint","IMPRINT",EDGE,{"disambiguationData":[TD([[subQ2,-1.0]])],"derivedFrom":subQ1}),1.0]])]});}
            var Q433;
            {var subQ0=sQuery(id+"F0.wireOp",EDGE,"E2.6.2.0");var subQ1=sQuery(id+"F0.wireOp",EDGE,"E2.5.2.0");var subQ2=makeQuery(id+"F0.imprint","INTERSECT",VERTEX,{"disambiguationData":[OD(0.0)],"derivedFrom":[subQ1,subQ0]});Q433=makeQuery(id+"F0.imprint","IMPRINT",FACE,{"disambiguationData":[TD([[makeQuery(id+"F0.imprint","IMPRINT",EDGE,{"disambiguationData":[TD([[subQ2,-1.0]])],"derivedFrom":subQ1}),1.0]])]});}
            var Q434;
            {var subQ0=sQuery(id+"F0.wireOp",EDGE,"E2.6.4.0");var subQ1=sQuery(id+"F0.wireOp",EDGE,"E2.5.4.0");var subQ2=makeQuery(id+"F0.imprint","INTERSECT",VERTEX,{"disambiguationData":[OD(0.0)],"derivedFrom":[subQ1,subQ0]});Q434=makeQuery(id+"F0.imprint","IMPRINT",FACE,{"disambiguationData":[TD([[makeQuery(id+"F0.imprint","IMPRINT",EDGE,{"disambiguationData":[TD([[subQ2,-1.0]])],"derivedFrom":subQ1}),1.0]])]});}
            var Q435;
            {var subQ0=sQuery(id+"F0.wireOp",EDGE,"E2.7.0.0");var subQ1=sQuery(id+"F0.wireOp",EDGE,"E2.6.0.0");var subQ2=makeQuery(id+"F0.imprint","INTERSECT",VERTEX,{"disambiguationData":[OD(1.0)],"derivedFrom":[subQ1,subQ0]});Q435=makeQuery(id+"F0.imprint","IMPRINT",FACE,{"disambiguationData":[TD([[makeQuery(id+"F0.imprint","IMPRINT",EDGE,{"disambiguationData":[TD([[subQ2,1.0]])],"derivedFrom":subQ1}),1.0]])]});}
            var Q436;
            {var subQ0=sQuery(id+"F0.wireOp",EDGE,"E2.4.4.0");var subQ1=sQuery(id+"F0.wireOp",EDGE,"E2.3.4.0");var subQ2=makeQuery(id+"F0.imprint","INTERSECT",VERTEX,{"disambiguationData":[OD(0.0)],"derivedFrom":[subQ1,subQ0]});Q436=makeQuery(id+"F0.imprint","IMPRINT",FACE,{"disambiguationData":[TD([[makeQuery(id+"F0.imprint","IMPRINT",EDGE,{"disambiguationData":[TD([[subQ2,-1.0]])],"derivedFrom":subQ1}),1.0]])]});}
            var Q437;
            {var subQ0=sQuery(id+"F0.wireOp",EDGE,"E2.5.0.0");var subQ1=sQuery(id+"F0.wireOp",EDGE,"E2.4.0.0");var subQ2=makeQuery(id+"F0.imprint","INTERSECT",VERTEX,{"disambiguationData":[OD(1.0)],"derivedFrom":[subQ1,subQ0]});Q437=makeQuery(id+"F0.imprint","IMPRINT",FACE,{"disambiguationData":[TD([[makeQuery(id+"F0.imprint","IMPRINT",EDGE,{"disambiguationData":[TD([[subQ2,1.0]])],"derivedFrom":subQ1}),1.0]])]});}
            var Q438;
            {var subQ0=sQuery(id+"F0.wireOp",EDGE,"E2.5.2.0");var subQ1=sQuery(id+"F0.wireOp",EDGE,"E2.4.2.0");var subQ2=makeQuery(id+"F0.imprint","INTERSECT",VERTEX,{"disambiguationData":[OD(0.0)],"derivedFrom":[subQ1,subQ0]});Q438=makeQuery(id+"F0.imprint","IMPRINT",FACE,{"disambiguationData":[TD([[makeQuery(id+"F0.imprint","IMPRINT",EDGE,{"disambiguationData":[TD([[subQ2,-1.0]])],"derivedFrom":subQ1}),1.0]])]});}
            var Q439;
            {var subQ0=sQuery(id+"F0.wireOp",EDGE,"E2.5.4.0");var subQ1=sQuery(id+"F0.wireOp",EDGE,"E2.4.4.0");var subQ2=makeQuery(id+"F0.imprint","INTERSECT",VERTEX,{"disambiguationData":[OD(0.0)],"derivedFrom":[subQ1,subQ0]});Q439=makeQuery(id+"F0.imprint","IMPRINT",FACE,{"disambiguationData":[TD([[makeQuery(id+"F0.imprint","IMPRINT",EDGE,{"disambiguationData":[TD([[subQ2,-1.0]])],"derivedFrom":subQ1}),1.0]])]});}
            var Q440;
            {var subQ0=sQuery(id+"F0.wireOp",EDGE,"E2.3.4.0");var subQ1=sQuery(id+"F0.wireOp",EDGE,"E2.3.3.0");var subQ2=makeQuery(id+"F0.imprint","INTERSECT",VERTEX,{"disambiguationData":[OD(0.0)],"derivedFrom":[subQ1,subQ0]});Q440=makeQuery(id+"F0.imprint","IMPRINT",FACE,{"disambiguationData":[TD([[makeQuery(id+"F0.imprint","IMPRINT",EDGE,{"disambiguationData":[TD([[subQ2,-1.0]])],"derivedFrom":subQ1}),1.0]])]});}
            var Q441;
            {var subQ0=sQuery(id+"F0.wireOp",EDGE,"E2.0.4.0");var subQ1=sQuery(id+"F0.wireOp",EDGE,"E2.0.3.0");var subQ2=makeQuery(id+"F0.imprint","INTERSECT",VERTEX,{"disambiguationData":[OD(1.0)],"derivedFrom":[subQ1,subQ0]});Q441=makeQuery(id+"F0.imprint","IMPRINT",FACE,{"disambiguationData":[TD([[makeQuery(id+"F0.imprint","IMPRINT",EDGE,{"disambiguationData":[TD([[subQ2,-1.0]])],"derivedFrom":subQ1}),1.0]])]});}
            var Q442;
            {var subQ0=sQuery(id+"F0.wireOp",EDGE,"E2.1.5.1");var subQ1=sQuery(id+"F0.wireOp",EDGE,"E2.0.5.0");var subQ2=makeQuery(id+"F0.imprint","INTERSECT",VERTEX,{"derivedFrom":[subQ1,subQ0]});Q442=makeQuery(id+"F0.imprint","IMPRINT",FACE,{"disambiguationData":[TD([[makeQuery(id+"F0.imprint","IMPRINT",EDGE,{"disambiguationData":[TD([[subQ2,1.0]])],"derivedFrom":subQ1}),-1.0]])]});}
            var Q443;
            {var subQ0=sQuery(id+"F0.wireOp",EDGE,"E2.8.6.0");var subQ1=sQuery(id+"F0.wireOp",EDGE,"E2.7.6.0");var subQ2=makeQuery(id+"F0.imprint","INTERSECT",VERTEX,{"disambiguationData":[OD(0.0)],"derivedFrom":[subQ1,subQ0]});Q443=makeQuery(id+"F0.imprint","IMPRINT",FACE,{"disambiguationData":[TD([[makeQuery(id+"F0.imprint","IMPRINT",EDGE,{"disambiguationData":[TD([[subQ2,1.0]])],"derivedFrom":subQ1}),-1.0]])]});}
            var Q444;
            {var subQ0=sQuery(id+"F0.wireOp",EDGE,"E2.6.3.1");var subQ1=sQuery(id+"F0.wireOp",EDGE,"E2.5.3.0");var subQ2=makeQuery(id+"F0.imprint","INTERSECT",VERTEX,{"derivedFrom":[subQ1,subQ0]});Q444=makeQuery(id+"F0.imprint","IMPRINT",FACE,{"disambiguationData":[TD([[makeQuery(id+"F0.imprint","IMPRINT",EDGE,{"disambiguationData":[TD([[subQ2,1.0]])],"derivedFrom":subQ1}),-1.0]])]});}
            var Q445;
            {var subQ0=sQuery(id+"F0.wireOp",EDGE,"E2.6.5.1");var subQ1=sQuery(id+"F0.wireOp",EDGE,"E2.5.5.0");var subQ2=makeQuery(id+"F0.imprint","INTERSECT",VERTEX,{"derivedFrom":[subQ1,subQ0]});Q445=makeQuery(id+"F0.imprint","IMPRINT",FACE,{"disambiguationData":[TD([[makeQuery(id+"F0.imprint","IMPRINT",EDGE,{"disambiguationData":[TD([[subQ2,1.0]])],"derivedFrom":subQ1}),-1.0]])]});}
            var Q446;
            {var subQ0=sQuery(id+"F0.wireOp",EDGE,"E2.7.1.1");var subQ1=sQuery(id+"F0.wireOp",EDGE,"E2.6.1.0");var subQ2=makeQuery(id+"F0.imprint","INTERSECT",VERTEX,{"derivedFrom":[subQ1,subQ0]});Q446=makeQuery(id+"F0.imprint","IMPRINT",FACE,{"disambiguationData":[TD([[makeQuery(id+"F0.imprint","IMPRINT",EDGE,{"disambiguationData":[TD([[subQ2,1.0]])],"derivedFrom":subQ1}),-1.0]])]});}
            var Q447;
            {var subQ0=sQuery(id+"F0.wireOp",EDGE,"E2.5.1.1");var subQ1=sQuery(id+"F0.wireOp",EDGE,"E2.4.1.0");var subQ2=makeQuery(id+"F0.imprint","INTERSECT",VERTEX,{"derivedFrom":[subQ1,subQ0]});Q447=makeQuery(id+"F0.imprint","IMPRINT",FACE,{"disambiguationData":[TD([[makeQuery(id+"F0.imprint","IMPRINT",EDGE,{"disambiguationData":[TD([[subQ2,1.0]])],"derivedFrom":subQ1}),-1.0]])]});}
            var Q448;
            {var subQ0=sQuery(id+"F0.wireOp",EDGE,"E2.5.3.1");var subQ1=sQuery(id+"F0.wireOp",EDGE,"E2.4.3.0");var subQ2=makeQuery(id+"F0.imprint","INTERSECT",VERTEX,{"derivedFrom":[subQ1,subQ0]});Q448=makeQuery(id+"F0.imprint","IMPRINT",FACE,{"disambiguationData":[TD([[makeQuery(id+"F0.imprint","IMPRINT",EDGE,{"disambiguationData":[TD([[subQ2,1.0]])],"derivedFrom":subQ1}),-1.0]])]});}
            var Q449;
            {var subQ0=sQuery(id+"F0.wireOp",EDGE,"E2.5.5.1");var subQ1=sQuery(id+"F0.wireOp",EDGE,"E2.4.5.0");var subQ2=makeQuery(id+"F0.imprint","INTERSECT",VERTEX,{"derivedFrom":[subQ1,subQ0]});Q449=makeQuery(id+"F0.imprint","IMPRINT",FACE,{"disambiguationData":[TD([[makeQuery(id+"F0.imprint","IMPRINT",EDGE,{"disambiguationData":[TD([[subQ2,1.0]])],"derivedFrom":subQ1}),-1.0]])]});}
            var Q450;
            {var subQ0=sQuery(id+"F0.wireOp",EDGE,"E2.4.1.1");var subQ1=sQuery(id+"F0.wireOp",EDGE,"E2.3.1.0");var subQ2=makeQuery(id+"F0.imprint","INTERSECT",VERTEX,{"derivedFrom":[subQ1,subQ0]});Q450=makeQuery(id+"F0.imprint","IMPRINT",FACE,{"disambiguationData":[TD([[makeQuery(id+"F0.imprint","IMPRINT",EDGE,{"disambiguationData":[TD([[subQ2,1.0]])],"derivedFrom":subQ1}),-1.0]])]});}
            var Q451;
            {var subQ0=sQuery(id+"F0.wireOp",EDGE,"E2.4.5.1");var subQ1=sQuery(id+"F0.wireOp",EDGE,"E2.3.5.0");var subQ2=makeQuery(id+"F0.imprint","INTERSECT",VERTEX,{"derivedFrom":[subQ1,subQ0]});Q451=makeQuery(id+"F0.imprint","IMPRINT",FACE,{"disambiguationData":[TD([[makeQuery(id+"F0.imprint","IMPRINT",EDGE,{"disambiguationData":[TD([[subQ2,1.0]])],"derivedFrom":subQ1}),-1.0]])]});}
            var Q452;
            {var subQ0=sQuery(id+"F0.wireOp",EDGE,"E2.2.3.1");var subQ1=sQuery(id+"F0.wireOp",EDGE,"E2.1.3.0");var subQ2=makeQuery(id+"F0.imprint","INTERSECT",VERTEX,{"derivedFrom":[subQ1,subQ0]});Q452=makeQuery(id+"F0.imprint","IMPRINT",FACE,{"disambiguationData":[TD([[makeQuery(id+"F0.imprint","IMPRINT",EDGE,{"disambiguationData":[TD([[subQ2,1.0]])],"derivedFrom":subQ1}),-1.0]])]});}
            var Q453;
            {var subQ0=sQuery(id+"F0.wireOp",EDGE,"E2.2.5.1");var subQ1=sQuery(id+"F0.wireOp",EDGE,"E2.1.5.0");var subQ2=makeQuery(id+"F0.imprint","INTERSECT",VERTEX,{"derivedFrom":[subQ1,subQ0]});Q453=makeQuery(id+"F0.imprint","IMPRINT",FACE,{"disambiguationData":[TD([[makeQuery(id+"F0.imprint","IMPRINT",EDGE,{"disambiguationData":[TD([[subQ2,1.0]])],"derivedFrom":subQ1}),-1.0]])]});}
            var Q454;
            {var subQ0=sQuery(id+"F0.wireOp",EDGE,"E2.3.1.1");var subQ1=sQuery(id+"F0.wireOp",EDGE,"E2.2.1.0");var subQ2=makeQuery(id+"F0.imprint","INTERSECT",VERTEX,{"derivedFrom":[subQ1,subQ0]});Q454=makeQuery(id+"F0.imprint","IMPRINT",FACE,{"disambiguationData":[TD([[makeQuery(id+"F0.imprint","IMPRINT",EDGE,{"disambiguationData":[TD([[subQ2,1.0]])],"derivedFrom":subQ1}),-1.0]])]});}
            var Q455;
            {var subQ0=sQuery(id+"F0.wireOp",EDGE,"E2.1.1.0");var subQ1=sQuery(id+"F0.wireOp",EDGE,"E2.0.1.0");var subQ2=makeQuery(id+"F0.imprint","INTERSECT",VERTEX,{"disambiguationData":[OD(0.0)],"derivedFrom":[subQ1,subQ0]});Q455=makeQuery(id+"F0.imprint","IMPRINT",FACE,{"disambiguationData":[TD([[makeQuery(id+"F0.imprint","IMPRINT",EDGE,{"disambiguationData":[TD([[subQ2,1.0]])],"derivedFrom":subQ1}),-1.0]])]});}
            var Q456;
            {var subQ0=sQuery(id+"F0.wireOp",EDGE,"E2.0.6.0");var subQ1=sQuery(id+"F0.wireOp",EDGE,"E2.0.5.0");var subQ2=makeQuery(id+"F0.imprint","INTERSECT",VERTEX,{"disambiguationData":[OD(1.0)],"derivedFrom":[subQ1,subQ0]});Q456=makeQuery(id+"F0.imprint","IMPRINT",FACE,{"disambiguationData":[TD([[makeQuery(id+"F0.imprint","IMPRINT",EDGE,{"disambiguationData":[TD([[subQ2,-1.0]])],"derivedFrom":subQ1}),-1.0]])]});}
            var Q457;
            {var subQ0=sQuery(id+"F0.wireOp",EDGE,"E2.2.1.1");var subQ1=sQuery(id+"F0.wireOp",EDGE,"E2.1.1.0");var subQ2=makeQuery(id+"F0.imprint","INTERSECT",VERTEX,{"derivedFrom":[subQ1,subQ0]});Q457=makeQuery(id+"F0.imprint","IMPRINT",FACE,{"disambiguationData":[TD([[makeQuery(id+"F0.imprint","IMPRINT",EDGE,{"disambiguationData":[TD([[subQ2,1.0]])],"derivedFrom":subQ1}),-1.0]])]});}
            var Q458;
            {var subQ0=sQuery(id+"F0.wireOp",EDGE,"E2.11.3.1");var subQ1=sQuery(id+"F0.wireOp",EDGE,"E2.10.3.0");var subQ2=makeQuery(id+"F0.imprint","INTERSECT",VERTEX,{"derivedFrom":[subQ1,subQ0]});Q458=makeQuery(id+"F0.imprint","IMPRINT",FACE,{"disambiguationData":[TD([[makeQuery(id+"F0.imprint","IMPRINT",EDGE,{"disambiguationData":[TD([[subQ2,1.0]])],"derivedFrom":subQ1}),-1.0]])]});}
            var Q459;
            {var subQ0=sQuery(id+"F0.wireOp",EDGE,"E2.11.5.1");var subQ1=sQuery(id+"F0.wireOp",EDGE,"E2.10.5.0");var subQ2=makeQuery(id+"F0.imprint","INTERSECT",VERTEX,{"derivedFrom":[subQ1,subQ0]});Q459=makeQuery(id+"F0.imprint","IMPRINT",FACE,{"disambiguationData":[TD([[makeQuery(id+"F0.imprint","IMPRINT",EDGE,{"disambiguationData":[TD([[subQ2,1.0]])],"derivedFrom":subQ1}),-1.0]])]});}
            var Q460;
            {var subQ0=sQuery(id+"F0.wireOp",EDGE,"E2.9.5.1");var subQ1=sQuery(id+"F0.wireOp",EDGE,"E2.8.5.0");var subQ2=makeQuery(id+"F0.imprint","INTERSECT",VERTEX,{"derivedFrom":[subQ1,subQ0]});Q460=makeQuery(id+"F0.imprint","IMPRINT",FACE,{"disambiguationData":[TD([[makeQuery(id+"F0.imprint","IMPRINT",EDGE,{"disambiguationData":[TD([[subQ2,1.0]])],"derivedFrom":subQ1}),-1.0]])]});}
            var Q461;
            {var subQ0=sQuery(id+"F0.wireOp",EDGE,"E2.10.1.1");var subQ1=sQuery(id+"F0.wireOp",EDGE,"E2.9.1.0");var subQ2=makeQuery(id+"F0.imprint","INTERSECT",VERTEX,{"derivedFrom":[subQ1,subQ0]});Q461=makeQuery(id+"F0.imprint","IMPRINT",FACE,{"disambiguationData":[TD([[makeQuery(id+"F0.imprint","IMPRINT",EDGE,{"disambiguationData":[TD([[subQ2,1.0]])],"derivedFrom":subQ1}),-1.0]])]});}
            var Q462;
            {var subQ0=sQuery(id+"F0.wireOp",EDGE,"E2.10.3.1");var subQ1=sQuery(id+"F0.wireOp",EDGE,"E2.9.3.0");var subQ2=makeQuery(id+"F0.imprint","INTERSECT",VERTEX,{"derivedFrom":[subQ1,subQ0]});Q462=makeQuery(id+"F0.imprint","IMPRINT",FACE,{"disambiguationData":[TD([[makeQuery(id+"F0.imprint","IMPRINT",EDGE,{"disambiguationData":[TD([[subQ2,1.0]])],"derivedFrom":subQ1}),-1.0]])]});}
            var Q463;
            {var subQ0=sQuery(id+"F0.wireOp",EDGE,"E2.10.5.1");var subQ1=sQuery(id+"F0.wireOp",EDGE,"E2.9.5.0");var subQ2=makeQuery(id+"F0.imprint","INTERSECT",VERTEX,{"derivedFrom":[subQ1,subQ0]});Q463=makeQuery(id+"F0.imprint","IMPRINT",FACE,{"disambiguationData":[TD([[makeQuery(id+"F0.imprint","IMPRINT",EDGE,{"disambiguationData":[TD([[subQ2,1.0]])],"derivedFrom":subQ1}),-1.0]])]});}
            var Q464;
            {var subQ0=sQuery(id+"F0.wireOp",EDGE,"E2.8.3.1");var subQ1=sQuery(id+"F0.wireOp",EDGE,"E2.7.3.0");var subQ2=makeQuery(id+"F0.imprint","INTERSECT",VERTEX,{"derivedFrom":[subQ1,subQ0]});Q464=makeQuery(id+"F0.imprint","IMPRINT",FACE,{"disambiguationData":[TD([[makeQuery(id+"F0.imprint","IMPRINT",EDGE,{"disambiguationData":[TD([[subQ2,1.0]])],"derivedFrom":subQ1}),-1.0]])]});}
            var Q465;
            {var subQ0=sQuery(id+"F0.wireOp",EDGE,"E2.9.1.1");var subQ1=sQuery(id+"F0.wireOp",EDGE,"E2.8.1.0");var subQ2=makeQuery(id+"F0.imprint","INTERSECT",VERTEX,{"derivedFrom":[subQ1,subQ0]});Q465=makeQuery(id+"F0.imprint","IMPRINT",FACE,{"disambiguationData":[TD([[makeQuery(id+"F0.imprint","IMPRINT",EDGE,{"disambiguationData":[TD([[subQ2,1.0]])],"derivedFrom":subQ1}),-1.0]])]});}
            var Q466;
            {var subQ0=sQuery(id+"F0.wireOp",EDGE,"E2.8.1.1");var subQ1=sQuery(id+"F0.wireOp",EDGE,"E2.7.1.0");var subQ2=makeQuery(id+"F0.imprint","INTERSECT",VERTEX,{"derivedFrom":[subQ1,subQ0]});Q466=makeQuery(id+"F0.imprint","IMPRINT",FACE,{"disambiguationData":[TD([[makeQuery(id+"F0.imprint","IMPRINT",EDGE,{"disambiguationData":[TD([[subQ2,1.0]])],"derivedFrom":subQ1}),-1.0]])]});}
            var Q467;
            {var subQ0=sQuery(id+"F0.wireOp",EDGE,"E2.4.2.0");var subQ1=sQuery(id+"F0.wireOp",EDGE,"E2.4.1.0");var subQ2=makeQuery(id+"F0.imprint","INTERSECT",VERTEX,{"disambiguationData":[OD(0.0)],"derivedFrom":[subQ1,subQ0]});Q467=makeQuery(id+"F0.imprint","IMPRINT",FACE,{"disambiguationData":[TD([[makeQuery(id+"F0.imprint","IMPRINT",EDGE,{"disambiguationData":[TD([[subQ2,-1.0]])],"derivedFrom":subQ1}),-1.0]])]});}
            var Q468;
            {var subQ0=sQuery(id+"F0.wireOp",EDGE,"E2.4.6.0");var subQ1=sQuery(id+"F0.wireOp",EDGE,"E2.4.5.0");var subQ2=makeQuery(id+"F0.imprint","INTERSECT",VERTEX,{"disambiguationData":[OD(0.0)],"derivedFrom":[subQ1,subQ0]});Q468=makeQuery(id+"F0.imprint","IMPRINT",FACE,{"disambiguationData":[TD([[makeQuery(id+"F0.imprint","IMPRINT",EDGE,{"disambiguationData":[TD([[subQ2,-1.0]])],"derivedFrom":subQ1}),-1.0]])]});}
            var Q469;
            {var subQ0=sQuery(id+"F0.wireOp",EDGE,"E2.5.2.0");var subQ1=sQuery(id+"F0.wireOp",EDGE,"E2.5.1.0");var subQ2=makeQuery(id+"F0.imprint","INTERSECT",VERTEX,{"disambiguationData":[OD(0.0)],"derivedFrom":[subQ1,subQ0]});Q469=makeQuery(id+"F0.imprint","IMPRINT",FACE,{"disambiguationData":[TD([[makeQuery(id+"F0.imprint","IMPRINT",EDGE,{"disambiguationData":[TD([[subQ2,-1.0]])],"derivedFrom":subQ1}),-1.0]])]});}
            var Q470;
            {var subQ0=sQuery(id+"F0.wireOp",EDGE,"E2.2.6.0");var subQ1=sQuery(id+"F0.wireOp",EDGE,"E2.2.5.0");var subQ2=makeQuery(id+"F0.imprint","INTERSECT",VERTEX,{"disambiguationData":[OD(0.0)],"derivedFrom":[subQ1,subQ0]});Q470=makeQuery(id+"F0.imprint","IMPRINT",FACE,{"disambiguationData":[TD([[makeQuery(id+"F0.imprint","IMPRINT",EDGE,{"disambiguationData":[TD([[subQ2,-1.0]])],"derivedFrom":subQ1}),-1.0]])]});}
            var Q471;
            {var subQ0=sQuery(id+"F0.wireOp",EDGE,"E2.3.2.0");var subQ1=sQuery(id+"F0.wireOp",EDGE,"E2.3.1.0");var subQ2=makeQuery(id+"F0.imprint","INTERSECT",VERTEX,{"disambiguationData":[OD(0.0)],"derivedFrom":[subQ1,subQ0]});Q471=makeQuery(id+"F0.imprint","IMPRINT",FACE,{"disambiguationData":[TD([[makeQuery(id+"F0.imprint","IMPRINT",EDGE,{"disambiguationData":[TD([[subQ2,-1.0]])],"derivedFrom":subQ1}),-1.0]])]});}
            var Q472;
            {var subQ0=sQuery(id+"F0.wireOp",EDGE,"E2.3.4.0");var subQ1=sQuery(id+"F0.wireOp",EDGE,"E2.3.3.0");var subQ2=makeQuery(id+"F0.imprint","INTERSECT",VERTEX,{"disambiguationData":[OD(0.0)],"derivedFrom":[subQ1,subQ0]});Q472=makeQuery(id+"F0.imprint","IMPRINT",FACE,{"disambiguationData":[TD([[makeQuery(id+"F0.imprint","IMPRINT",EDGE,{"disambiguationData":[TD([[subQ2,-1.0]])],"derivedFrom":subQ1}),-1.0]])]});}
            var Q473;
            {var subQ0=sQuery(id+"F0.wireOp",EDGE,"E2.3.6.0");var subQ1=sQuery(id+"F0.wireOp",EDGE,"E2.3.5.0");var subQ2=makeQuery(id+"F0.imprint","INTERSECT",VERTEX,{"disambiguationData":[OD(0.0)],"derivedFrom":[subQ1,subQ0]});Q473=makeQuery(id+"F0.imprint","IMPRINT",FACE,{"disambiguationData":[TD([[makeQuery(id+"F0.imprint","IMPRINT",EDGE,{"disambiguationData":[TD([[subQ2,-1.0]])],"derivedFrom":subQ1}),-1.0]])]});}
            var Q474;
            {var subQ0=sQuery(id+"F0.wireOp",EDGE,"E2.1.4.0");var subQ1=sQuery(id+"F0.wireOp",EDGE,"E2.1.3.0");var subQ2=makeQuery(id+"F0.imprint","INTERSECT",VERTEX,{"disambiguationData":[OD(0.0)],"derivedFrom":[subQ1,subQ0]});Q474=makeQuery(id+"F0.imprint","IMPRINT",FACE,{"disambiguationData":[TD([[makeQuery(id+"F0.imprint","IMPRINT",EDGE,{"disambiguationData":[TD([[subQ2,-1.0]])],"derivedFrom":subQ1}),-1.0]])]});}
            var Q475;
            {var subQ0=sQuery(id+"F0.wireOp",EDGE,"E2.1.6.0");var subQ1=sQuery(id+"F0.wireOp",EDGE,"E2.1.5.0");var subQ2=makeQuery(id+"F0.imprint","INTERSECT",VERTEX,{"disambiguationData":[OD(0.0)],"derivedFrom":[subQ1,subQ0]});Q475=makeQuery(id+"F0.imprint","IMPRINT",FACE,{"disambiguationData":[TD([[makeQuery(id+"F0.imprint","IMPRINT",EDGE,{"disambiguationData":[TD([[subQ2,-1.0]])],"derivedFrom":subQ1}),-1.0]])]});}
            var Q476;
            {var subQ0=sQuery(id+"F0.wireOp",EDGE,"E2.2.2.0");var subQ1=sQuery(id+"F0.wireOp",EDGE,"E2.2.1.0");var subQ2=makeQuery(id+"F0.imprint","INTERSECT",VERTEX,{"disambiguationData":[OD(0.0)],"derivedFrom":[subQ1,subQ0]});Q476=makeQuery(id+"F0.imprint","IMPRINT",FACE,{"disambiguationData":[TD([[makeQuery(id+"F0.imprint","IMPRINT",EDGE,{"disambiguationData":[TD([[subQ2,-1.0]])],"derivedFrom":subQ1}),-1.0]])]});}
            var Q477;
            {var subQ0=sQuery(id+"F0.wireOp",EDGE,"E2.2.4.0");var subQ1=sQuery(id+"F0.wireOp",EDGE,"E2.2.3.0");var subQ2=makeQuery(id+"F0.imprint","INTERSECT",VERTEX,{"disambiguationData":[OD(0.0)],"derivedFrom":[subQ1,subQ0]});Q477=makeQuery(id+"F0.imprint","IMPRINT",FACE,{"disambiguationData":[TD([[makeQuery(id+"F0.imprint","IMPRINT",EDGE,{"disambiguationData":[TD([[subQ2,-1.0]])],"derivedFrom":subQ1}),-1.0]])]});}
            var Q478;
            {var subQ0=sQuery(id+"F0.wireOp",EDGE,"E2.1.3.0");var subQ1=sQuery(id+"F0.wireOp",EDGE,"E2.0.3.0");var subQ2=makeQuery(id+"F0.imprint","INTERSECT",VERTEX,{"disambiguationData":[OD(0.0)],"derivedFrom":[subQ1,subQ0]});Q478=makeQuery(id+"F0.imprint","IMPRINT",FACE,{"disambiguationData":[TD([[makeQuery(id+"F0.imprint","IMPRINT",EDGE,{"disambiguationData":[TD([[subQ2,-1.0]])],"derivedFrom":subQ1}),1.0]])]});}
            var Q479;
            {var subQ0=sQuery(id+"F0.wireOp",EDGE,"E2.0.6.0");var subQ1=sQuery(id+"F0.wireOp",EDGE,"E2.0.5.0");var subQ2=makeQuery(id+"F0.imprint","INTERSECT",VERTEX,{"disambiguationData":[OD(1.0)],"derivedFrom":[subQ1,subQ0]});Q479=makeQuery(id+"F0.imprint","IMPRINT",FACE,{"disambiguationData":[TD([[makeQuery(id+"F0.imprint","IMPRINT",EDGE,{"disambiguationData":[TD([[subQ2,-1.0]])],"derivedFrom":subQ1}),1.0]])]});}
            var Q480;
            {var subQ0=sQuery(id+"F0.wireOp",EDGE,"E2.1.2.0");var subQ1=sQuery(id+"F0.wireOp",EDGE,"E2.1.1.0");var subQ2=makeQuery(id+"F0.imprint","INTERSECT",VERTEX,{"disambiguationData":[OD(0.0)],"derivedFrom":[subQ1,subQ0]});Q480=makeQuery(id+"F0.imprint","IMPRINT",FACE,{"disambiguationData":[TD([[makeQuery(id+"F0.imprint","IMPRINT",EDGE,{"disambiguationData":[TD([[subQ2,-1.0]])],"derivedFrom":subQ1}),-1.0]])]});}
            var Q481;
            {var subQ0=sQuery(id+"F0.wireOp",EDGE,"E2.4.0.0");var subQ1=sQuery(id+"F0.wireOp",EDGE,"E2.3.0.0");var subQ2=makeQuery(id+"F0.imprint","INTERSECT",VERTEX,{"disambiguationData":[OD(0.0)],"derivedFrom":[subQ1,subQ0]});Q481=makeQuery(id+"F0.imprint","IMPRINT",FACE,{"disambiguationData":[TD([[makeQuery(id+"F0.imprint","IMPRINT",EDGE,{"disambiguationData":[TD([[subQ2,-1.0]])],"derivedFrom":subQ1}),-1.0]])]});}
            var Q482;
            {var subQ0=sQuery(id+"F0.wireOp",EDGE,"E2.8.0.0");var subQ1=sQuery(id+"F0.wireOp",EDGE,"E2.7.0.0");var subQ2=makeQuery(id+"F0.imprint","INTERSECT",VERTEX,{"disambiguationData":[OD(0.0)],"derivedFrom":[subQ1,subQ0]});Q482=makeQuery(id+"F0.imprint","IMPRINT",FACE,{"disambiguationData":[TD([[makeQuery(id+"F0.imprint","IMPRINT",EDGE,{"disambiguationData":[TD([[subQ2,-1.0]])],"derivedFrom":subQ1}),-1.0]])]});}
            var Q483;
            {var subQ0=sQuery(id+"F0.wireOp",EDGE,"E2.10.2.0");var subQ1=sQuery(id+"F0.wireOp",EDGE,"E2.10.1.0");var subQ2=makeQuery(id+"F0.imprint","INTERSECT",VERTEX,{"disambiguationData":[OD(0.0)],"derivedFrom":[subQ1,subQ0]});Q483=makeQuery(id+"F0.imprint","IMPRINT",FACE,{"disambiguationData":[TD([[makeQuery(id+"F0.imprint","IMPRINT",EDGE,{"disambiguationData":[TD([[subQ2,-1.0]])],"derivedFrom":subQ1}),-1.0]])]});}
            var Q484;
            {var subQ0=sQuery(id+"F0.wireOp",EDGE,"E2.10.4.0");var subQ1=sQuery(id+"F0.wireOp",EDGE,"E2.10.3.0");var subQ2=makeQuery(id+"F0.imprint","INTERSECT",VERTEX,{"disambiguationData":[OD(0.0)],"derivedFrom":[subQ1,subQ0]});Q484=makeQuery(id+"F0.imprint","IMPRINT",FACE,{"disambiguationData":[TD([[makeQuery(id+"F0.imprint","IMPRINT",EDGE,{"disambiguationData":[TD([[subQ2,-1.0]])],"derivedFrom":subQ1}),-1.0]])]});}
            var Q485;
            {var subQ0=sQuery(id+"F0.wireOp",EDGE,"E2.10.6.0");var subQ1=sQuery(id+"F0.wireOp",EDGE,"E2.10.5.0");var subQ2=makeQuery(id+"F0.imprint","INTERSECT",VERTEX,{"disambiguationData":[OD(0.0)],"derivedFrom":[subQ1,subQ0]});Q485=makeQuery(id+"F0.imprint","IMPRINT",FACE,{"disambiguationData":[TD([[makeQuery(id+"F0.imprint","IMPRINT",EDGE,{"disambiguationData":[TD([[subQ2,-1.0]])],"derivedFrom":subQ1}),-1.0]])]});}
            var Q486;
            {var subQ0=sQuery(id+"F0.wireOp",EDGE,"E2.8.6.0");var subQ1=sQuery(id+"F0.wireOp",EDGE,"E2.8.5.0");var subQ2=makeQuery(id+"F0.imprint","INTERSECT",VERTEX,{"disambiguationData":[OD(0.0)],"derivedFrom":[subQ1,subQ0]});Q486=makeQuery(id+"F0.imprint","IMPRINT",FACE,{"disambiguationData":[TD([[makeQuery(id+"F0.imprint","IMPRINT",EDGE,{"disambiguationData":[TD([[subQ2,-1.0]])],"derivedFrom":subQ1}),-1.0]])]});}
            var Q487;
            {var subQ0=sQuery(id+"F0.wireOp",EDGE,"E2.9.2.0");var subQ1=sQuery(id+"F0.wireOp",EDGE,"E2.9.1.0");var subQ2=makeQuery(id+"F0.imprint","INTERSECT",VERTEX,{"disambiguationData":[OD(0.0)],"derivedFrom":[subQ1,subQ0]});Q487=makeQuery(id+"F0.imprint","IMPRINT",FACE,{"disambiguationData":[TD([[makeQuery(id+"F0.imprint","IMPRINT",EDGE,{"disambiguationData":[TD([[subQ2,-1.0]])],"derivedFrom":subQ1}),-1.0]])]});}
            var Q488;
            {var subQ0=sQuery(id+"F0.wireOp",EDGE,"E2.9.6.0");var subQ1=sQuery(id+"F0.wireOp",EDGE,"E2.9.5.0");var subQ2=makeQuery(id+"F0.imprint","INTERSECT",VERTEX,{"disambiguationData":[OD(0.0)],"derivedFrom":[subQ1,subQ0]});Q488=makeQuery(id+"F0.imprint","IMPRINT",FACE,{"disambiguationData":[TD([[makeQuery(id+"F0.imprint","IMPRINT",EDGE,{"disambiguationData":[TD([[subQ2,-1.0]])],"derivedFrom":subQ1}),-1.0]])]});}
            var Q489;
            {var subQ0=sQuery(id+"F0.wireOp",EDGE,"E2.7.4.0");var subQ1=sQuery(id+"F0.wireOp",EDGE,"E2.7.3.0");var subQ2=makeQuery(id+"F0.imprint","INTERSECT",VERTEX,{"disambiguationData":[OD(0.0)],"derivedFrom":[subQ1,subQ0]});Q489=makeQuery(id+"F0.imprint","IMPRINT",FACE,{"disambiguationData":[TD([[makeQuery(id+"F0.imprint","IMPRINT",EDGE,{"disambiguationData":[TD([[subQ2,-1.0]])],"derivedFrom":subQ1}),-1.0]])]});}
            var Q490;
            {var subQ0=sQuery(id+"F0.wireOp",EDGE,"E2.7.6.0");var subQ1=sQuery(id+"F0.wireOp",EDGE,"E2.7.5.0");var subQ2=makeQuery(id+"F0.imprint","INTERSECT",VERTEX,{"disambiguationData":[OD(0.0)],"derivedFrom":[subQ1,subQ0]});Q490=makeQuery(id+"F0.imprint","IMPRINT",FACE,{"disambiguationData":[TD([[makeQuery(id+"F0.imprint","IMPRINT",EDGE,{"disambiguationData":[TD([[subQ2,-1.0]])],"derivedFrom":subQ1}),-1.0]])]});}
            var Q491;
            {var subQ0=sQuery(id+"F0.wireOp",EDGE,"E2.8.2.0");var subQ1=sQuery(id+"F0.wireOp",EDGE,"E2.8.1.0");var subQ2=makeQuery(id+"F0.imprint","INTERSECT",VERTEX,{"disambiguationData":[OD(0.0)],"derivedFrom":[subQ1,subQ0]});Q491=makeQuery(id+"F0.imprint","IMPRINT",FACE,{"disambiguationData":[TD([[makeQuery(id+"F0.imprint","IMPRINT",EDGE,{"disambiguationData":[TD([[subQ2,-1.0]])],"derivedFrom":subQ1}),-1.0]])]});}
            var Q492;
            {var subQ0=sQuery(id+"F0.wireOp",EDGE,"E2.8.4.0");var subQ1=sQuery(id+"F0.wireOp",EDGE,"E2.8.3.0");var subQ2=makeQuery(id+"F0.imprint","INTERSECT",VERTEX,{"disambiguationData":[OD(0.0)],"derivedFrom":[subQ1,subQ0]});Q492=makeQuery(id+"F0.imprint","IMPRINT",FACE,{"disambiguationData":[TD([[makeQuery(id+"F0.imprint","IMPRINT",EDGE,{"disambiguationData":[TD([[subQ2,-1.0]])],"derivedFrom":subQ1}),-1.0]])]});}
            var Q493;
            {var subQ0=sQuery(id+"F0.wireOp",EDGE,"E2.6.4.0");var subQ1=sQuery(id+"F0.wireOp",EDGE,"E2.6.3.0");var subQ2=makeQuery(id+"F0.imprint","INTERSECT",VERTEX,{"disambiguationData":[OD(0.0)],"derivedFrom":[subQ1,subQ0]});Q493=makeQuery(id+"F0.imprint","IMPRINT",FACE,{"disambiguationData":[TD([[makeQuery(id+"F0.imprint","IMPRINT",EDGE,{"disambiguationData":[TD([[subQ2,-1.0]])],"derivedFrom":subQ1}),-1.0]])]});}
            var Q494;
            {var subQ0=sQuery(id+"F0.wireOp",EDGE,"E2.6.2.0");var subQ1=sQuery(id+"F0.wireOp",EDGE,"E2.6.1.0");var subQ2=makeQuery(id+"F0.imprint","INTERSECT",VERTEX,{"disambiguationData":[OD(0.0)],"derivedFrom":[subQ1,subQ0]});Q494=makeQuery(id+"F0.imprint","IMPRINT",FACE,{"disambiguationData":[TD([[makeQuery(id+"F0.imprint","IMPRINT",EDGE,{"disambiguationData":[TD([[subQ2,-1.0]])],"derivedFrom":subQ1}),-1.0]])]});}
            var Q495;
            {var subQ0=sQuery(id+"F0.wireOp",EDGE,"E2.5.6.0");var subQ1=sQuery(id+"F0.wireOp",EDGE,"E2.5.5.0");var subQ2=makeQuery(id+"F0.imprint","INTERSECT",VERTEX,{"disambiguationData":[OD(0.0)],"derivedFrom":[subQ1,subQ0]});Q495=makeQuery(id+"F0.imprint","IMPRINT",FACE,{"disambiguationData":[TD([[makeQuery(id+"F0.imprint","IMPRINT",EDGE,{"disambiguationData":[TD([[subQ2,-1.0]])],"derivedFrom":subQ1}),-1.0]])]});}
            var Q496;
            {var subQ0=sQuery(id+"F0.wireOp",EDGE,"E2.5.4.0");var subQ1=sQuery(id+"F0.wireOp",EDGE,"E2.5.3.0");var subQ2=makeQuery(id+"F0.imprint","INTERSECT",VERTEX,{"disambiguationData":[OD(0.0)],"derivedFrom":[subQ1,subQ0]});Q496=makeQuery(id+"F0.imprint","IMPRINT",FACE,{"disambiguationData":[TD([[makeQuery(id+"F0.imprint","IMPRINT",EDGE,{"disambiguationData":[TD([[subQ2,-1.0]])],"derivedFrom":subQ1}),-1.0]])]});}
            var Q497;
            {var subQ0=sQuery(id+"F0.wireOp",EDGE,"E2.7.2.0");var subQ1=sQuery(id+"F0.wireOp",EDGE,"E2.7.1.0");var subQ2=makeQuery(id+"F0.imprint","INTERSECT",VERTEX,{"disambiguationData":[OD(0.0)],"derivedFrom":[subQ1,subQ0]});Q497=makeQuery(id+"F0.imprint","IMPRINT",FACE,{"disambiguationData":[TD([[makeQuery(id+"F0.imprint","IMPRINT",EDGE,{"disambiguationData":[TD([[subQ2,-1.0]])],"derivedFrom":subQ1}),-1.0]])]});}
            var Q498;
            {var subQ0=sQuery(id+"F0.wireOp",EDGE,"E2.6.6.0");var subQ1=sQuery(id+"F0.wireOp",EDGE,"E2.6.5.0");var subQ2=makeQuery(id+"F0.imprint","INTERSECT",VERTEX,{"disambiguationData":[OD(0.0)],"derivedFrom":[subQ1,subQ0]});Q498=makeQuery(id+"F0.imprint","IMPRINT",FACE,{"disambiguationData":[TD([[makeQuery(id+"F0.imprint","IMPRINT",EDGE,{"disambiguationData":[TD([[subQ2,-1.0]])],"derivedFrom":subQ1}),-1.0]])]});}
            var Q499;
            {var subQ0=sQuery(id+"F0.wireOp",EDGE,"E2.10.6.0");var subQ1=sQuery(id+"F0.wireOp",EDGE,"E2.10.5.0");var subQ2=makeQuery(id+"F0.imprint","INTERSECT",VERTEX,{"disambiguationData":[OD(0.0)],"derivedFrom":[subQ1,subQ0]});Q499=makeQuery(id+"F0.imprint","IMPRINT",FACE,{"disambiguationData":[TD([[makeQuery(id+"F0.imprint","IMPRINT",EDGE,{"disambiguationData":[TD([[subQ2,-1.0]])],"derivedFrom":subQ1}),1.0]])]});}
            var Q500;
            {var subQ0=sQuery(id+"F0.wireOp",EDGE,"E2.2.2.0");var subQ1=sQuery(id+"F0.wireOp",EDGE,"E2.2.1.0");var subQ2=makeQuery(id+"F0.imprint","INTERSECT",VERTEX,{"disambiguationData":[OD(0.0)],"derivedFrom":[subQ1,subQ0]});Q500=makeQuery(id+"F0.imprint","IMPRINT",FACE,{"disambiguationData":[TD([[makeQuery(id+"F0.imprint","IMPRINT",EDGE,{"disambiguationData":[TD([[subQ2,-1.0]])],"derivedFrom":subQ1}),1.0]])]});}
            var Q501;
            {var subQ0=sQuery(id+"F0.wireOp",EDGE,"E2.1.2.0");var subQ1=sQuery(id+"F0.wireOp",EDGE,"E2.1.1.0");var subQ2=makeQuery(id+"F0.imprint","INTERSECT",VERTEX,{"disambiguationData":[OD(0.0)],"derivedFrom":[subQ1,subQ0]});Q501=makeQuery(id+"F0.imprint","IMPRINT",FACE,{"disambiguationData":[TD([[makeQuery(id+"F0.imprint","IMPRINT",EDGE,{"disambiguationData":[TD([[subQ2,-1.0]])],"derivedFrom":subQ1}),1.0]])]});}
            var Q502;
            {var subQ0=sQuery(id+"F0.wireOp",EDGE,"E2.9.2.0");var subQ1=sQuery(id+"F0.wireOp",EDGE,"E2.9.1.0");var subQ2=makeQuery(id+"F0.imprint","INTERSECT",VERTEX,{"disambiguationData":[OD(0.0)],"derivedFrom":[subQ1,subQ0]});Q502=makeQuery(id+"F0.imprint","IMPRINT",FACE,{"disambiguationData":[TD([[makeQuery(id+"F0.imprint","IMPRINT",EDGE,{"disambiguationData":[TD([[subQ2,-1.0]])],"derivedFrom":subQ1}),1.0]])]});}
            var Q503;
            {var subQ0=sQuery(id+"F0.wireOp",EDGE,"E2.8.2.0");var subQ1=sQuery(id+"F0.wireOp",EDGE,"E2.8.1.0");var subQ2=makeQuery(id+"F0.imprint","INTERSECT",VERTEX,{"disambiguationData":[OD(0.0)],"derivedFrom":[subQ1,subQ0]});Q503=makeQuery(id+"F0.imprint","IMPRINT",FACE,{"disambiguationData":[TD([[makeQuery(id+"F0.imprint","IMPRINT",EDGE,{"disambiguationData":[TD([[subQ2,-1.0]])],"derivedFrom":subQ1}),1.0]])]});}
            var Q504;
            {var subQ0=sQuery(id+"F0.wireOp",EDGE,"E2.6.6.0");var subQ1=sQuery(id+"F0.wireOp",EDGE,"E2.6.5.0");var subQ2=makeQuery(id+"F0.imprint","INTERSECT",VERTEX,{"disambiguationData":[OD(0.0)],"derivedFrom":[subQ1,subQ0]});Q504=makeQuery(id+"F0.imprint","IMPRINT",FACE,{"disambiguationData":[TD([[makeQuery(id+"F0.imprint","IMPRINT",EDGE,{"disambiguationData":[TD([[subQ2,-1.0]])],"derivedFrom":subQ1}),1.0]])]});}
            var Q505;
            {var subQ0=sQuery(id+"F0.wireOp",EDGE,"E2.7.2.0");var subQ1=sQuery(id+"F0.wireOp",EDGE,"E2.7.1.0");var subQ2=makeQuery(id+"F0.imprint","INTERSECT",VERTEX,{"disambiguationData":[OD(0.0)],"derivedFrom":[subQ1,subQ0]});Q505=makeQuery(id+"F0.imprint","IMPRINT",FACE,{"disambiguationData":[TD([[makeQuery(id+"F0.imprint","IMPRINT",EDGE,{"disambiguationData":[TD([[subQ2,-1.0]])],"derivedFrom":subQ1}),1.0]])]});}
            var Q506;
            {var subQ0=sQuery(id+"F0.wireOp",EDGE,"E2.4.2.0");var subQ1=sQuery(id+"F0.wireOp",EDGE,"E2.4.1.0");var subQ2=makeQuery(id+"F0.imprint","INTERSECT",VERTEX,{"disambiguationData":[OD(0.0)],"derivedFrom":[subQ1,subQ0]});Q506=makeQuery(id+"F0.imprint","IMPRINT",FACE,{"disambiguationData":[TD([[makeQuery(id+"F0.imprint","IMPRINT",EDGE,{"disambiguationData":[TD([[subQ2,-1.0]])],"derivedFrom":subQ1}),1.0]])]});}
            var Q507;
            {var subQ0=sQuery(id+"F0.wireOp",EDGE,"E2.2.5.0");var subQ1=sQuery(id+"F0.wireOp",EDGE,"E2.2.4.0");var subQ2=makeQuery(id+"F0.imprint","INTERSECT",VERTEX,{"disambiguationData":[OD(0.0)],"derivedFrom":[subQ1,subQ0]});Q507=makeQuery(id+"F0.imprint","IMPRINT",FACE,{"disambiguationData":[TD([[makeQuery(id+"F0.imprint","IMPRINT",EDGE,{"disambiguationData":[TD([[subQ2,-1.0]])],"derivedFrom":subQ1}),1.0]])]});}
            var Q508;
            {var subQ0=sQuery(id+"F0.wireOp",EDGE,"E2.3.2.0");var subQ1=sQuery(id+"F0.wireOp",EDGE,"E2.3.1.0");var subQ2=makeQuery(id+"F0.imprint","INTERSECT",VERTEX,{"disambiguationData":[OD(0.0)],"derivedFrom":[subQ1,subQ0]});Q508=makeQuery(id+"F0.imprint","IMPRINT",FACE,{"disambiguationData":[TD([[makeQuery(id+"F0.imprint","IMPRINT",EDGE,{"disambiguationData":[TD([[subQ2,-1.0]])],"derivedFrom":subQ1}),1.0]])]});}
            var Q509;
            {var subQ0=sQuery(id+"F0.wireOp",EDGE,"E2.3.6.0");var subQ1=sQuery(id+"F0.wireOp",EDGE,"E2.3.5.0");var subQ2=makeQuery(id+"F0.imprint","INTERSECT",VERTEX,{"disambiguationData":[OD(0.0)],"derivedFrom":[subQ1,subQ0]});Q509=makeQuery(id+"F0.imprint","IMPRINT",FACE,{"disambiguationData":[TD([[makeQuery(id+"F0.imprint","IMPRINT",EDGE,{"disambiguationData":[TD([[subQ2,-1.0]])],"derivedFrom":subQ1}),1.0]])]});}
            var Q510;
            {var subQ0=sQuery(id+"F0.wireOp",EDGE,"E2.1.6.0");var subQ1=sQuery(id+"F0.wireOp",EDGE,"E2.1.5.0");var subQ2=makeQuery(id+"F0.imprint","INTERSECT",VERTEX,{"disambiguationData":[OD(0.0)],"derivedFrom":[subQ1,subQ0]});Q510=makeQuery(id+"F0.imprint","IMPRINT",FACE,{"disambiguationData":[TD([[makeQuery(id+"F0.imprint","IMPRINT",EDGE,{"disambiguationData":[TD([[subQ2,-1.0]])],"derivedFrom":subQ1}),1.0]])]});}
            var Q511;
            {var subQ0=sQuery(id+"F0.wireOp",EDGE,"E2.11.1.0");var subQ1=sQuery(id+"F0.wireOp",EDGE,"E2.10.1.0");var subQ2=makeQuery(id+"F0.imprint","INTERSECT",VERTEX,{"disambiguationData":[OD(0.0)],"derivedFrom":[subQ1,subQ0]});Q511=makeQuery(id+"F0.imprint","IMPRINT",FACE,{"disambiguationData":[TD([[makeQuery(id+"F0.imprint","IMPRINT",EDGE,{"disambiguationData":[TD([[subQ2,-1.0]])],"derivedFrom":subQ1}),-1.0]])]});}
            var Q512;
            {var subQ0=sQuery(id+"F0.wireOp",EDGE,"E2.11.0.0");var subQ1=sQuery(id+"F0.wireOp",EDGE,"E2.10.0.0");var subQ2=makeQuery(id+"F0.imprint","INTERSECT",VERTEX,{"disambiguationData":[OD(1.0)],"derivedFrom":[subQ1,subQ0]});Q512=makeQuery(id+"F0.imprint","IMPRINT",FACE,{"disambiguationData":[TD([[makeQuery(id+"F0.imprint","IMPRINT",EDGE,{"disambiguationData":[TD([[subQ2,-1.0]])],"derivedFrom":subQ1}),-1.0]])]});}
            var Q513;
            {var subQ0=sQuery(id+"F0.wireOp",EDGE,"E4");Q513=makeQuery(id+"F0.imprint","IMPRINT",FACE,{"disambiguationData":[TD([[makeQuery(id+"F0.imprint","IMPRINT",EDGE,{"derivedFrom":subQ0}),1.0]])]});}
            extrude(context, id + "F1", {"entities" : qUnion([Q0, Q1, Q2, Q3, Q4, Q5, Q6, Q7, Q8, Q9, Q10, Q11, Q12, Q13, Q14, Q15, Q16, Q17, Q18, Q19, Q20, Q21, Q22, Q23, Q24, Q25, Q26, Q27, Q28, Q29, Q30, Q31, Q32, Q33, Q34, Q35, Q36, Q37, Q38, Q39, Q40, Q41, Q42, Q43, Q44, Q45, Q46, Q47, Q48, Q49, Q50, Q51, Q52, Q53, Q54, Q55, Q56, Q57, Q58, Q59, Q60, Q61, Q62, Q63, Q64, Q65, Q66, Q67, Q68, Q69, Q70, Q71, Q72, Q73, Q74, Q75, Q76, Q77, Q78, Q79, Q80, Q81, Q82, Q83, Q84, Q85, Q86, Q87, Q88, Q89, Q90, Q91, Q92, Q93, Q94, Q95, Q96, Q97, Q98, Q99, Q100, Q101, Q102, Q103, Q104, Q105, Q106, Q107, Q108, Q109, Q110, Q111, Q112, Q113, Q114, Q115, Q116, Q117, Q118, Q119, Q120, Q121, Q122, Q123, Q124, Q125, Q126, Q127, Q128, Q129, Q130, Q131, Q132, Q133, Q134, Q135, Q136, Q137, Q138, Q139, Q140, Q141, Q142, Q143, Q144, Q145, Q146, Q147, Q148, Q149, Q150, Q151, Q152, Q153, Q154, Q155, Q156, Q157, Q158, Q159, Q160, Q161, Q162, Q163, Q164, Q165, Q166, Q167, Q168, Q169, Q170, Q171, Q172, Q173, Q174, Q175, Q176, Q177, Q178, Q179, Q180, Q181, Q182, Q183, Q184, Q185, Q186, Q187, Q188, Q189, Q190, Q191, Q192, Q193, Q194, Q195, Q196, Q197, Q198, Q199, Q200, Q201, Q202, Q203, Q204, Q205, Q206, Q207, Q208, Q209, Q210, Q211, Q212, Q213, Q214, Q215, Q216, Q217, Q218, Q219, Q220, Q221, Q222, Q223, Q224, Q225, Q226, Q227, Q228, Q229, Q230, Q231, Q232, Q233, Q234, Q235, Q236, Q237, Q238, Q239, Q240, Q241, Q242, Q243, Q244, Q245, Q246, Q247, Q248, Q249, Q250, Q251, Q252, Q253, Q254, Q255, Q256, Q257, Q258, Q259, Q260, Q261, Q262, Q263, Q264, Q265, Q266, Q267, Q268, Q269, Q270, Q271, Q272, Q273, Q274, Q275, Q276, Q277, Q278, Q279, Q280, Q281, Q282, Q283, Q284, Q285, Q286, Q287, Q288, Q289, Q290, Q291, Q292, Q293, Q294, Q295, Q296, Q297, Q298, Q299, Q300, Q301, Q302, Q303, Q304, Q305, Q306, Q307, Q308, Q309, Q310, Q311, Q312, Q313, Q314, Q315, Q316, Q317, Q318, Q319, Q320, Q321, Q322, Q323, Q324, Q325, Q326, Q327, Q328, Q329, Q330, Q331, Q332, Q333, Q334, Q335, Q336, Q337, Q338, Q339, Q340, Q341, Q342, Q343, Q344, Q345, Q346, Q347, Q348, Q349, Q350, Q351, Q352, Q353, Q354, Q355, Q356, Q357, Q358, Q359, Q360, Q361, Q362, Q363, Q364, Q365, Q366, Q367, Q368, Q369, Q370, Q371, Q372, Q373, Q374, Q375, Q376, Q377, Q378, Q379, Q380, Q381, Q382, Q383, Q384, Q385, Q386, Q387, Q388, Q389, Q390, Q391, Q392, Q393, Q394, Q395, Q396, Q397, Q398, Q399, Q400, Q401, Q402, Q403, Q404, Q405, Q406, Q407, Q408, Q409, Q410, Q411, Q412, Q413, Q414, Q415, Q416, Q417, Q418, Q419, Q420, Q421, Q422, Q423, Q424, Q425, Q426, Q427, Q428, Q429, Q430, Q431, Q432, Q433, Q434, Q435, Q436, Q437, Q438, Q439, Q440, Q441, Q442, Q443, Q444, Q445, Q446, Q447, Q448, Q449, Q450, Q451, Q452, Q453, Q454, Q455, Q456, Q457, Q458, Q459, Q460, Q461, Q462, Q463, Q464, Q465, Q466, Q467, Q468, Q469, Q470, Q471, Q472, Q473, Q474, Q475, Q476, Q477, Q478, Q479, Q480, Q481, Q482, Q483, Q484, Q485, Q486, Q487, Q488, Q489, Q490, Q491, Q492, Q493, Q494, Q495, Q496, Q497, Q498, Q499, Q500, Q501, Q502, Q503, Q504, Q505, Q506, Q507, Q508, Q509, Q510, Q511, Q512, Q513]), "depth" : 12.7 * mm});
        }
    });
